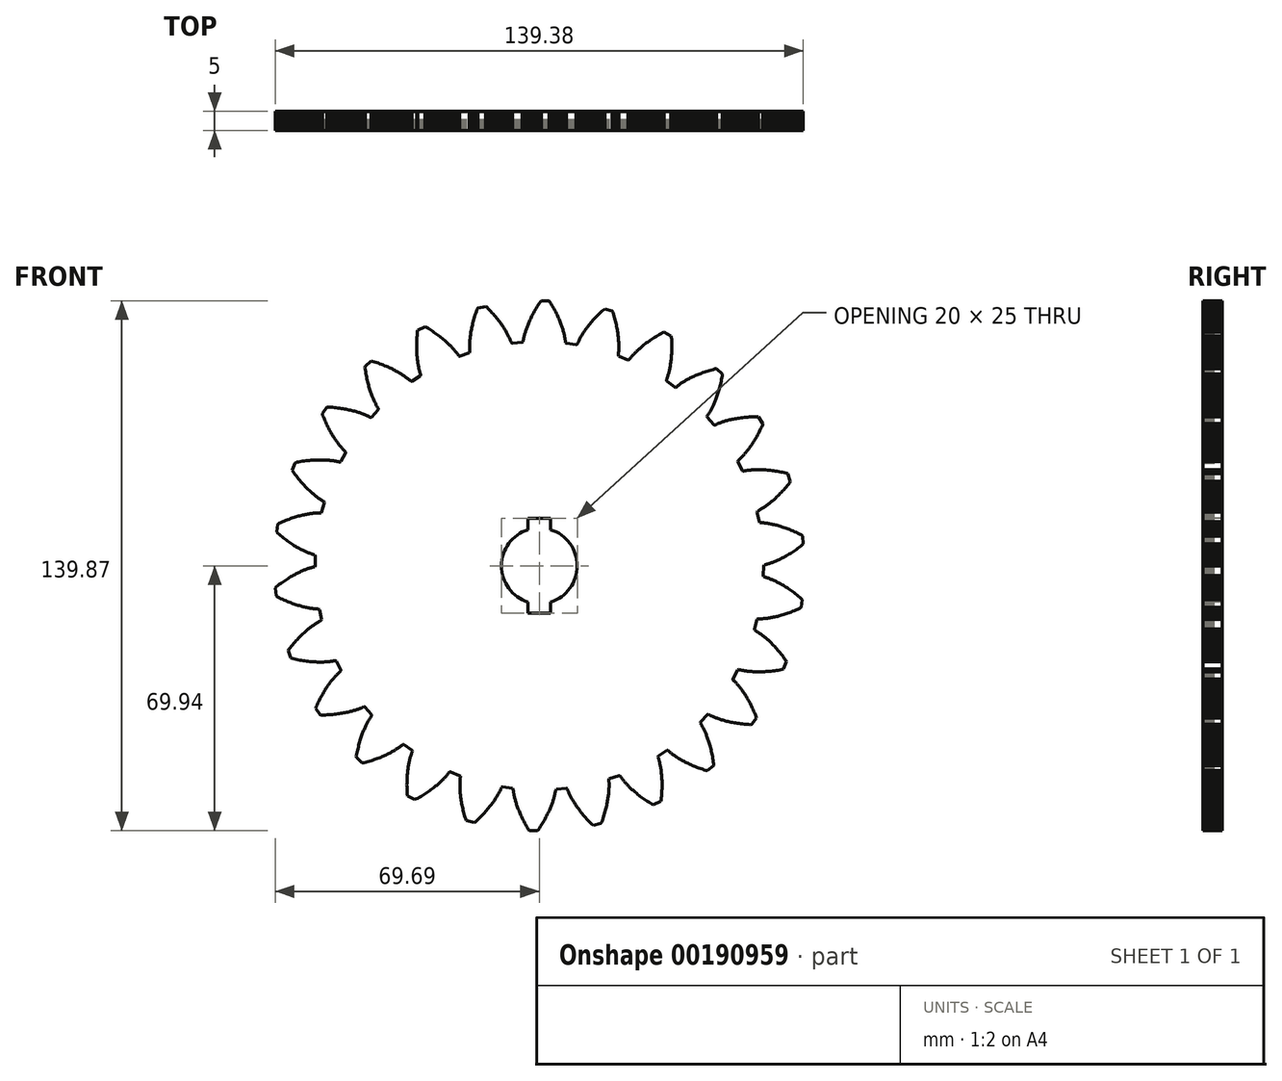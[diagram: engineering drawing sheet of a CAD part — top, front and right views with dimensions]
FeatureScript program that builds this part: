
annotation { "Feature Type Name" : "Feature", "Feature Type Description" : "" }
export const myFeature = defineFeature(function(context is Context, id is Id, definition is map)
    precondition{}
    {
        {
            var Q0;
            Q0=qCreatedBy(makeId("Front.planeOp"),FACE);
            var sketch = newSketch(context, id + "F0", { "sketchPlane" : qUnion([Q0])});
            skLineSegment(sketch, "E0", {"start": v(59.2, 0) * mm, "end": v(59.33, 0.22) * mm});
            skLineSegment(sketch, "E1", {"start": v(59.33, 0.22) * mm, "end": v(59.5, 0.27) * mm});
            skLineSegment(sketch, "E2", {"start": v(59.5, 0.27) * mm, "end": v(59.7, 0.31) * mm});
            skLineSegment(sketch, "E3", {"start": v(59.7, 0.31) * mm, "end": v(59.9, 0.37) * mm});
            skLineSegment(sketch, "E4", {"start": v(59.9, 0.37) * mm, "end": v(60.1, 0.42) * mm});
            skLineSegment(sketch, "E5", {"start": v(60.1, 0.42) * mm, "end": v(60.31, 0.49) * mm});
            skLineSegment(sketch, "E6", {"start": v(60.31, 0.49) * mm, "end": v(60.53, 0.55) * mm});
            skLineSegment(sketch, "E7", {"start": v(60.53, 0.55) * mm, "end": v(60.77, 0.63) * mm});
            skLineSegment(sketch, "E8", {"start": v(60.77, 0.63) * mm, "end": v(61, 0.71) * mm});
            skLineSegment(sketch, "E9", {"start": v(61, 0.71) * mm, "end": v(61.26, 0.8) * mm});
            skLineSegment(sketch, "E10", {"start": v(61.26, 0.8) * mm, "end": v(61.51, 0.9) * mm});
            skLineSegment(sketch, "E11", {"start": v(61.51, 0.9) * mm, "end": v(61.78, 1) * mm});
            skLineSegment(sketch, "E12", {"start": v(61.78, 1) * mm, "end": v(62.06, 1.1) * mm});
            skLineSegment(sketch, "E13", {"start": v(62.06, 1.1) * mm, "end": v(62.34, 1.23) * mm});
            skLineSegment(sketch, "E14", {"start": v(62.34, 1.23) * mm, "end": v(62.63, 1.35) * mm});
            skLineSegment(sketch, "E15", {"start": v(62.63, 1.35) * mm, "end": v(62.93, 1.49) * mm});
            skLineSegment(sketch, "E16", {"start": v(62.93, 1.49) * mm, "end": v(63.24, 1.63) * mm});
            skLineSegment(sketch, "E17", {"start": v(63.24, 1.63) * mm, "end": v(63.55, 1.78) * mm});
            skLineSegment(sketch, "E18", {"start": v(63.55, 1.78) * mm, "end": v(63.87, 1.94) * mm});
            skLineSegment(sketch, "E19", {"start": v(63.87, 1.94) * mm, "end": v(64.2, 2.1) * mm});
            skLineSegment(sketch, "E20", {"start": v(64.2, 2.1) * mm, "end": v(64.53, 2.29) * mm});
            skLineSegment(sketch, "E21", {"start": v(64.53, 2.29) * mm, "end": v(64.88, 2.48) * mm});
            skLineSegment(sketch, "E22", {"start": v(64.88, 2.48) * mm, "end": v(65.22, 2.67) * mm});
            skLineSegment(sketch, "E23", {"start": v(65.22, 2.67) * mm, "end": v(65.58, 2.88) * mm});
            skLineSegment(sketch, "E24", {"start": v(65.58, 2.88) * mm, "end": v(65.94, 3.1) * mm});
            skLineSegment(sketch, "E25", {"start": v(65.94, 3.1) * mm, "end": v(66.3, 3.33) * mm});
            skLineSegment(sketch, "E26", {"start": v(66.3, 3.33) * mm, "end": v(66.68, 3.56) * mm});
            skLineSegment(sketch, "E27", {"start": v(66.68, 3.56) * mm, "end": v(67.06, 3.81) * mm});
            skLineSegment(sketch, "E28", {"start": v(67.06, 3.81) * mm, "end": v(67.44, 4.07) * mm});
            skLineSegment(sketch, "E29", {"start": v(67.44, 4.07) * mm, "end": v(67.83, 4.34) * mm});
            skLineSegment(sketch, "E30", {"start": v(67.83, 4.34) * mm, "end": v(68.22, 4.63) * mm});
            skLineSegment(sketch, "E31", {"start": v(68.22, 4.63) * mm, "end": v(68.62, 4.92) * mm});
            skLineSegment(sketch, "E32", {"start": v(68.62, 4.92) * mm, "end": v(69.02, 5.23) * mm});
            skLineSegment(sketch, "E33", {"start": v(69.02, 5.23) * mm, "end": v(69.43, 5.54) * mm});
            skLineSegment(sketch, "E34", {"start": v(69.43, 5.54) * mm, "end": v(69.7, 5.86) * mm});
            skLineSegment(sketch, "E35", {"start": v(69.7, 5.86) * mm, "end": v(69.49, 7.9) * mm});
            skLineSegment(sketch, "E36", {"start": v(69.49, 7.9) * mm, "end": v(69.17, 8.16) * mm});
            skLineSegment(sketch, "E37", {"start": v(69.17, 8.16) * mm, "end": v(68.7, 8.4) * mm});
            skLineSegment(sketch, "E38", {"start": v(68.7, 8.4) * mm, "end": v(68.25, 8.61) * mm});
            skLineSegment(sketch, "E39", {"start": v(68.25, 8.61) * mm, "end": v(67.8, 8.82) * mm});
            skLineSegment(sketch, "E40", {"start": v(67.8, 8.82) * mm, "end": v(67.37, 9.02) * mm});
            skLineSegment(sketch, "E41", {"start": v(67.37, 9.02) * mm, "end": v(66.93, 9.21) * mm});
            skLineSegment(sketch, "E42", {"start": v(66.93, 9.21) * mm, "end": v(66.5, 9.4) * mm});
            skLineSegment(sketch, "E43", {"start": v(66.5, 9.4) * mm, "end": v(66.09, 9.56) * mm});
            skLineSegment(sketch, "E44", {"start": v(66.09, 9.56) * mm, "end": v(65.67, 9.72) * mm});
            skLineSegment(sketch, "E45", {"start": v(65.67, 9.72) * mm, "end": v(65.27, 9.88) * mm});
            skLineSegment(sketch, "E46", {"start": v(65.27, 9.88) * mm, "end": v(64.87, 10.02) * mm});
            skLineSegment(sketch, "E47", {"start": v(64.87, 10.02) * mm, "end": v(64.49, 10.15) * mm});
            skLineSegment(sketch, "E48", {"start": v(64.49, 10.15) * mm, "end": v(64.1, 10.28) * mm});
            skLineSegment(sketch, "E49", {"start": v(64.1, 10.28) * mm, "end": v(63.73, 10.4) * mm});
            skLineSegment(sketch, "E50", {"start": v(63.73, 10.4) * mm, "end": v(63.37, 10.5) * mm});
            skLineSegment(sketch, "E51", {"start": v(63.37, 10.5) * mm, "end": v(63.01, 10.6) * mm});
            skLineSegment(sketch, "E52", {"start": v(63.01, 10.6) * mm, "end": v(62.67, 10.7) * mm});
            skLineSegment(sketch, "E53", {"start": v(62.67, 10.7) * mm, "end": v(62.33, 10.79) * mm});
            skLineSegment(sketch, "E54", {"start": v(62.33, 10.79) * mm, "end": v(62, 10.87) * mm});
            skLineSegment(sketch, "E55", {"start": v(62, 10.87) * mm, "end": v(61.68, 10.94) * mm});
            skLineSegment(sketch, "E56", {"start": v(61.68, 10.94) * mm, "end": v(61.37, 11) * mm});
            skLineSegment(sketch, "E57", {"start": v(61.37, 11) * mm, "end": v(61.07, 11.06) * mm});
            skLineSegment(sketch, "E58", {"start": v(61.07, 11.06) * mm, "end": v(60.78, 11.12) * mm});
            skLineSegment(sketch, "E59", {"start": v(60.78, 11.12) * mm, "end": v(60.5, 11.17) * mm});
            skLineSegment(sketch, "E60", {"start": v(60.5, 11.17) * mm, "end": v(60.23, 11.21) * mm});
            skLineSegment(sketch, "E61", {"start": v(60.23, 11.21) * mm, "end": v(59.97, 11.25) * mm});
            skLineSegment(sketch, "E62", {"start": v(59.97, 11.25) * mm, "end": v(59.71, 11.28) * mm});
            skLineSegment(sketch, "E63", {"start": v(59.71, 11.28) * mm, "end": v(59.47, 11.31) * mm});
            skLineSegment(sketch, "E64", {"start": v(59.47, 11.31) * mm, "end": v(59.24, 11.33) * mm});
            skLineSegment(sketch, "E65", {"start": v(59.24, 11.33) * mm, "end": v(59.02, 11.35) * mm});
            skLineSegment(sketch, "E66", {"start": v(59.02, 11.35) * mm, "end": v(58.8, 11.37) * mm});
            skLineSegment(sketch, "E67", {"start": v(58.8, 11.37) * mm, "end": v(58.6, 11.38) * mm});
            skLineSegment(sketch, "E68", {"start": v(58.6, 11.38) * mm, "end": v(58.41, 11.4) * mm});
            skLineSegment(sketch, "E69", {"start": v(58.41, 11.4) * mm, "end": v(58.23, 11.4) * mm});
            skLineSegment(sketch, "E70", {"start": v(58.23, 11.4) * mm, "end": v(58.05, 11.6) * mm});
            skLineSegment(sketch, "E71", {"start": v(58.05, 11.6) * mm, "end": v(57.48, 14.17) * mm});
            skLineSegment(sketch, "E72", {"start": v(57.48, 14.17) * mm, "end": v(57.56, 14.42) * mm});
            skLineSegment(sketch, "E73", {"start": v(57.56, 14.42) * mm, "end": v(57.72, 14.5) * mm});
            skLineSegment(sketch, "E74", {"start": v(57.72, 14.5) * mm, "end": v(57.89, 14.59) * mm});
            skLineSegment(sketch, "E75", {"start": v(57.89, 14.59) * mm, "end": v(58.06, 14.69) * mm});
            skLineSegment(sketch, "E76", {"start": v(58.06, 14.69) * mm, "end": v(58.25, 14.8) * mm});
            skLineSegment(sketch, "E77", {"start": v(58.25, 14.8) * mm, "end": v(58.44, 14.9) * mm});
            skLineSegment(sketch, "E78", {"start": v(58.44, 14.9) * mm, "end": v(58.64, 15.03) * mm});
            skLineSegment(sketch, "E79", {"start": v(58.64, 15.03) * mm, "end": v(58.85, 15.15) * mm});
            skLineSegment(sketch, "E80", {"start": v(58.85, 15.15) * mm, "end": v(59.06, 15.3) * mm});
            skLineSegment(sketch, "E81", {"start": v(59.06, 15.3) * mm, "end": v(59.28, 15.44) * mm});
            skLineSegment(sketch, "E82", {"start": v(59.28, 15.44) * mm, "end": v(59.51, 15.6) * mm});
            skLineSegment(sketch, "E83", {"start": v(59.51, 15.6) * mm, "end": v(59.75, 15.75) * mm});
            skLineSegment(sketch, "E84", {"start": v(59.75, 15.75) * mm, "end": v(59.99, 15.93) * mm});
            skLineSegment(sketch, "E85", {"start": v(59.99, 15.93) * mm, "end": v(60.23, 16.11) * mm});
            skLineSegment(sketch, "E86", {"start": v(60.23, 16.11) * mm, "end": v(60.49, 16.3) * mm});
            skLineSegment(sketch, "E87", {"start": v(60.49, 16.3) * mm, "end": v(60.75, 16.5) * mm});
            skLineSegment(sketch, "E88", {"start": v(60.75, 16.5) * mm, "end": v(61, 16.72) * mm});
            skLineSegment(sketch, "E89", {"start": v(61, 16.72) * mm, "end": v(61.28, 16.94) * mm});
            skLineSegment(sketch, "E90", {"start": v(61.28, 16.94) * mm, "end": v(61.55, 17.17) * mm});
            skLineSegment(sketch, "E91", {"start": v(61.55, 17.17) * mm, "end": v(61.83, 17.41) * mm});
            skLineSegment(sketch, "E92", {"start": v(61.83, 17.41) * mm, "end": v(62.11, 17.67) * mm});
            skLineSegment(sketch, "E93", {"start": v(62.11, 17.67) * mm, "end": v(62.4, 17.93) * mm});
            skLineSegment(sketch, "E94", {"start": v(62.4, 17.93) * mm, "end": v(62.69, 18.2) * mm});
            skLineSegment(sketch, "E95", {"start": v(62.69, 18.2) * mm, "end": v(62.98, 18.5) * mm});
            skLineSegment(sketch, "E96", {"start": v(62.98, 18.5) * mm, "end": v(63.28, 18.79) * mm});
            skLineSegment(sketch, "E97", {"start": v(63.28, 18.79) * mm, "end": v(63.58, 19.1) * mm});
            skLineSegment(sketch, "E98", {"start": v(63.58, 19.1) * mm, "end": v(63.89, 19.42) * mm});
            skLineSegment(sketch, "E99", {"start": v(63.89, 19.42) * mm, "end": v(64.2, 19.75) * mm});
            skLineSegment(sketch, "E100", {"start": v(64.2, 19.75) * mm, "end": v(64.5, 20.1) * mm});
            skLineSegment(sketch, "E101", {"start": v(64.5, 20.1) * mm, "end": v(64.82, 20.45) * mm});
            skLineSegment(sketch, "E102", {"start": v(64.82, 20.45) * mm, "end": v(65.13, 20.82) * mm});
            skLineSegment(sketch, "E103", {"start": v(65.13, 20.82) * mm, "end": v(65.45, 21.2) * mm});
            skLineSegment(sketch, "E104", {"start": v(65.45, 21.2) * mm, "end": v(65.76, 21.6) * mm});
            skLineSegment(sketch, "E105", {"start": v(65.76, 21.6) * mm, "end": v(66.08, 22) * mm});
            skLineSegment(sketch, "E106", {"start": v(66.08, 22) * mm, "end": v(66.26, 22.37) * mm});
            skLineSegment(sketch, "E107", {"start": v(66.26, 22.37) * mm, "end": v(65.58, 24.3) * mm});
            skLineSegment(sketch, "E108", {"start": v(65.58, 24.3) * mm, "end": v(65.2, 24.48) * mm});
            skLineSegment(sketch, "E109", {"start": v(65.2, 24.48) * mm, "end": v(64.7, 24.6) * mm});
            skLineSegment(sketch, "E110", {"start": v(64.7, 24.6) * mm, "end": v(64.2, 24.7) * mm});
            skLineSegment(sketch, "E111", {"start": v(64.2, 24.7) * mm, "end": v(63.72, 24.8) * mm});
            skLineSegment(sketch, "E112", {"start": v(63.72, 24.8) * mm, "end": v(63.25, 24.88) * mm});
            skLineSegment(sketch, "E113", {"start": v(63.25, 24.88) * mm, "end": v(62.78, 24.96) * mm});
            skLineSegment(sketch, "E114", {"start": v(62.78, 24.96) * mm, "end": v(62.32, 25.04) * mm});
            skLineSegment(sketch, "E115", {"start": v(62.32, 25.04) * mm, "end": v(61.88, 25.1) * mm});
            skLineSegment(sketch, "E116", {"start": v(61.88, 25.1) * mm, "end": v(61.44, 25.16) * mm});
            skLineSegment(sketch, "E117", {"start": v(61.44, 25.16) * mm, "end": v(61.01, 25.2) * mm});
            skLineSegment(sketch, "E118", {"start": v(61.01, 25.2) * mm, "end": v(60.6, 25.25) * mm});
            skLineSegment(sketch, "E119", {"start": v(60.6, 25.25) * mm, "end": v(60.18, 25.29) * mm});
            skLineSegment(sketch, "E120", {"start": v(60.18, 25.29) * mm, "end": v(59.78, 25.32) * mm});
            skLineSegment(sketch, "E121", {"start": v(59.78, 25.32) * mm, "end": v(59.4, 25.34) * mm});
            skLineSegment(sketch, "E122", {"start": v(59.4, 25.34) * mm, "end": v(59.01, 25.36) * mm});
            skLineSegment(sketch, "E123", {"start": v(59.01, 25.36) * mm, "end": v(58.64, 25.38) * mm});
            skLineSegment(sketch, "E124", {"start": v(58.64, 25.38) * mm, "end": v(58.29, 25.38) * mm});
            skLineSegment(sketch, "E125", {"start": v(58.29, 25.38) * mm, "end": v(57.94, 25.39) * mm});
            skLineSegment(sketch, "E126", {"start": v(57.94, 25.39) * mm, "end": v(57.6, 25.39) * mm});
            skLineSegment(sketch, "E127", {"start": v(57.6, 25.39) * mm, "end": v(57.27, 25.38) * mm});
            skLineSegment(sketch, "E128", {"start": v(57.27, 25.38) * mm, "end": v(56.96, 25.37) * mm});
            skLineSegment(sketch, "E129", {"start": v(56.96, 25.37) * mm, "end": v(56.65, 25.36) * mm});
            skLineSegment(sketch, "E130", {"start": v(56.65, 25.36) * mm, "end": v(56.35, 25.34) * mm});
            skLineSegment(sketch, "E131", {"start": v(56.35, 25.34) * mm, "end": v(56.07, 25.32) * mm});
            skLineSegment(sketch, "E132", {"start": v(56.07, 25.32) * mm, "end": v(55.8, 25.3) * mm});
            skLineSegment(sketch, "E133", {"start": v(55.8, 25.3) * mm, "end": v(55.53, 25.27) * mm});
            skLineSegment(sketch, "E134", {"start": v(55.53, 25.27) * mm, "end": v(55.28, 25.24) * mm});
            skLineSegment(sketch, "E135", {"start": v(55.28, 25.24) * mm, "end": v(55.04, 25.21) * mm});
            skLineSegment(sketch, "E136", {"start": v(55.04, 25.21) * mm, "end": v(54.8, 25.18) * mm});
            skLineSegment(sketch, "E137", {"start": v(54.8, 25.18) * mm, "end": v(54.58, 25.15) * mm});
            skLineSegment(sketch, "E138", {"start": v(54.58, 25.15) * mm, "end": v(54.37, 25.11) * mm});
            skLineSegment(sketch, "E139", {"start": v(54.37, 25.11) * mm, "end": v(54.17, 25.08) * mm});
            skLineSegment(sketch, "E140", {"start": v(54.17, 25.08) * mm, "end": v(53.99, 25.04) * mm});
            skLineSegment(sketch, "E141", {"start": v(53.99, 25.04) * mm, "end": v(53.8, 25) * mm});
            skLineSegment(sketch, "E142", {"start": v(53.8, 25) * mm, "end": v(53.59, 25.15) * mm});
            skLineSegment(sketch, "E143", {"start": v(53.59, 25.15) * mm, "end": v(52.42, 27.5) * mm});
            skLineSegment(sketch, "E144", {"start": v(52.42, 27.5) * mm, "end": v(52.43, 27.77) * mm});
            skLineSegment(sketch, "E145", {"start": v(52.43, 27.77) * mm, "end": v(52.57, 27.9) * mm});
            skLineSegment(sketch, "E146", {"start": v(52.57, 27.9) * mm, "end": v(52.71, 28.02) * mm});
            skLineSegment(sketch, "E147", {"start": v(52.71, 28.02) * mm, "end": v(52.86, 28.16) * mm});
            skLineSegment(sketch, "E148", {"start": v(52.86, 28.16) * mm, "end": v(53.02, 28.3) * mm});
            skLineSegment(sketch, "E149", {"start": v(53.02, 28.3) * mm, "end": v(53.18, 28.46) * mm});
            skLineSegment(sketch, "E150", {"start": v(53.18, 28.46) * mm, "end": v(53.34, 28.62) * mm});
            skLineSegment(sketch, "E151", {"start": v(53.34, 28.62) * mm, "end": v(53.51, 28.8) * mm});
            skLineSegment(sketch, "E152", {"start": v(53.51, 28.8) * mm, "end": v(53.69, 28.98) * mm});
            skLineSegment(sketch, "E153", {"start": v(53.69, 28.98) * mm, "end": v(53.87, 29.18) * mm});
            skLineSegment(sketch, "E154", {"start": v(53.87, 29.18) * mm, "end": v(54.05, 29.38) * mm});
            skLineSegment(sketch, "E155", {"start": v(54.05, 29.38) * mm, "end": v(54.24, 29.6) * mm});
            skLineSegment(sketch, "E156", {"start": v(54.24, 29.6) * mm, "end": v(54.43, 29.82) * mm});
            skLineSegment(sketch, "E157", {"start": v(54.43, 29.82) * mm, "end": v(54.63, 30.06) * mm});
            skLineSegment(sketch, "E158", {"start": v(54.63, 30.06) * mm, "end": v(54.83, 30.3) * mm});
            skLineSegment(sketch, "E159", {"start": v(54.83, 30.3) * mm, "end": v(55.03, 30.56) * mm});
            skLineSegment(sketch, "E160", {"start": v(55.03, 30.56) * mm, "end": v(55.23, 30.83) * mm});
            skLineSegment(sketch, "E161", {"start": v(55.23, 30.83) * mm, "end": v(55.44, 31.1) * mm});
            skLineSegment(sketch, "E162", {"start": v(55.44, 31.1) * mm, "end": v(55.65, 31.4) * mm});
            skLineSegment(sketch, "E163", {"start": v(55.65, 31.4) * mm, "end": v(55.86, 31.7) * mm});
            skLineSegment(sketch, "E164", {"start": v(55.86, 31.7) * mm, "end": v(56.08, 32.02) * mm});
            skLineSegment(sketch, "E165", {"start": v(56.08, 32.02) * mm, "end": v(56.3, 32.34) * mm});
            skLineSegment(sketch, "E166", {"start": v(56.3, 32.34) * mm, "end": v(56.51, 32.68) * mm});
            skLineSegment(sketch, "E167", {"start": v(56.51, 32.68) * mm, "end": v(56.73, 33.03) * mm});
            skLineSegment(sketch, "E168", {"start": v(56.73, 33.03) * mm, "end": v(56.95, 33.39) * mm});
            skLineSegment(sketch, "E169", {"start": v(56.95, 33.39) * mm, "end": v(57.17, 33.76) * mm});
            skLineSegment(sketch, "E170", {"start": v(57.17, 33.76) * mm, "end": v(57.39, 34.14) * mm});
            skLineSegment(sketch, "E171", {"start": v(57.39, 34.14) * mm, "end": v(57.6, 34.54) * mm});
            skLineSegment(sketch, "E172", {"start": v(57.6, 34.54) * mm, "end": v(57.82, 34.95) * mm});
            skLineSegment(sketch, "E173", {"start": v(57.82, 34.95) * mm, "end": v(58.04, 35.37) * mm});
            skLineSegment(sketch, "E174", {"start": v(58.04, 35.37) * mm, "end": v(58.26, 35.8) * mm});
            skLineSegment(sketch, "E175", {"start": v(58.26, 35.8) * mm, "end": v(58.47, 36.25) * mm});
            skLineSegment(sketch, "E176", {"start": v(58.47, 36.25) * mm, "end": v(58.69, 36.7) * mm});
            skLineSegment(sketch, "E177", {"start": v(58.69, 36.7) * mm, "end": v(58.9, 37.17) * mm});
            skLineSegment(sketch, "E178", {"start": v(58.9, 37.17) * mm, "end": v(58.98, 37.58) * mm});
            skLineSegment(sketch, "E179", {"start": v(58.98, 37.58) * mm, "end": v(57.86, 39.29) * mm});
            skLineSegment(sketch, "E180", {"start": v(57.86, 39.29) * mm, "end": v(57.45, 39.37) * mm});
            skLineSegment(sketch, "E181", {"start": v(57.45, 39.37) * mm, "end": v(56.94, 39.36) * mm});
            skLineSegment(sketch, "E182", {"start": v(56.94, 39.36) * mm, "end": v(56.43, 39.35) * mm});
            skLineSegment(sketch, "E183", {"start": v(56.43, 39.35) * mm, "end": v(55.94, 39.32) * mm});
            skLineSegment(sketch, "E184", {"start": v(55.94, 39.32) * mm, "end": v(55.46, 39.3) * mm});
            skLineSegment(sketch, "E185", {"start": v(55.46, 39.3) * mm, "end": v(54.98, 39.26) * mm});
            skLineSegment(sketch, "E186", {"start": v(54.98, 39.26) * mm, "end": v(54.52, 39.22) * mm});
            skLineSegment(sketch, "E187", {"start": v(54.52, 39.22) * mm, "end": v(54.07, 39.18) * mm});
            skLineSegment(sketch, "E188", {"start": v(54.07, 39.18) * mm, "end": v(53.63, 39.13) * mm});
            skLineSegment(sketch, "E189", {"start": v(53.63, 39.13) * mm, "end": v(53.2, 39.08) * mm});
            skLineSegment(sketch, "E190", {"start": v(53.2, 39.08) * mm, "end": v(52.79, 39.02) * mm});
            skLineSegment(sketch, "E191", {"start": v(52.79, 39.02) * mm, "end": v(52.38, 38.96) * mm});
            skLineSegment(sketch, "E192", {"start": v(52.38, 38.96) * mm, "end": v(51.99, 38.9) * mm});
            skLineSegment(sketch, "E193", {"start": v(51.99, 38.9) * mm, "end": v(51.6, 38.82) * mm});
            skLineSegment(sketch, "E194", {"start": v(51.6, 38.82) * mm, "end": v(51.23, 38.75) * mm});
            skLineSegment(sketch, "E195", {"start": v(51.23, 38.75) * mm, "end": v(50.87, 38.67) * mm});
            skLineSegment(sketch, "E196", {"start": v(50.87, 38.67) * mm, "end": v(50.52, 38.6) * mm});
            skLineSegment(sketch, "E197", {"start": v(50.52, 38.6) * mm, "end": v(50.18, 38.52) * mm});
            skLineSegment(sketch, "E198", {"start": v(50.18, 38.52) * mm, "end": v(49.85, 38.43) * mm});
            skLineSegment(sketch, "E199", {"start": v(49.85, 38.43) * mm, "end": v(49.53, 38.35) * mm});
            skLineSegment(sketch, "E200", {"start": v(49.53, 38.35) * mm, "end": v(49.23, 38.27) * mm});
            skLineSegment(sketch, "E201", {"start": v(49.23, 38.27) * mm, "end": v(48.93, 38.18) * mm});
            skLineSegment(sketch, "E202", {"start": v(48.93, 38.18) * mm, "end": v(48.65, 38.1) * mm});
            skLineSegment(sketch, "E203", {"start": v(48.65, 38.1) * mm, "end": v(48.38, 38) * mm});
            skLineSegment(sketch, "E204", {"start": v(48.38, 38) * mm, "end": v(48.12, 37.92) * mm});
            skLineSegment(sketch, "E205", {"start": v(48.12, 37.92) * mm, "end": v(47.87, 37.83) * mm});
            skLineSegment(sketch, "E206", {"start": v(47.87, 37.83) * mm, "end": v(47.63, 37.74) * mm});
            skLineSegment(sketch, "E207", {"start": v(47.63, 37.74) * mm, "end": v(47.4, 37.65) * mm});
            skLineSegment(sketch, "E208", {"start": v(47.4, 37.65) * mm, "end": v(47.18, 37.56) * mm});
            skLineSegment(sketch, "E209", {"start": v(47.18, 37.56) * mm, "end": v(46.98, 37.48) * mm});
            skLineSegment(sketch, "E210", {"start": v(46.98, 37.48) * mm, "end": v(46.78, 37.4) * mm});
            skLineSegment(sketch, "E211", {"start": v(46.78, 37.4) * mm, "end": v(46.6, 37.31) * mm});
            skLineSegment(sketch, "E212", {"start": v(46.6, 37.31) * mm, "end": v(46.42, 37.23) * mm});
            skLineSegment(sketch, "E213", {"start": v(46.42, 37.23) * mm, "end": v(46.26, 37.15) * mm});
            skLineSegment(sketch, "E214", {"start": v(46.26, 37.15) * mm, "end": v(46.01, 37.24) * mm});
            skLineSegment(sketch, "E215", {"start": v(46.01, 37.24) * mm, "end": v(44.31, 39.25) * mm});
            skLineSegment(sketch, "E216", {"start": v(44.31, 39.25) * mm, "end": v(44.26, 39.51) * mm});
            skLineSegment(sketch, "E217", {"start": v(44.26, 39.51) * mm, "end": v(44.37, 39.66) * mm});
            skLineSegment(sketch, "E218", {"start": v(44.37, 39.66) * mm, "end": v(44.48, 39.82) * mm});
            skLineSegment(sketch, "E219", {"start": v(44.48, 39.82) * mm, "end": v(44.59, 39.99) * mm});
            skLineSegment(sketch, "E220", {"start": v(44.59, 39.99) * mm, "end": v(44.7, 40.17) * mm});
            skLineSegment(sketch, "E221", {"start": v(44.7, 40.17) * mm, "end": v(44.82, 40.36) * mm});
            skLineSegment(sketch, "E222", {"start": v(44.82, 40.36) * mm, "end": v(44.94, 40.56) * mm});
            skLineSegment(sketch, "E223", {"start": v(44.94, 40.56) * mm, "end": v(45.07, 40.77) * mm});
            skLineSegment(sketch, "E224", {"start": v(45.07, 40.77) * mm, "end": v(45.2, 40.99) * mm});
            skLineSegment(sketch, "E225", {"start": v(45.2, 40.99) * mm, "end": v(45.32, 41.22) * mm});
            skLineSegment(sketch, "E226", {"start": v(45.32, 41.22) * mm, "end": v(45.45, 41.46) * mm});
            skLineSegment(sketch, "E227", {"start": v(45.45, 41.46) * mm, "end": v(45.58, 41.72) * mm});
            skLineSegment(sketch, "E228", {"start": v(45.58, 41.72) * mm, "end": v(45.71, 41.98) * mm});
            skLineSegment(sketch, "E229", {"start": v(45.71, 41.98) * mm, "end": v(45.85, 42.26) * mm});
            skLineSegment(sketch, "E230", {"start": v(45.85, 42.26) * mm, "end": v(45.98, 42.54) * mm});
            skLineSegment(sketch, "E231", {"start": v(45.98, 42.54) * mm, "end": v(46.12, 42.84) * mm});
            skLineSegment(sketch, "E232", {"start": v(46.12, 42.84) * mm, "end": v(46.25, 43.15) * mm});
            skLineSegment(sketch, "E233", {"start": v(46.25, 43.15) * mm, "end": v(46.39, 43.47) * mm});
            skLineSegment(sketch, "E234", {"start": v(46.39, 43.47) * mm, "end": v(46.52, 43.8) * mm});
            skLineSegment(sketch, "E235", {"start": v(46.52, 43.8) * mm, "end": v(46.65, 44.15) * mm});
            skLineSegment(sketch, "E236", {"start": v(46.65, 44.15) * mm, "end": v(46.79, 44.5) * mm});
            skLineSegment(sketch, "E237", {"start": v(46.79, 44.5) * mm, "end": v(46.92, 44.87) * mm});
            skLineSegment(sketch, "E238", {"start": v(46.92, 44.87) * mm, "end": v(47.05, 45.25) * mm});
            skLineSegment(sketch, "E239", {"start": v(47.05, 45.25) * mm, "end": v(47.18, 45.64) * mm});
            skLineSegment(sketch, "E240", {"start": v(47.18, 45.64) * mm, "end": v(47.3, 46.04) * mm});
            skLineSegment(sketch, "E241", {"start": v(47.3, 46.04) * mm, "end": v(47.43, 46.46) * mm});
            skLineSegment(sketch, "E242", {"start": v(47.43, 46.46) * mm, "end": v(47.55, 46.88) * mm});
            skLineSegment(sketch, "E243", {"start": v(47.55, 46.88) * mm, "end": v(47.66, 47.32) * mm});
            skLineSegment(sketch, "E244", {"start": v(47.66, 47.32) * mm, "end": v(47.78, 47.77) * mm});
            skLineSegment(sketch, "E245", {"start": v(47.78, 47.77) * mm, "end": v(47.89, 48.23) * mm});
            skLineSegment(sketch, "E246", {"start": v(47.89, 48.23) * mm, "end": v(48, 48.7) * mm});
            skLineSegment(sketch, "E247", {"start": v(48, 48.7) * mm, "end": v(48.1, 49.19) * mm});
            skLineSegment(sketch, "E248", {"start": v(48.1, 49.19) * mm, "end": v(48.2, 49.68) * mm});
            skLineSegment(sketch, "E249", {"start": v(48.2, 49.68) * mm, "end": v(48.3, 50.19) * mm});
            skLineSegment(sketch, "E250", {"start": v(48.3, 50.19) * mm, "end": v(48.28, 50.6) * mm});
            skLineSegment(sketch, "E251", {"start": v(48.28, 50.6) * mm, "end": v(46.77, 52) * mm});
            skLineSegment(sketch, "E252", {"start": v(46.77, 52) * mm, "end": v(46.36, 51.98) * mm});
            skLineSegment(sketch, "E253", {"start": v(46.36, 51.98) * mm, "end": v(45.86, 51.84) * mm});
            skLineSegment(sketch, "E254", {"start": v(45.86, 51.84) * mm, "end": v(45.38, 51.7) * mm});
            skLineSegment(sketch, "E255", {"start": v(45.38, 51.7) * mm, "end": v(44.9, 51.57) * mm});
            skLineSegment(sketch, "E256", {"start": v(44.9, 51.57) * mm, "end": v(44.44, 51.43) * mm});
            skLineSegment(sketch, "E257", {"start": v(44.44, 51.43) * mm, "end": v(44, 51.28) * mm});
            skLineSegment(sketch, "E258", {"start": v(44, 51.28) * mm, "end": v(43.55, 51.13) * mm});
            skLineSegment(sketch, "E259", {"start": v(43.55, 51.13) * mm, "end": v(43.13, 50.98) * mm});
            skLineSegment(sketch, "E260", {"start": v(43.13, 50.98) * mm, "end": v(42.7, 50.83) * mm});
            skLineSegment(sketch, "E261", {"start": v(42.7, 50.83) * mm, "end": v(42.3, 50.67) * mm});
            skLineSegment(sketch, "E262", {"start": v(42.3, 50.67) * mm, "end": v(41.92, 50.52) * mm});
            skLineSegment(sketch, "E263", {"start": v(41.92, 50.52) * mm, "end": v(41.54, 50.36) * mm});
            skLineSegment(sketch, "E264", {"start": v(41.54, 50.36) * mm, "end": v(41.17, 50.2) * mm});
            skLineSegment(sketch, "E265", {"start": v(41.17, 50.2) * mm, "end": v(40.81, 50.04) * mm});
            skLineSegment(sketch, "E266", {"start": v(40.81, 50.04) * mm, "end": v(40.47, 49.88) * mm});
            skLineSegment(sketch, "E267", {"start": v(40.47, 49.88) * mm, "end": v(40.13, 49.72) * mm});
            skLineSegment(sketch, "E268", {"start": v(40.13, 49.72) * mm, "end": v(39.81, 49.56) * mm});
            skLineSegment(sketch, "E269", {"start": v(39.81, 49.56) * mm, "end": v(39.5, 49.4) * mm});
            skLineSegment(sketch, "E270", {"start": v(39.5, 49.4) * mm, "end": v(39.2, 49.25) * mm});
            skLineSegment(sketch, "E271", {"start": v(39.2, 49.25) * mm, "end": v(38.92, 49.1) * mm});
            skLineSegment(sketch, "E272", {"start": v(38.92, 49.1) * mm, "end": v(38.64, 48.93) * mm});
            skLineSegment(sketch, "E273", {"start": v(38.64, 48.93) * mm, "end": v(38.38, 48.78) * mm});
            skLineSegment(sketch, "E274", {"start": v(38.38, 48.78) * mm, "end": v(38.12, 48.63) * mm});
            skLineSegment(sketch, "E275", {"start": v(38.12, 48.63) * mm, "end": v(37.88, 48.48) * mm});
            skLineSegment(sketch, "E276", {"start": v(37.88, 48.48) * mm, "end": v(37.65, 48.33) * mm});
            skLineSegment(sketch, "E277", {"start": v(37.65, 48.33) * mm, "end": v(37.42, 48.18) * mm});
            skLineSegment(sketch, "E278", {"start": v(37.42, 48.18) * mm, "end": v(37.21, 48.04) * mm});
            skLineSegment(sketch, "E279", {"start": v(37.21, 48.04) * mm, "end": v(37.01, 47.9) * mm});
            skLineSegment(sketch, "E280", {"start": v(37.01, 47.9) * mm, "end": v(36.82, 47.77) * mm});
            skLineSegment(sketch, "E281", {"start": v(36.82, 47.77) * mm, "end": v(36.65, 47.63) * mm});
            skLineSegment(sketch, "E282", {"start": v(36.65, 47.63) * mm, "end": v(36.47, 47.5) * mm});
            skLineSegment(sketch, "E283", {"start": v(36.47, 47.5) * mm, "end": v(36.31, 47.38) * mm});
            skLineSegment(sketch, "E284", {"start": v(36.31, 47.38) * mm, "end": v(36.17, 47.26) * mm});
            skLineSegment(sketch, "E285", {"start": v(36.17, 47.26) * mm, "end": v(36.03, 47.15) * mm});
            skLineSegment(sketch, "E286", {"start": v(36.03, 47.15) * mm, "end": v(35.76, 47.17) * mm});
            skLineSegment(sketch, "E287", {"start": v(35.76, 47.17) * mm, "end": v(33.63, 48.72) * mm});
            skLineSegment(sketch, "E288", {"start": v(33.63, 48.72) * mm, "end": v(33.52, 48.96) * mm});
            skLineSegment(sketch, "E289", {"start": v(33.52, 48.96) * mm, "end": v(33.59, 49.13) * mm});
            skLineSegment(sketch, "E290", {"start": v(33.59, 49.13) * mm, "end": v(33.65, 49.3) * mm});
            skLineSegment(sketch, "E291", {"start": v(33.65, 49.3) * mm, "end": v(33.72, 49.5) * mm});
            skLineSegment(sketch, "E292", {"start": v(33.72, 49.5) * mm, "end": v(33.8, 49.7) * mm});
            skLineSegment(sketch, "E293", {"start": v(33.8, 49.7) * mm, "end": v(33.86, 49.91) * mm});
            skLineSegment(sketch, "E294", {"start": v(33.86, 49.91) * mm, "end": v(33.93, 50.13) * mm});
            skLineSegment(sketch, "E295", {"start": v(33.93, 50.13) * mm, "end": v(34, 50.37) * mm});
            skLineSegment(sketch, "E296", {"start": v(34, 50.37) * mm, "end": v(34.07, 50.61) * mm});
            skLineSegment(sketch, "E297", {"start": v(34.07, 50.61) * mm, "end": v(34.14, 50.87) * mm});
            skLineSegment(sketch, "E298", {"start": v(34.14, 50.87) * mm, "end": v(34.2, 51.13) * mm});
            skLineSegment(sketch, "E299", {"start": v(34.2, 51.13) * mm, "end": v(34.27, 51.41) * mm});
            skLineSegment(sketch, "E300", {"start": v(34.27, 51.41) * mm, "end": v(34.34, 51.7) * mm});
            skLineSegment(sketch, "E301", {"start": v(34.34, 51.7) * mm, "end": v(34.4, 52) * mm});
            skLineSegment(sketch, "E302", {"start": v(34.4, 52) * mm, "end": v(34.46, 52.31) * mm});
            skLineSegment(sketch, "E303", {"start": v(34.46, 52.31) * mm, "end": v(34.52, 52.63) * mm});
            skLineSegment(sketch, "E304", {"start": v(34.52, 52.63) * mm, "end": v(34.58, 52.97) * mm});
            skLineSegment(sketch, "E305", {"start": v(34.58, 52.97) * mm, "end": v(34.63, 53.31) * mm});
            skLineSegment(sketch, "E306", {"start": v(34.63, 53.31) * mm, "end": v(34.69, 53.67) * mm});
            skLineSegment(sketch, "E307", {"start": v(34.69, 53.67) * mm, "end": v(34.73, 54.03) * mm});
            skLineSegment(sketch, "E308", {"start": v(34.73, 54.03) * mm, "end": v(34.78, 54.4) * mm});
            skLineSegment(sketch, "E309", {"start": v(34.78, 54.4) * mm, "end": v(34.82, 54.8) * mm});
            skLineSegment(sketch, "E310", {"start": v(34.82, 54.8) * mm, "end": v(34.85, 55.2) * mm});
            skLineSegment(sketch, "E311", {"start": v(34.85, 55.2) * mm, "end": v(34.88, 55.6) * mm});
            skLineSegment(sketch, "E312", {"start": v(34.88, 55.6) * mm, "end": v(34.9, 56.03) * mm});
            skLineSegment(sketch, "E313", {"start": v(34.9, 56.03) * mm, "end": v(34.93, 56.46) * mm});
            skLineSegment(sketch, "E314", {"start": v(34.93, 56.46) * mm, "end": v(34.95, 56.9) * mm});
            skLineSegment(sketch, "E315", {"start": v(34.95, 56.9) * mm, "end": v(34.95, 57.35) * mm});
            skLineSegment(sketch, "E316", {"start": v(34.95, 57.35) * mm, "end": v(34.96, 57.82) * mm});
            skLineSegment(sketch, "E317", {"start": v(34.96, 57.82) * mm, "end": v(34.96, 58.29) * mm});
            skLineSegment(sketch, "E318", {"start": v(34.96, 58.29) * mm, "end": v(34.95, 58.77) * mm});
            skLineSegment(sketch, "E319", {"start": v(34.95, 58.77) * mm, "end": v(34.93, 59.27) * mm});
            skLineSegment(sketch, "E320", {"start": v(34.93, 59.27) * mm, "end": v(34.9, 59.77) * mm});
            skLineSegment(sketch, "E321", {"start": v(34.9, 59.77) * mm, "end": v(34.88, 60.29) * mm});
            skLineSegment(sketch, "E322", {"start": v(34.88, 60.29) * mm, "end": v(34.77, 60.68) * mm});
            skLineSegment(sketch, "E323", {"start": v(34.77, 60.68) * mm, "end": v(32.97, 61.68) * mm});
            skLineSegment(sketch, "E324", {"start": v(32.97, 61.68) * mm, "end": v(32.58, 61.56) * mm});
            skLineSegment(sketch, "E325", {"start": v(32.58, 61.56) * mm, "end": v(32.12, 61.31) * mm});
            skLineSegment(sketch, "E326", {"start": v(32.12, 61.31) * mm, "end": v(31.68, 61.06) * mm});
            skLineSegment(sketch, "E327", {"start": v(31.68, 61.06) * mm, "end": v(31.26, 60.82) * mm});
            skLineSegment(sketch, "E328", {"start": v(31.26, 60.82) * mm, "end": v(30.84, 60.57) * mm});
            skLineSegment(sketch, "E329", {"start": v(30.84, 60.57) * mm, "end": v(30.44, 60.32) * mm});
            skLineSegment(sketch, "E330", {"start": v(30.44, 60.32) * mm, "end": v(30.05, 60.07) * mm});
            skLineSegment(sketch, "E331", {"start": v(30.05, 60.07) * mm, "end": v(29.67, 59.82) * mm});
            skLineSegment(sketch, "E332", {"start": v(29.67, 59.82) * mm, "end": v(29.3, 59.57) * mm});
            skLineSegment(sketch, "E333", {"start": v(29.3, 59.57) * mm, "end": v(28.95, 59.33) * mm});
            skLineSegment(sketch, "E334", {"start": v(28.95, 59.33) * mm, "end": v(28.6, 59.08) * mm});
            skLineSegment(sketch, "E335", {"start": v(28.6, 59.08) * mm, "end": v(28.28, 58.84) * mm});
            skLineSegment(sketch, "E336", {"start": v(28.28, 58.84) * mm, "end": v(27.96, 58.6) * mm});
            skLineSegment(sketch, "E337", {"start": v(27.96, 58.6) * mm, "end": v(27.65, 58.36) * mm});
            skLineSegment(sketch, "E338", {"start": v(27.65, 58.36) * mm, "end": v(27.35, 58.12) * mm});
            skLineSegment(sketch, "E339", {"start": v(27.35, 58.12) * mm, "end": v(27.07, 57.88) * mm});
            skLineSegment(sketch, "E340", {"start": v(27.07, 57.88) * mm, "end": v(26.8, 57.65) * mm});
            skLineSegment(sketch, "E341", {"start": v(26.8, 57.65) * mm, "end": v(26.53, 57.42) * mm});
            skLineSegment(sketch, "E342", {"start": v(26.53, 57.42) * mm, "end": v(26.28, 57.2) * mm});
            skLineSegment(sketch, "E343", {"start": v(26.28, 57.2) * mm, "end": v(26.04, 56.98) * mm});
            skLineSegment(sketch, "E344", {"start": v(26.04, 56.98) * mm, "end": v(25.8, 56.76) * mm});
            skLineSegment(sketch, "E345", {"start": v(25.8, 56.76) * mm, "end": v(25.59, 56.55) * mm});
            skLineSegment(sketch, "E346", {"start": v(25.59, 56.55) * mm, "end": v(25.38, 56.34) * mm});
            skLineSegment(sketch, "E347", {"start": v(25.38, 56.34) * mm, "end": v(25.18, 56.13) * mm});
            skLineSegment(sketch, "E348", {"start": v(25.18, 56.13) * mm, "end": v(24.99, 55.93) * mm});
            skLineSegment(sketch, "E349", {"start": v(24.99, 55.93) * mm, "end": v(24.8, 55.74) * mm});
            skLineSegment(sketch, "E350", {"start": v(24.8, 55.74) * mm, "end": v(24.64, 55.55) * mm});
            skLineSegment(sketch, "E351", {"start": v(24.64, 55.55) * mm, "end": v(24.47, 55.37) * mm});
            skLineSegment(sketch, "E352", {"start": v(24.47, 55.37) * mm, "end": v(24.32, 55.2) * mm});
            skLineSegment(sketch, "E353", {"start": v(24.32, 55.2) * mm, "end": v(24.18, 55.02) * mm});
            skLineSegment(sketch, "E354", {"start": v(24.18, 55.02) * mm, "end": v(24.05, 54.85) * mm});
            skLineSegment(sketch, "E355", {"start": v(24.05, 54.85) * mm, "end": v(23.92, 54.7) * mm});
            skLineSegment(sketch, "E356", {"start": v(23.92, 54.7) * mm, "end": v(23.8, 54.54) * mm});
            skLineSegment(sketch, "E357", {"start": v(23.8, 54.54) * mm, "end": v(23.7, 54.4) * mm});
            skLineSegment(sketch, "E358", {"start": v(23.7, 54.4) * mm, "end": v(23.44, 54.36) * mm});
            skLineSegment(sketch, "E359", {"start": v(23.44, 54.36) * mm, "end": v(21, 55.35) * mm});
            skLineSegment(sketch, "E360", {"start": v(21, 55.35) * mm, "end": v(20.83, 55.56) * mm});
            skLineSegment(sketch, "E361", {"start": v(20.83, 55.56) * mm, "end": v(20.85, 55.74) * mm});
            skLineSegment(sketch, "E362", {"start": v(20.85, 55.74) * mm, "end": v(20.88, 55.93) * mm});
            skLineSegment(sketch, "E363", {"start": v(20.88, 55.93) * mm, "end": v(20.9, 56.13) * mm});
            skLineSegment(sketch, "E364", {"start": v(20.9, 56.13) * mm, "end": v(20.92, 56.34) * mm});
            skLineSegment(sketch, "E365", {"start": v(20.92, 56.34) * mm, "end": v(20.93, 56.56) * mm});
            skLineSegment(sketch, "E366", {"start": v(20.93, 56.56) * mm, "end": v(20.95, 56.8) * mm});
            skLineSegment(sketch, "E367", {"start": v(20.95, 56.8) * mm, "end": v(20.96, 57.04) * mm});
            skLineSegment(sketch, "E368", {"start": v(20.96, 57.04) * mm, "end": v(20.97, 57.3) * mm});
            skLineSegment(sketch, "E369", {"start": v(20.97, 57.3) * mm, "end": v(20.97, 57.56) * mm});
            skLineSegment(sketch, "E370", {"start": v(20.97, 57.56) * mm, "end": v(20.98, 57.84) * mm});
            skLineSegment(sketch, "E371", {"start": v(20.98, 57.84) * mm, "end": v(20.97, 58.12) * mm});
            skLineSegment(sketch, "E372", {"start": v(20.97, 58.12) * mm, "end": v(20.97, 58.42) * mm});
            skLineSegment(sketch, "E373", {"start": v(20.97, 58.42) * mm, "end": v(20.96, 58.72) * mm});
            skLineSegment(sketch, "E374", {"start": v(20.96, 58.72) * mm, "end": v(20.94, 59.04) * mm});
            skLineSegment(sketch, "E375", {"start": v(20.94, 59.04) * mm, "end": v(20.92, 59.37) * mm});
            skLineSegment(sketch, "E376", {"start": v(20.92, 59.37) * mm, "end": v(20.9, 59.7) * mm});
            skLineSegment(sketch, "E377", {"start": v(20.9, 59.7) * mm, "end": v(20.87, 60.05) * mm});
            skLineSegment(sketch, "E378", {"start": v(20.87, 60.05) * mm, "end": v(20.83, 60.4) * mm});
            skLineSegment(sketch, "E379", {"start": v(20.83, 60.4) * mm, "end": v(20.8, 60.77) * mm});
            skLineSegment(sketch, "E380", {"start": v(20.8, 60.77) * mm, "end": v(20.75, 61.15) * mm});
            skLineSegment(sketch, "E381", {"start": v(20.75, 61.15) * mm, "end": v(20.7, 61.54) * mm});
            skLineSegment(sketch, "E382", {"start": v(20.7, 61.54) * mm, "end": v(20.63, 61.93) * mm});
            skLineSegment(sketch, "E383", {"start": v(20.63, 61.93) * mm, "end": v(20.56, 62.34) * mm});
            skLineSegment(sketch, "E384", {"start": v(20.56, 62.34) * mm, "end": v(20.49, 62.75) * mm});
            skLineSegment(sketch, "E385", {"start": v(20.49, 62.75) * mm, "end": v(20.4, 63.18) * mm});
            skLineSegment(sketch, "E386", {"start": v(20.4, 63.18) * mm, "end": v(20.31, 63.6) * mm});
            skLineSegment(sketch, "E387", {"start": v(20.31, 63.6) * mm, "end": v(20.21, 64.05) * mm});
            skLineSegment(sketch, "E388", {"start": v(20.21, 64.05) * mm, "end": v(20.1, 64.5) * mm});
            skLineSegment(sketch, "E389", {"start": v(20.1, 64.5) * mm, "end": v(20, 64.96) * mm});
            skLineSegment(sketch, "E390", {"start": v(20, 64.96) * mm, "end": v(19.87, 65.43) * mm});
            skLineSegment(sketch, "E391", {"start": v(19.87, 65.43) * mm, "end": v(19.73, 65.9) * mm});
            skLineSegment(sketch, "E392", {"start": v(19.73, 65.9) * mm, "end": v(19.59, 66.39) * mm});
            skLineSegment(sketch, "E393", {"start": v(19.59, 66.39) * mm, "end": v(19.44, 66.88) * mm});
            skLineSegment(sketch, "E394", {"start": v(19.44, 66.88) * mm, "end": v(19.23, 67.24) * mm});
            skLineSegment(sketch, "E395", {"start": v(19.23, 67.24) * mm, "end": v(17.25, 67.78) * mm});
            skLineSegment(sketch, "E396", {"start": v(17.25, 67.78) * mm, "end": v(16.9, 67.57) * mm});
            skLineSegment(sketch, "E397", {"start": v(16.9, 67.57) * mm, "end": v(16.52, 67.22) * mm});
            skLineSegment(sketch, "E398", {"start": v(16.52, 67.22) * mm, "end": v(16.15, 66.87) * mm});
            skLineSegment(sketch, "E399", {"start": v(16.15, 66.87) * mm, "end": v(15.8, 66.53) * mm});
            skLineSegment(sketch, "E400", {"start": v(15.8, 66.53) * mm, "end": v(15.45, 66.19) * mm});
            skLineSegment(sketch, "E401", {"start": v(15.45, 66.19) * mm, "end": v(15.12, 65.85) * mm});
            skLineSegment(sketch, "E402", {"start": v(15.12, 65.85) * mm, "end": v(14.8, 65.52) * mm});
            skLineSegment(sketch, "E403", {"start": v(14.8, 65.52) * mm, "end": v(14.5, 65.18) * mm});
            skLineSegment(sketch, "E404", {"start": v(14.5, 65.18) * mm, "end": v(14.2, 64.85) * mm});
            skLineSegment(sketch, "E405", {"start": v(14.2, 64.85) * mm, "end": v(13.91, 64.53) * mm});
            skLineSegment(sketch, "E406", {"start": v(13.91, 64.53) * mm, "end": v(13.64, 64.2) * mm});
            skLineSegment(sketch, "E407", {"start": v(13.64, 64.2) * mm, "end": v(13.38, 63.9) * mm});
            skLineSegment(sketch, "E408", {"start": v(13.38, 63.9) * mm, "end": v(13.12, 63.58) * mm});
            skLineSegment(sketch, "E409", {"start": v(13.12, 63.58) * mm, "end": v(12.88, 63.28) * mm});
            skLineSegment(sketch, "E410", {"start": v(12.88, 63.28) * mm, "end": v(12.65, 62.98) * mm});
            skLineSegment(sketch, "E411", {"start": v(12.65, 62.98) * mm, "end": v(12.43, 62.68) * mm});
            skLineSegment(sketch, "E412", {"start": v(12.43, 62.68) * mm, "end": v(12.22, 62.39) * mm});
            skLineSegment(sketch, "E413", {"start": v(12.22, 62.39) * mm, "end": v(12.02, 62.1) * mm});
            skLineSegment(sketch, "E414", {"start": v(12.02, 62.1) * mm, "end": v(11.83, 61.83) * mm});
            skLineSegment(sketch, "E415", {"start": v(11.83, 61.83) * mm, "end": v(11.65, 61.55) * mm});
            skLineSegment(sketch, "E416", {"start": v(11.65, 61.55) * mm, "end": v(11.47, 61.29) * mm});
            skLineSegment(sketch, "E417", {"start": v(11.47, 61.29) * mm, "end": v(11.31, 61.03) * mm});
            skLineSegment(sketch, "E418", {"start": v(11.31, 61.03) * mm, "end": v(11.16, 60.77) * mm});
            skLineSegment(sketch, "E419", {"start": v(11.16, 60.77) * mm, "end": v(11.01, 60.53) * mm});
            skLineSegment(sketch, "E420", {"start": v(11.01, 60.53) * mm, "end": v(10.87, 60.29) * mm});
            skLineSegment(sketch, "E421", {"start": v(10.87, 60.29) * mm, "end": v(10.75, 60.06) * mm});
            skLineSegment(sketch, "E422", {"start": v(10.75, 60.06) * mm, "end": v(10.63, 59.83) * mm});
            skLineSegment(sketch, "E423", {"start": v(10.63, 59.83) * mm, "end": v(10.51, 59.62) * mm});
            skLineSegment(sketch, "E424", {"start": v(10.51, 59.62) * mm, "end": v(10.4, 59.4) * mm});
            skLineSegment(sketch, "E425", {"start": v(10.4, 59.4) * mm, "end": v(10.31, 59.2) * mm});
            skLineSegment(sketch, "E426", {"start": v(10.31, 59.2) * mm, "end": v(10.22, 59.01) * mm});
            skLineSegment(sketch, "E427", {"start": v(10.22, 59.01) * mm, "end": v(10.14, 58.83) * mm});
            skLineSegment(sketch, "E428", {"start": v(10.14, 58.83) * mm, "end": v(10.06, 58.65) * mm});
            skLineSegment(sketch, "E429", {"start": v(10.06, 58.65) * mm, "end": v(9.99, 58.49) * mm});
            skLineSegment(sketch, "E430", {"start": v(9.99, 58.49) * mm, "end": v(9.75, 58.39) * mm});
            skLineSegment(sketch, "E431", {"start": v(9.75, 58.39) * mm, "end": v(7.14, 58.77) * mm});
            skLineSegment(sketch, "E432", {"start": v(7.14, 58.77) * mm, "end": v(6.93, 58.93) * mm});
            skLineSegment(sketch, "E433", {"start": v(6.93, 58.93) * mm, "end": v(6.9, 59.1) * mm});
            skLineSegment(sketch, "E434", {"start": v(6.9, 59.1) * mm, "end": v(6.89, 59.3) * mm});
            skLineSegment(sketch, "E435", {"start": v(6.89, 59.3) * mm, "end": v(6.86, 59.5) * mm});
            skLineSegment(sketch, "E436", {"start": v(6.86, 59.5) * mm, "end": v(6.82, 59.7) * mm});
            skLineSegment(sketch, "E437", {"start": v(6.82, 59.7) * mm, "end": v(6.79, 59.93) * mm});
            skLineSegment(sketch, "E438", {"start": v(6.79, 59.93) * mm, "end": v(6.75, 60.16) * mm});
            skLineSegment(sketch, "E439", {"start": v(6.75, 60.16) * mm, "end": v(6.7, 60.4) * mm});
            skLineSegment(sketch, "E440", {"start": v(6.7, 60.4) * mm, "end": v(6.65, 60.65) * mm});
            skLineSegment(sketch, "E441", {"start": v(6.65, 60.65) * mm, "end": v(6.59, 60.9) * mm});
            skLineSegment(sketch, "E442", {"start": v(6.59, 60.9) * mm, "end": v(6.53, 61.17) * mm});
            skLineSegment(sketch, "E443", {"start": v(6.53, 61.17) * mm, "end": v(6.46, 61.45) * mm});
            skLineSegment(sketch, "E444", {"start": v(6.46, 61.45) * mm, "end": v(6.38, 61.74) * mm});
            skLineSegment(sketch, "E445", {"start": v(6.38, 61.74) * mm, "end": v(6.3, 62.03) * mm});
            skLineSegment(sketch, "E446", {"start": v(6.3, 62.03) * mm, "end": v(6.2, 62.34) * mm});
            skLineSegment(sketch, "E447", {"start": v(6.2, 62.34) * mm, "end": v(6.1, 62.65) * mm});
            skLineSegment(sketch, "E448", {"start": v(6.1, 62.65) * mm, "end": v(6, 62.97) * mm});
            skLineSegment(sketch, "E449", {"start": v(6, 62.97) * mm, "end": v(5.9, 63.3) * mm});
            skLineSegment(sketch, "E450", {"start": v(5.9, 63.3) * mm, "end": v(5.77, 63.64) * mm});
            skLineSegment(sketch, "E451", {"start": v(5.77, 63.64) * mm, "end": v(5.64, 63.98) * mm});
            skLineSegment(sketch, "E452", {"start": v(5.64, 63.98) * mm, "end": v(5.5, 64.34) * mm});
            skLineSegment(sketch, "E453", {"start": v(5.5, 64.34) * mm, "end": v(5.36, 64.7) * mm});
            skLineSegment(sketch, "E454", {"start": v(5.36, 64.7) * mm, "end": v(5.2, 65.07) * mm});
            skLineSegment(sketch, "E455", {"start": v(5.2, 65.07) * mm, "end": v(5.05, 65.45) * mm});
            skLineSegment(sketch, "E456", {"start": v(5.05, 65.45) * mm, "end": v(4.87, 65.83) * mm});
            skLineSegment(sketch, "E457", {"start": v(4.87, 65.83) * mm, "end": v(4.7, 66.22) * mm});
            skLineSegment(sketch, "E458", {"start": v(4.7, 66.22) * mm, "end": v(4.5, 66.62) * mm});
            skLineSegment(sketch, "E459", {"start": v(4.5, 66.62) * mm, "end": v(4.3, 67.03) * mm});
            skLineSegment(sketch, "E460", {"start": v(4.3, 67.03) * mm, "end": v(4.09, 67.44) * mm});
            skLineSegment(sketch, "E461", {"start": v(4.09, 67.44) * mm, "end": v(3.86, 67.86) * mm});
            skLineSegment(sketch, "E462", {"start": v(3.86, 67.86) * mm, "end": v(3.63, 68.28) * mm});
            skLineSegment(sketch, "E463", {"start": v(3.63, 68.28) * mm, "end": v(3.39, 68.71) * mm});
            skLineSegment(sketch, "E464", {"start": v(3.39, 68.71) * mm, "end": v(3.13, 69.15) * mm});
            skLineSegment(sketch, "E465", {"start": v(3.13, 69.15) * mm, "end": v(2.87, 69.59) * mm});
            skLineSegment(sketch, "E466", {"start": v(2.87, 69.59) * mm, "end": v(2.58, 69.89) * mm});
            skLineSegment(sketch, "E467", {"start": v(2.58, 69.89) * mm, "end": v(0.53, 69.93) * mm});
            skLineSegment(sketch, "E468", {"start": v(0.53, 69.93) * mm, "end": v(0.24, 69.65) * mm});
            skLineSegment(sketch, "E469", {"start": v(0.24, 69.65) * mm, "end": v(-0.05, 69.22) * mm});
            skLineSegment(sketch, "E470", {"start": v(-0.05, 69.22) * mm, "end": v(-0.32, 68.8) * mm});
            skLineSegment(sketch, "E471", {"start": v(-0.32, 68.8) * mm, "end": v(-0.59, 68.38) * mm});
            skLineSegment(sketch, "E472", {"start": v(-0.59, 68.38) * mm, "end": v(-0.84, 67.96) * mm});
            skLineSegment(sketch, "E473", {"start": v(-0.84, 67.96) * mm, "end": v(-1.08, 67.55) * mm});
            skLineSegment(sketch, "E474", {"start": v(-1.08, 67.55) * mm, "end": v(-1.3, 67.15) * mm});
            skLineSegment(sketch, "E475", {"start": v(-1.3, 67.15) * mm, "end": v(-1.53, 66.76) * mm});
            skLineSegment(sketch, "E476", {"start": v(-1.53, 66.76) * mm, "end": v(-1.74, 66.37) * mm});
            skLineSegment(sketch, "E477", {"start": v(-1.74, 66.37) * mm, "end": v(-1.94, 65.98) * mm});
            skLineSegment(sketch, "E478", {"start": v(-1.94, 65.98) * mm, "end": v(-2.13, 65.6) * mm});
            skLineSegment(sketch, "E479", {"start": v(-2.13, 65.6) * mm, "end": v(-2.3, 65.24) * mm});
            skLineSegment(sketch, "E480", {"start": v(-2.3, 65.24) * mm, "end": v(-2.48, 64.88) * mm});
            skLineSegment(sketch, "E481", {"start": v(-2.48, 64.88) * mm, "end": v(-2.64, 64.52) * mm});
            skLineSegment(sketch, "E482", {"start": v(-2.64, 64.52) * mm, "end": v(-2.79, 64.17) * mm});
            skLineSegment(sketch, "E483", {"start": v(-2.79, 64.17) * mm, "end": v(-2.93, 63.83) * mm});
            skLineSegment(sketch, "E484", {"start": v(-2.93, 63.83) * mm, "end": v(-3.07, 63.5) * mm});
            skLineSegment(sketch, "E485", {"start": v(-3.07, 63.5) * mm, "end": v(-3.2, 63.18) * mm});
            skLineSegment(sketch, "E486", {"start": v(-3.2, 63.18) * mm, "end": v(-3.31, 62.86) * mm});
            skLineSegment(sketch, "E487", {"start": v(-3.31, 62.86) * mm, "end": v(-3.42, 62.55) * mm});
            skLineSegment(sketch, "E488", {"start": v(-3.42, 62.55) * mm, "end": v(-3.53, 62.25) * mm});
            skLineSegment(sketch, "E489", {"start": v(-3.53, 62.25) * mm, "end": v(-3.62, 61.96) * mm});
            skLineSegment(sketch, "E490", {"start": v(-3.62, 61.96) * mm, "end": v(-3.71, 61.68) * mm});
            skLineSegment(sketch, "E491", {"start": v(-3.71, 61.68) * mm, "end": v(-3.8, 61.4) * mm});
            skLineSegment(sketch, "E492", {"start": v(-3.8, 61.4) * mm, "end": v(-3.87, 61.14) * mm});
            skLineSegment(sketch, "E493", {"start": v(-3.87, 61.14) * mm, "end": v(-3.94, 60.88) * mm});
            skLineSegment(sketch, "E494", {"start": v(-3.94, 60.88) * mm, "end": v(-4, 60.64) * mm});
            skLineSegment(sketch, "E495", {"start": v(-4, 60.64) * mm, "end": v(-4.06, 60.4) * mm});
            skLineSegment(sketch, "E496", {"start": v(-4.06, 60.4) * mm, "end": v(-4.11, 60.17) * mm});
            skLineSegment(sketch, "E497", {"start": v(-4.11, 60.17) * mm, "end": v(-4.16, 59.95) * mm});
            skLineSegment(sketch, "E498", {"start": v(-4.16, 59.95) * mm, "end": v(-4.2, 59.75) * mm});
            skLineSegment(sketch, "E499", {"start": v(-4.2, 59.75) * mm, "end": v(-4.24, 59.55) * mm});
            skLineSegment(sketch, "E500", {"start": v(-4.24, 59.55) * mm, "end": v(-4.27, 59.36) * mm});
            skLineSegment(sketch, "E501", {"start": v(-4.27, 59.36) * mm, "end": v(-4.3, 59.18) * mm});
            skLineSegment(sketch, "E502", {"start": v(-4.3, 59.18) * mm, "end": v(-4.51, 59.02) * mm});
            skLineSegment(sketch, "E503", {"start": v(-4.51, 59.02) * mm, "end": v(-7.14, 58.77) * mm});
            skLineSegment(sketch, "E504", {"start": v(-7.14, 58.77) * mm, "end": v(-7.37, 58.87) * mm});
            skLineSegment(sketch, "E505", {"start": v(-7.37, 58.87) * mm, "end": v(-7.44, 59.04) * mm});
            skLineSegment(sketch, "E506", {"start": v(-7.44, 59.04) * mm, "end": v(-7.5, 59.22) * mm});
            skLineSegment(sketch, "E507", {"start": v(-7.5, 59.22) * mm, "end": v(-7.58, 59.41) * mm});
            skLineSegment(sketch, "E508", {"start": v(-7.58, 59.41) * mm, "end": v(-7.66, 59.6) * mm});
            skLineSegment(sketch, "E509", {"start": v(-7.66, 59.6) * mm, "end": v(-7.75, 59.81) * mm});
            skLineSegment(sketch, "E510", {"start": v(-7.75, 59.81) * mm, "end": v(-7.85, 60.02) * mm});
            skLineSegment(sketch, "E511", {"start": v(-7.85, 60.02) * mm, "end": v(-7.95, 60.25) * mm});
            skLineSegment(sketch, "E512", {"start": v(-7.95, 60.25) * mm, "end": v(-8.06, 60.48) * mm});
            skLineSegment(sketch, "E513", {"start": v(-8.06, 60.48) * mm, "end": v(-8.18, 60.71) * mm});
            skLineSegment(sketch, "E514", {"start": v(-8.18, 60.71) * mm, "end": v(-8.3, 60.96) * mm});
            skLineSegment(sketch, "E515", {"start": v(-8.3, 60.96) * mm, "end": v(-8.44, 61.2) * mm});
            skLineSegment(sketch, "E516", {"start": v(-8.44, 61.2) * mm, "end": v(-8.58, 61.47) * mm});
            skLineSegment(sketch, "E517", {"start": v(-8.58, 61.47) * mm, "end": v(-8.73, 61.74) * mm});
            skLineSegment(sketch, "E518", {"start": v(-8.73, 61.74) * mm, "end": v(-8.9, 62.01) * mm});
            skLineSegment(sketch, "E519", {"start": v(-8.9, 62.01) * mm, "end": v(-9.06, 62.3) * mm});
            skLineSegment(sketch, "E520", {"start": v(-9.06, 62.3) * mm, "end": v(-9.24, 62.58) * mm});
            skLineSegment(sketch, "E521", {"start": v(-9.24, 62.58) * mm, "end": v(-9.43, 62.87) * mm});
            skLineSegment(sketch, "E522", {"start": v(-9.43, 62.87) * mm, "end": v(-9.63, 63.17) * mm});
            skLineSegment(sketch, "E523", {"start": v(-9.63, 63.17) * mm, "end": v(-9.83, 63.48) * mm});
            skLineSegment(sketch, "E524", {"start": v(-9.83, 63.48) * mm, "end": v(-10.05, 63.79) * mm});
            skLineSegment(sketch, "E525", {"start": v(-10.05, 63.79) * mm, "end": v(-10.28, 64.1) * mm});
            skLineSegment(sketch, "E526", {"start": v(-10.28, 64.1) * mm, "end": v(-10.52, 64.43) * mm});
            skLineSegment(sketch, "E527", {"start": v(-10.52, 64.43) * mm, "end": v(-10.76, 64.75) * mm});
            skLineSegment(sketch, "E528", {"start": v(-10.76, 64.75) * mm, "end": v(-11.02, 65.08) * mm});
            skLineSegment(sketch, "E529", {"start": v(-11.02, 65.08) * mm, "end": v(-11.3, 65.42) * mm});
            skLineSegment(sketch, "E530", {"start": v(-11.3, 65.42) * mm, "end": v(-11.58, 65.76) * mm});
            skLineSegment(sketch, "E531", {"start": v(-11.58, 65.76) * mm, "end": v(-11.87, 66.1) * mm});
            skLineSegment(sketch, "E532", {"start": v(-11.87, 66.1) * mm, "end": v(-12.17, 66.46) * mm});
            skLineSegment(sketch, "E533", {"start": v(-12.17, 66.46) * mm, "end": v(-12.49, 66.81) * mm});
            skLineSegment(sketch, "E534", {"start": v(-12.49, 66.81) * mm, "end": v(-12.82, 67.17) * mm});
            skLineSegment(sketch, "E535", {"start": v(-12.82, 67.17) * mm, "end": v(-13.16, 67.52) * mm});
            skLineSegment(sketch, "E536", {"start": v(-13.16, 67.52) * mm, "end": v(-13.5, 67.89) * mm});
            skLineSegment(sketch, "E537", {"start": v(-13.5, 67.89) * mm, "end": v(-13.87, 68.25) * mm});
            skLineSegment(sketch, "E538", {"start": v(-13.87, 68.25) * mm, "end": v(-14.22, 68.48) * mm});
            skLineSegment(sketch, "E539", {"start": v(-14.22, 68.48) * mm, "end": v(-16.22, 68.03) * mm});
            skLineSegment(sketch, "E540", {"start": v(-16.22, 68.03) * mm, "end": v(-16.44, 67.68) * mm});
            skLineSegment(sketch, "E541", {"start": v(-16.44, 67.68) * mm, "end": v(-16.61, 67.2) * mm});
            skLineSegment(sketch, "E542", {"start": v(-16.61, 67.2) * mm, "end": v(-16.78, 66.72) * mm});
            skLineSegment(sketch, "E543", {"start": v(-16.78, 66.72) * mm, "end": v(-16.93, 66.25) * mm});
            skLineSegment(sketch, "E544", {"start": v(-16.93, 66.25) * mm, "end": v(-17.08, 65.79) * mm});
            skLineSegment(sketch, "E545", {"start": v(-17.08, 65.79) * mm, "end": v(-17.21, 65.33) * mm});
            skLineSegment(sketch, "E546", {"start": v(-17.21, 65.33) * mm, "end": v(-17.34, 64.89) * mm});
            skLineSegment(sketch, "E547", {"start": v(-17.34, 64.89) * mm, "end": v(-17.46, 64.45) * mm});
            skLineSegment(sketch, "E548", {"start": v(-17.46, 64.45) * mm, "end": v(-17.57, 64.02) * mm});
            skLineSegment(sketch, "E549", {"start": v(-17.57, 64.02) * mm, "end": v(-17.67, 63.6) * mm});
            skLineSegment(sketch, "E550", {"start": v(-17.67, 63.6) * mm, "end": v(-17.76, 63.2) * mm});
            skLineSegment(sketch, "E551", {"start": v(-17.76, 63.2) * mm, "end": v(-17.85, 62.8) * mm});
            skLineSegment(sketch, "E552", {"start": v(-17.85, 62.8) * mm, "end": v(-17.93, 62.4) * mm});
            skLineSegment(sketch, "E553", {"start": v(-17.93, 62.4) * mm, "end": v(-18, 62.01) * mm});
            skLineSegment(sketch, "E554", {"start": v(-18, 62.01) * mm, "end": v(-18.07, 61.64) * mm});
            skLineSegment(sketch, "E555", {"start": v(-18.07, 61.64) * mm, "end": v(-18.12, 61.28) * mm});
            skLineSegment(sketch, "E556", {"start": v(-18.12, 61.28) * mm, "end": v(-18.17, 60.92) * mm});
            skLineSegment(sketch, "E557", {"start": v(-18.17, 60.92) * mm, "end": v(-18.22, 60.58) * mm});
            skLineSegment(sketch, "E558", {"start": v(-18.22, 60.58) * mm, "end": v(-18.26, 60.24) * mm});
            skLineSegment(sketch, "E559", {"start": v(-18.26, 60.24) * mm, "end": v(-18.3, 59.91) * mm});
            skLineSegment(sketch, "E560", {"start": v(-18.3, 59.91) * mm, "end": v(-18.32, 59.6) * mm});
            skLineSegment(sketch, "E561", {"start": v(-18.32, 59.6) * mm, "end": v(-18.35, 59.3) * mm});
            skLineSegment(sketch, "E562", {"start": v(-18.35, 59.3) * mm, "end": v(-18.36, 59) * mm});
            skLineSegment(sketch, "E563", {"start": v(-18.36, 59) * mm, "end": v(-18.38, 58.71) * mm});
            skLineSegment(sketch, "E564", {"start": v(-18.38, 58.71) * mm, "end": v(-18.39, 58.44) * mm});
            skLineSegment(sketch, "E565", {"start": v(-18.39, 58.44) * mm, "end": v(-18.4, 58.17) * mm});
            skLineSegment(sketch, "E566", {"start": v(-18.4, 58.17) * mm, "end": v(-18.4, 57.92) * mm});
            skLineSegment(sketch, "E567", {"start": v(-18.4, 57.92) * mm, "end": v(-18.4, 57.67) * mm});
            skLineSegment(sketch, "E568", {"start": v(-18.4, 57.67) * mm, "end": v(-18.4, 57.44) * mm});
            skLineSegment(sketch, "E569", {"start": v(-18.4, 57.44) * mm, "end": v(-18.39, 57.22) * mm});
            skLineSegment(sketch, "E570", {"start": v(-18.39, 57.22) * mm, "end": v(-18.38, 57) * mm});
            skLineSegment(sketch, "E571", {"start": v(-18.38, 57) * mm, "end": v(-18.36, 56.8) * mm});
            skLineSegment(sketch, "E572", {"start": v(-18.36, 56.8) * mm, "end": v(-18.35, 56.6) * mm});
            skLineSegment(sketch, "E573", {"start": v(-18.35, 56.6) * mm, "end": v(-18.34, 56.43) * mm});
            skLineSegment(sketch, "E574", {"start": v(-18.34, 56.43) * mm, "end": v(-18.5, 56.23) * mm});
            skLineSegment(sketch, "E575", {"start": v(-18.5, 56.23) * mm, "end": v(-21, 55.35) * mm});
            skLineSegment(sketch, "E576", {"start": v(-21, 55.35) * mm, "end": v(-21.25, 55.4) * mm});
            skLineSegment(sketch, "E577", {"start": v(-21.25, 55.4) * mm, "end": v(-21.35, 55.55) * mm});
            skLineSegment(sketch, "E578", {"start": v(-21.35, 55.55) * mm, "end": v(-21.46, 55.7) * mm});
            skLineSegment(sketch, "E579", {"start": v(-21.46, 55.7) * mm, "end": v(-21.58, 55.87) * mm});
            skLineSegment(sketch, "E580", {"start": v(-21.58, 55.87) * mm, "end": v(-21.7, 56.04) * mm});
            skLineSegment(sketch, "E581", {"start": v(-21.7, 56.04) * mm, "end": v(-21.84, 56.22) * mm});
            skLineSegment(sketch, "E582", {"start": v(-21.84, 56.22) * mm, "end": v(-21.98, 56.4) * mm});
            skLineSegment(sketch, "E583", {"start": v(-21.98, 56.4) * mm, "end": v(-22.14, 56.6) * mm});
            skLineSegment(sketch, "E584", {"start": v(-22.14, 56.6) * mm, "end": v(-22.3, 56.79) * mm});
            skLineSegment(sketch, "E585", {"start": v(-22.3, 56.79) * mm, "end": v(-22.47, 57) * mm});
            skLineSegment(sketch, "E586", {"start": v(-22.47, 57) * mm, "end": v(-22.65, 57.2) * mm});
            skLineSegment(sketch, "E587", {"start": v(-22.65, 57.2) * mm, "end": v(-22.84, 57.41) * mm});
            skLineSegment(sketch, "E588", {"start": v(-22.84, 57.41) * mm, "end": v(-23.04, 57.63) * mm});
            skLineSegment(sketch, "E589", {"start": v(-23.04, 57.63) * mm, "end": v(-23.25, 57.85) * mm});
            skLineSegment(sketch, "E590", {"start": v(-23.25, 57.85) * mm, "end": v(-23.47, 58.08) * mm});
            skLineSegment(sketch, "E591", {"start": v(-23.47, 58.08) * mm, "end": v(-23.7, 58.31) * mm});
            skLineSegment(sketch, "E592", {"start": v(-23.7, 58.31) * mm, "end": v(-23.95, 58.55) * mm});
            skLineSegment(sketch, "E593", {"start": v(-23.95, 58.55) * mm, "end": v(-24.2, 58.79) * mm});
            skLineSegment(sketch, "E594", {"start": v(-24.2, 58.79) * mm, "end": v(-24.46, 59.03) * mm});
            skLineSegment(sketch, "E595", {"start": v(-24.46, 59.03) * mm, "end": v(-24.74, 59.28) * mm});
            skLineSegment(sketch, "E596", {"start": v(-24.74, 59.28) * mm, "end": v(-25.02, 59.53) * mm});
            skLineSegment(sketch, "E597", {"start": v(-25.02, 59.53) * mm, "end": v(-25.32, 59.78) * mm});
            skLineSegment(sketch, "E598", {"start": v(-25.32, 59.78) * mm, "end": v(-25.63, 60.04) * mm});
            skLineSegment(sketch, "E599", {"start": v(-25.63, 60.04) * mm, "end": v(-25.95, 60.3) * mm});
            skLineSegment(sketch, "E600", {"start": v(-25.95, 60.3) * mm, "end": v(-26.28, 60.56) * mm});
            skLineSegment(sketch, "E601", {"start": v(-26.28, 60.56) * mm, "end": v(-26.62, 60.82) * mm});
            skLineSegment(sketch, "E602", {"start": v(-26.62, 60.82) * mm, "end": v(-26.98, 61.08) * mm});
            skLineSegment(sketch, "E603", {"start": v(-26.98, 61.08) * mm, "end": v(-27.34, 61.35) * mm});
            skLineSegment(sketch, "E604", {"start": v(-27.34, 61.35) * mm, "end": v(-27.72, 61.61) * mm});
            skLineSegment(sketch, "E605", {"start": v(-27.72, 61.61) * mm, "end": v(-28.11, 61.88) * mm});
            skLineSegment(sketch, "E606", {"start": v(-28.11, 61.88) * mm, "end": v(-28.52, 62.15) * mm});
            skLineSegment(sketch, "E607", {"start": v(-28.52, 62.15) * mm, "end": v(-28.93, 62.41) * mm});
            skLineSegment(sketch, "E608", {"start": v(-28.93, 62.41) * mm, "end": v(-29.36, 62.68) * mm});
            skLineSegment(sketch, "E609", {"start": v(-29.36, 62.68) * mm, "end": v(-29.8, 62.95) * mm});
            skLineSegment(sketch, "E610", {"start": v(-29.8, 62.95) * mm, "end": v(-30.2, 63.08) * mm});
            skLineSegment(sketch, "E611", {"start": v(-30.2, 63.08) * mm, "end": v(-32.03, 62.17) * mm});
            skLineSegment(sketch, "E612", {"start": v(-32.03, 62.17) * mm, "end": v(-32.16, 61.78) * mm});
            skLineSegment(sketch, "E613", {"start": v(-32.16, 61.78) * mm, "end": v(-32.2, 61.27) * mm});
            skLineSegment(sketch, "E614", {"start": v(-32.2, 61.27) * mm, "end": v(-32.26, 60.76) * mm});
            skLineSegment(sketch, "E615", {"start": v(-32.26, 60.76) * mm, "end": v(-32.3, 60.27) * mm});
            skLineSegment(sketch, "E616", {"start": v(-32.3, 60.27) * mm, "end": v(-32.33, 59.79) * mm});
            skLineSegment(sketch, "E617", {"start": v(-32.33, 59.79) * mm, "end": v(-32.35, 59.32) * mm});
            skLineSegment(sketch, "E618", {"start": v(-32.35, 59.32) * mm, "end": v(-32.37, 58.85) * mm});
            skLineSegment(sketch, "E619", {"start": v(-32.37, 58.85) * mm, "end": v(-32.38, 58.4) * mm});
            skLineSegment(sketch, "E620", {"start": v(-32.38, 58.4) * mm, "end": v(-32.38, 57.96) * mm});
            skLineSegment(sketch, "E621", {"start": v(-32.38, 57.96) * mm, "end": v(-32.38, 57.53) * mm});
            skLineSegment(sketch, "E622", {"start": v(-32.38, 57.53) * mm, "end": v(-32.37, 57.1) * mm});
            skLineSegment(sketch, "E623", {"start": v(-32.37, 57.1) * mm, "end": v(-32.36, 56.7) * mm});
            skLineSegment(sketch, "E624", {"start": v(-32.36, 56.7) * mm, "end": v(-32.34, 56.3) * mm});
            skLineSegment(sketch, "E625", {"start": v(-32.34, 56.3) * mm, "end": v(-32.32, 55.9) * mm});
            skLineSegment(sketch, "E626", {"start": v(-32.32, 55.9) * mm, "end": v(-32.3, 55.53) * mm});
            skLineSegment(sketch, "E627", {"start": v(-32.3, 55.53) * mm, "end": v(-32.26, 55.16) * mm});
            skLineSegment(sketch, "E628", {"start": v(-32.26, 55.16) * mm, "end": v(-32.23, 54.8) * mm});
            skLineSegment(sketch, "E629", {"start": v(-32.23, 54.8) * mm, "end": v(-32.19, 54.46) * mm});
            skLineSegment(sketch, "E630", {"start": v(-32.19, 54.46) * mm, "end": v(-32.15, 54.12) * mm});
            skLineSegment(sketch, "E631", {"start": v(-32.15, 54.12) * mm, "end": v(-32.1, 53.8) * mm});
            skLineSegment(sketch, "E632", {"start": v(-32.1, 53.8) * mm, "end": v(-32.05, 53.48) * mm});
            skLineSegment(sketch, "E633", {"start": v(-32.05, 53.48) * mm, "end": v(-32, 53.18) * mm});
            skLineSegment(sketch, "E634", {"start": v(-32, 53.18) * mm, "end": v(-31.95, 52.89) * mm});
            skLineSegment(sketch, "E635", {"start": v(-31.95, 52.89) * mm, "end": v(-31.9, 52.6) * mm});
            skLineSegment(sketch, "E636", {"start": v(-31.9, 52.6) * mm, "end": v(-31.84, 52.34) * mm});
            skLineSegment(sketch, "E637", {"start": v(-31.84, 52.34) * mm, "end": v(-31.78, 52.08) * mm});
            skLineSegment(sketch, "E638", {"start": v(-31.78, 52.08) * mm, "end": v(-31.72, 51.83) * mm});
            skLineSegment(sketch, "E639", {"start": v(-31.72, 51.83) * mm, "end": v(-31.66, 51.6) * mm});
            skLineSegment(sketch, "E640", {"start": v(-31.66, 51.6) * mm, "end": v(-31.6, 51.37) * mm});
            skLineSegment(sketch, "E641", {"start": v(-31.6, 51.37) * mm, "end": v(-31.54, 51.15) * mm});
            skLineSegment(sketch, "E642", {"start": v(-31.54, 51.15) * mm, "end": v(-31.48, 50.95) * mm});
            skLineSegment(sketch, "E643", {"start": v(-31.48, 50.95) * mm, "end": v(-31.42, 50.76) * mm});
            skLineSegment(sketch, "E644", {"start": v(-31.42, 50.76) * mm, "end": v(-31.37, 50.57) * mm});
            skLineSegment(sketch, "E645", {"start": v(-31.37, 50.57) * mm, "end": v(-31.3, 50.4) * mm});
            skLineSegment(sketch, "E646", {"start": v(-31.3, 50.4) * mm, "end": v(-31.43, 50.17) * mm});
            skLineSegment(sketch, "E647", {"start": v(-31.43, 50.17) * mm, "end": v(-33.63, 48.72) * mm});
            skLineSegment(sketch, "E648", {"start": v(-33.63, 48.72) * mm, "end": v(-33.89, 48.7) * mm});
            skLineSegment(sketch, "E649", {"start": v(-33.89, 48.7) * mm, "end": v(-34.02, 48.82) * mm});
            skLineSegment(sketch, "E650", {"start": v(-34.02, 48.82) * mm, "end": v(-34.17, 48.95) * mm});
            skLineSegment(sketch, "E651", {"start": v(-34.17, 48.95) * mm, "end": v(-34.32, 49.08) * mm});
            skLineSegment(sketch, "E652", {"start": v(-34.32, 49.08) * mm, "end": v(-34.49, 49.22) * mm});
            skLineSegment(sketch, "E653", {"start": v(-34.49, 49.22) * mm, "end": v(-34.66, 49.36) * mm});
            skLineSegment(sketch, "E654", {"start": v(-34.66, 49.36) * mm, "end": v(-34.84, 49.5) * mm});
            skLineSegment(sketch, "E655", {"start": v(-34.84, 49.5) * mm, "end": v(-35.04, 49.65) * mm});
            skLineSegment(sketch, "E656", {"start": v(-35.04, 49.65) * mm, "end": v(-35.24, 49.8) * mm});
            skLineSegment(sketch, "E657", {"start": v(-35.24, 49.8) * mm, "end": v(-35.46, 49.96) * mm});
            skLineSegment(sketch, "E658", {"start": v(-35.46, 49.96) * mm, "end": v(-35.68, 50.12) * mm});
            skLineSegment(sketch, "E659", {"start": v(-35.68, 50.12) * mm, "end": v(-35.92, 50.28) * mm});
            skLineSegment(sketch, "E660", {"start": v(-35.92, 50.28) * mm, "end": v(-36.17, 50.44) * mm});
            skLineSegment(sketch, "E661", {"start": v(-36.17, 50.44) * mm, "end": v(-36.42, 50.6) * mm});
            skLineSegment(sketch, "E662", {"start": v(-36.42, 50.6) * mm, "end": v(-36.7, 50.77) * mm});
            skLineSegment(sketch, "E663", {"start": v(-36.7, 50.77) * mm, "end": v(-36.97, 50.94) * mm});
            skLineSegment(sketch, "E664", {"start": v(-36.97, 50.94) * mm, "end": v(-37.26, 51.12) * mm});
            skLineSegment(sketch, "E665", {"start": v(-37.26, 51.12) * mm, "end": v(-37.57, 51.29) * mm});
            skLineSegment(sketch, "E666", {"start": v(-37.57, 51.29) * mm, "end": v(-37.88, 51.46) * mm});
            skLineSegment(sketch, "E667", {"start": v(-37.88, 51.46) * mm, "end": v(-38.2, 51.64) * mm});
            skLineSegment(sketch, "E668", {"start": v(-38.2, 51.64) * mm, "end": v(-38.54, 51.81) * mm});
            skLineSegment(sketch, "E669", {"start": v(-38.54, 51.81) * mm, "end": v(-38.9, 51.99) * mm});
            skLineSegment(sketch, "E670", {"start": v(-38.9, 51.99) * mm, "end": v(-39.25, 52.16) * mm});
            skLineSegment(sketch, "E671", {"start": v(-39.25, 52.16) * mm, "end": v(-39.62, 52.33) * mm});
            skLineSegment(sketch, "E672", {"start": v(-39.62, 52.33) * mm, "end": v(-40, 52.5) * mm});
            skLineSegment(sketch, "E673", {"start": v(-40, 52.5) * mm, "end": v(-40.4, 52.68) * mm});
            skLineSegment(sketch, "E674", {"start": v(-40.4, 52.68) * mm, "end": v(-40.81, 52.85) * mm});
            skLineSegment(sketch, "E675", {"start": v(-40.81, 52.85) * mm, "end": v(-41.23, 53.02) * mm});
            skLineSegment(sketch, "E676", {"start": v(-41.23, 53.02) * mm, "end": v(-41.66, 53.19) * mm});
            skLineSegment(sketch, "E677", {"start": v(-41.66, 53.19) * mm, "end": v(-42.1, 53.35) * mm});
            skLineSegment(sketch, "E678", {"start": v(-42.1, 53.35) * mm, "end": v(-42.56, 53.52) * mm});
            skLineSegment(sketch, "E679", {"start": v(-42.56, 53.52) * mm, "end": v(-43.03, 53.68) * mm});
            skLineSegment(sketch, "E680", {"start": v(-43.03, 53.68) * mm, "end": v(-43.5, 53.83) * mm});
            skLineSegment(sketch, "E681", {"start": v(-43.5, 53.83) * mm, "end": v(-44, 53.99) * mm});
            skLineSegment(sketch, "E682", {"start": v(-44, 53.99) * mm, "end": v(-44.41, 54.03) * mm});
            skLineSegment(sketch, "E683", {"start": v(-44.41, 54.03) * mm, "end": v(-45.98, 52.7) * mm});
            skLineSegment(sketch, "E684", {"start": v(-45.98, 52.7) * mm, "end": v(-46, 52.29) * mm});
            skLineSegment(sketch, "E685", {"start": v(-46, 52.29) * mm, "end": v(-45.94, 51.78) * mm});
            skLineSegment(sketch, "E686", {"start": v(-45.94, 51.78) * mm, "end": v(-45.86, 51.28) * mm});
            skLineSegment(sketch, "E687", {"start": v(-45.86, 51.28) * mm, "end": v(-45.78, 50.8) * mm});
            skLineSegment(sketch, "E688", {"start": v(-45.78, 50.8) * mm, "end": v(-45.7, 50.31) * mm});
            skLineSegment(sketch, "E689", {"start": v(-45.7, 50.31) * mm, "end": v(-45.6, 49.85) * mm});
            skLineSegment(sketch, "E690", {"start": v(-45.6, 49.85) * mm, "end": v(-45.5, 49.4) * mm});
            skLineSegment(sketch, "E691", {"start": v(-45.5, 49.4) * mm, "end": v(-45.41, 48.95) * mm});
            skLineSegment(sketch, "E692", {"start": v(-45.41, 48.95) * mm, "end": v(-45.31, 48.52) * mm});
            skLineSegment(sketch, "E693", {"start": v(-45.31, 48.52) * mm, "end": v(-45.2, 48.1) * mm});
            skLineSegment(sketch, "E694", {"start": v(-45.2, 48.1) * mm, "end": v(-45.1, 47.7) * mm});
            skLineSegment(sketch, "E695", {"start": v(-45.1, 47.7) * mm, "end": v(-44.99, 47.3) * mm});
            skLineSegment(sketch, "E696", {"start": v(-44.99, 47.3) * mm, "end": v(-44.87, 46.92) * mm});
            skLineSegment(sketch, "E697", {"start": v(-44.87, 46.92) * mm, "end": v(-44.76, 46.54) * mm});
            skLineSegment(sketch, "E698", {"start": v(-44.76, 46.54) * mm, "end": v(-44.64, 46.18) * mm});
            skLineSegment(sketch, "E699", {"start": v(-44.64, 46.18) * mm, "end": v(-44.52, 45.83) * mm});
            skLineSegment(sketch, "E700", {"start": v(-44.52, 45.83) * mm, "end": v(-44.4, 45.5) * mm});
            skLineSegment(sketch, "E701", {"start": v(-44.4, 45.5) * mm, "end": v(-44.28, 45.17) * mm});
            skLineSegment(sketch, "E702", {"start": v(-44.28, 45.17) * mm, "end": v(-44.16, 44.85) * mm});
            skLineSegment(sketch, "E703", {"start": v(-44.16, 44.85) * mm, "end": v(-44.04, 44.55) * mm});
            skLineSegment(sketch, "E704", {"start": v(-44.04, 44.55) * mm, "end": v(-43.92, 44.26) * mm});
            skLineSegment(sketch, "E705", {"start": v(-43.92, 44.26) * mm, "end": v(-43.8, 43.97) * mm});
            skLineSegment(sketch, "E706", {"start": v(-43.8, 43.97) * mm, "end": v(-43.68, 43.7) * mm});
            skLineSegment(sketch, "E707", {"start": v(-43.68, 43.7) * mm, "end": v(-43.56, 43.45) * mm});
            skLineSegment(sketch, "E708", {"start": v(-43.56, 43.45) * mm, "end": v(-43.44, 43.2) * mm});
            skLineSegment(sketch, "E709", {"start": v(-43.44, 43.2) * mm, "end": v(-43.32, 42.96) * mm});
            skLineSegment(sketch, "E710", {"start": v(-43.32, 42.96) * mm, "end": v(-43.2, 42.73) * mm});
            skLineSegment(sketch, "E711", {"start": v(-43.2, 42.73) * mm, "end": v(-43.1, 42.52) * mm});
            skLineSegment(sketch, "E712", {"start": v(-43.1, 42.52) * mm, "end": v(-42.98, 42.31) * mm});
            skLineSegment(sketch, "E713", {"start": v(-42.98, 42.31) * mm, "end": v(-42.87, 42.12) * mm});
            skLineSegment(sketch, "E714", {"start": v(-42.87, 42.12) * mm, "end": v(-42.76, 41.93) * mm});
            skLineSegment(sketch, "E715", {"start": v(-42.76, 41.93) * mm, "end": v(-42.66, 41.76) * mm});
            skLineSegment(sketch, "E716", {"start": v(-42.66, 41.76) * mm, "end": v(-42.56, 41.6) * mm});
            skLineSegment(sketch, "E717", {"start": v(-42.56, 41.6) * mm, "end": v(-42.46, 41.44) * mm});
            skLineSegment(sketch, "E718", {"start": v(-42.46, 41.44) * mm, "end": v(-42.52, 41.19) * mm});
            skLineSegment(sketch, "E719", {"start": v(-42.52, 41.19) * mm, "end": v(-44.3, 39.25) * mm});
            skLineSegment(sketch, "E720", {"start": v(-44.3, 39.25) * mm, "end": v(-44.56, 39.18) * mm});
            skLineSegment(sketch, "E721", {"start": v(-44.56, 39.18) * mm, "end": v(-44.72, 39.26) * mm});
            skLineSegment(sketch, "E722", {"start": v(-44.72, 39.26) * mm, "end": v(-44.9, 39.35) * mm});
            skLineSegment(sketch, "E723", {"start": v(-44.9, 39.35) * mm, "end": v(-45.07, 39.44) * mm});
            skLineSegment(sketch, "E724", {"start": v(-45.07, 39.44) * mm, "end": v(-45.26, 39.53) * mm});
            skLineSegment(sketch, "E725", {"start": v(-45.26, 39.53) * mm, "end": v(-45.46, 39.63) * mm});
            skLineSegment(sketch, "E726", {"start": v(-45.46, 39.63) * mm, "end": v(-45.68, 39.73) * mm});
            skLineSegment(sketch, "E727", {"start": v(-45.68, 39.73) * mm, "end": v(-45.9, 39.82) * mm});
            skLineSegment(sketch, "E728", {"start": v(-45.9, 39.82) * mm, "end": v(-46.14, 39.92) * mm});
            skLineSegment(sketch, "E729", {"start": v(-46.14, 39.92) * mm, "end": v(-46.38, 40.02) * mm});
            skLineSegment(sketch, "E730", {"start": v(-46.38, 40.02) * mm, "end": v(-46.64, 40.12) * mm});
            skLineSegment(sketch, "E731", {"start": v(-46.64, 40.12) * mm, "end": v(-46.9, 40.22) * mm});
            skLineSegment(sketch, "E732", {"start": v(-46.9, 40.22) * mm, "end": v(-47.19, 40.32) * mm});
            skLineSegment(sketch, "E733", {"start": v(-47.19, 40.32) * mm, "end": v(-47.48, 40.42) * mm});
            skLineSegment(sketch, "E734", {"start": v(-47.48, 40.42) * mm, "end": v(-47.78, 40.52) * mm});
            skLineSegment(sketch, "E735", {"start": v(-47.78, 40.52) * mm, "end": v(-48.09, 40.62) * mm});
            skLineSegment(sketch, "E736", {"start": v(-48.09, 40.62) * mm, "end": v(-48.41, 40.71) * mm});
            skLineSegment(sketch, "E737", {"start": v(-48.41, 40.71) * mm, "end": v(-48.75, 40.8) * mm});
            skLineSegment(sketch, "E738", {"start": v(-48.75, 40.8) * mm, "end": v(-49.1, 40.9) * mm});
            skLineSegment(sketch, "E739", {"start": v(-49.1, 40.9) * mm, "end": v(-49.45, 41) * mm});
            skLineSegment(sketch, "E740", {"start": v(-49.45, 41) * mm, "end": v(-49.82, 41.08) * mm});
            skLineSegment(sketch, "E741", {"start": v(-49.82, 41.08) * mm, "end": v(-50.2, 41.17) * mm});
            skLineSegment(sketch, "E742", {"start": v(-50.2, 41.17) * mm, "end": v(-50.6, 41.25) * mm});
            skLineSegment(sketch, "E743", {"start": v(-50.6, 41.25) * mm, "end": v(-51, 41.33) * mm});
            skLineSegment(sketch, "E744", {"start": v(-51, 41.33) * mm, "end": v(-51.41, 41.4) * mm});
            skLineSegment(sketch, "E745", {"start": v(-51.41, 41.4) * mm, "end": v(-51.84, 41.48) * mm});
            skLineSegment(sketch, "E746", {"start": v(-51.84, 41.48) * mm, "end": v(-52.27, 41.55) * mm});
            skLineSegment(sketch, "E747", {"start": v(-52.27, 41.55) * mm, "end": v(-52.72, 41.61) * mm});
            skLineSegment(sketch, "E748", {"start": v(-52.72, 41.61) * mm, "end": v(-53.18, 41.67) * mm});
            skLineSegment(sketch, "E749", {"start": v(-53.18, 41.67) * mm, "end": v(-53.65, 41.73) * mm});
            skLineSegment(sketch, "E750", {"start": v(-53.65, 41.73) * mm, "end": v(-54.13, 41.78) * mm});
            skLineSegment(sketch, "E751", {"start": v(-54.13, 41.78) * mm, "end": v(-54.62, 41.82) * mm});
            skLineSegment(sketch, "E752", {"start": v(-54.62, 41.82) * mm, "end": v(-55.13, 41.86) * mm});
            skLineSegment(sketch, "E753", {"start": v(-55.13, 41.86) * mm, "end": v(-55.64, 41.89) * mm});
            skLineSegment(sketch, "E754", {"start": v(-55.64, 41.89) * mm, "end": v(-56.05, 41.83) * mm});
            skLineSegment(sketch, "E755", {"start": v(-56.05, 41.83) * mm, "end": v(-57.25, 40.17) * mm});
            skLineSegment(sketch, "E756", {"start": v(-57.25, 40.17) * mm, "end": v(-57.19, 39.76) * mm});
            skLineSegment(sketch, "E757", {"start": v(-57.19, 39.76) * mm, "end": v(-57, 39.28) * mm});
            skLineSegment(sketch, "E758", {"start": v(-57, 39.28) * mm, "end": v(-56.8, 38.81) * mm});
            skLineSegment(sketch, "E759", {"start": v(-56.8, 38.81) * mm, "end": v(-56.6, 38.36) * mm});
            skLineSegment(sketch, "E760", {"start": v(-56.6, 38.36) * mm, "end": v(-56.4, 37.92) * mm});
            skLineSegment(sketch, "E761", {"start": v(-56.4, 37.92) * mm, "end": v(-56.2, 37.49) * mm});
            skLineSegment(sketch, "E762", {"start": v(-56.2, 37.49) * mm, "end": v(-56, 37.07) * mm});
            skLineSegment(sketch, "E763", {"start": v(-56, 37.07) * mm, "end": v(-55.8, 36.66) * mm});
            skLineSegment(sketch, "E764", {"start": v(-55.8, 36.66) * mm, "end": v(-55.6, 36.27) * mm});
            skLineSegment(sketch, "E765", {"start": v(-55.6, 36.27) * mm, "end": v(-55.4, 35.89) * mm});
            skLineSegment(sketch, "E766", {"start": v(-55.4, 35.89) * mm, "end": v(-55.2, 35.52) * mm});
            skLineSegment(sketch, "E767", {"start": v(-55.2, 35.52) * mm, "end": v(-55, 35.16) * mm});
            skLineSegment(sketch, "E768", {"start": v(-55, 35.16) * mm, "end": v(-54.8, 34.82) * mm});
            skLineSegment(sketch, "E769", {"start": v(-54.8, 34.82) * mm, "end": v(-54.6, 34.48) * mm});
            skLineSegment(sketch, "E770", {"start": v(-54.6, 34.48) * mm, "end": v(-54.4, 34.16) * mm});
            skLineSegment(sketch, "E771", {"start": v(-54.4, 34.16) * mm, "end": v(-54.2, 33.85) * mm});
            skLineSegment(sketch, "E772", {"start": v(-54.2, 33.85) * mm, "end": v(-54, 33.55) * mm});
            skLineSegment(sketch, "E773", {"start": v(-54, 33.55) * mm, "end": v(-53.8, 33.26) * mm});
            skLineSegment(sketch, "E774", {"start": v(-53.8, 33.26) * mm, "end": v(-53.61, 32.98) * mm});
            skLineSegment(sketch, "E775", {"start": v(-53.61, 32.98) * mm, "end": v(-53.42, 32.71) * mm});
            skLineSegment(sketch, "E776", {"start": v(-53.42, 32.71) * mm, "end": v(-53.24, 32.46) * mm});
            skLineSegment(sketch, "E777", {"start": v(-53.24, 32.46) * mm, "end": v(-53.05, 32.22) * mm});
            skLineSegment(sketch, "E778", {"start": v(-53.05, 32.22) * mm, "end": v(-52.87, 31.98) * mm});
            skLineSegment(sketch, "E779", {"start": v(-52.87, 31.98) * mm, "end": v(-52.69, 31.76) * mm});
            skLineSegment(sketch, "E780", {"start": v(-52.69, 31.76) * mm, "end": v(-52.51, 31.55) * mm});
            skLineSegment(sketch, "E781", {"start": v(-52.51, 31.55) * mm, "end": v(-52.34, 31.34) * mm});
            skLineSegment(sketch, "E782", {"start": v(-52.34, 31.34) * mm, "end": v(-52.18, 31.15) * mm});
            skLineSegment(sketch, "E783", {"start": v(-52.18, 31.15) * mm, "end": v(-52.01, 30.97) * mm});
            skLineSegment(sketch, "E784", {"start": v(-52.01, 30.97) * mm, "end": v(-51.86, 30.8) * mm});
            skLineSegment(sketch, "E785", {"start": v(-51.86, 30.8) * mm, "end": v(-51.7, 30.64) * mm});
            skLineSegment(sketch, "E786", {"start": v(-51.7, 30.64) * mm, "end": v(-51.55, 30.48) * mm});
            skLineSegment(sketch, "E787", {"start": v(-51.55, 30.48) * mm, "end": v(-51.41, 30.34) * mm});
            skLineSegment(sketch, "E788", {"start": v(-51.41, 30.34) * mm, "end": v(-51.28, 30.2) * mm});
            skLineSegment(sketch, "E789", {"start": v(-51.28, 30.2) * mm, "end": v(-51.14, 30.08) * mm});
            skLineSegment(sketch, "E790", {"start": v(-51.14, 30.08) * mm, "end": v(-51.14, 29.82) * mm});
            skLineSegment(sketch, "E791", {"start": v(-51.14, 29.82) * mm, "end": v(-52.42, 27.5) * mm});
            skLineSegment(sketch, "E792", {"start": v(-52.42, 27.5) * mm, "end": v(-52.64, 27.38) * mm});
            skLineSegment(sketch, "E793", {"start": v(-52.64, 27.38) * mm, "end": v(-52.82, 27.42) * mm});
            skLineSegment(sketch, "E794", {"start": v(-52.82, 27.42) * mm, "end": v(-53, 27.46) * mm});
            skLineSegment(sketch, "E795", {"start": v(-53, 27.46) * mm, "end": v(-53.2, 27.5) * mm});
            skLineSegment(sketch, "E796", {"start": v(-53.2, 27.5) * mm, "end": v(-53.4, 27.55) * mm});
            skLineSegment(sketch, "E797", {"start": v(-53.4, 27.55) * mm, "end": v(-53.63, 27.6) * mm});
            skLineSegment(sketch, "E798", {"start": v(-53.63, 27.6) * mm, "end": v(-53.86, 27.64) * mm});
            skLineSegment(sketch, "E799", {"start": v(-53.86, 27.64) * mm, "end": v(-54.1, 27.68) * mm});
            skLineSegment(sketch, "E800", {"start": v(-54.1, 27.68) * mm, "end": v(-54.35, 27.72) * mm});
            skLineSegment(sketch, "E801", {"start": v(-54.35, 27.72) * mm, "end": v(-54.61, 27.76) * mm});
            skLineSegment(sketch, "E802", {"start": v(-54.61, 27.76) * mm, "end": v(-54.88, 27.8) * mm});
            skLineSegment(sketch, "E803", {"start": v(-54.88, 27.8) * mm, "end": v(-55.17, 27.83) * mm});
            skLineSegment(sketch, "E804", {"start": v(-55.17, 27.83) * mm, "end": v(-55.46, 27.86) * mm});
            skLineSegment(sketch, "E805", {"start": v(-55.46, 27.86) * mm, "end": v(-55.77, 27.88) * mm});
            skLineSegment(sketch, "E806", {"start": v(-55.77, 27.88) * mm, "end": v(-56.08, 27.9) * mm});
            skLineSegment(sketch, "E807", {"start": v(-56.08, 27.9) * mm, "end": v(-56.41, 27.93) * mm});
            skLineSegment(sketch, "E808", {"start": v(-56.41, 27.93) * mm, "end": v(-56.75, 27.94) * mm});
            skLineSegment(sketch, "E809", {"start": v(-56.75, 27.94) * mm, "end": v(-57.1, 27.96) * mm});
            skLineSegment(sketch, "E810", {"start": v(-57.1, 27.96) * mm, "end": v(-57.46, 27.96) * mm});
            skLineSegment(sketch, "E811", {"start": v(-57.46, 27.96) * mm, "end": v(-57.83, 27.97) * mm});
            skLineSegment(sketch, "E812", {"start": v(-57.83, 27.97) * mm, "end": v(-58.2, 27.96) * mm});
            skLineSegment(sketch, "E813", {"start": v(-58.2, 27.96) * mm, "end": v(-58.6, 27.96) * mm});
            skLineSegment(sketch, "E814", {"start": v(-58.6, 27.96) * mm, "end": v(-59, 27.94) * mm});
            skLineSegment(sketch, "E815", {"start": v(-59, 27.94) * mm, "end": v(-59.4, 27.92) * mm});
            skLineSegment(sketch, "E816", {"start": v(-59.4, 27.92) * mm, "end": v(-59.83, 27.9) * mm});
            skLineSegment(sketch, "E817", {"start": v(-59.83, 27.9) * mm, "end": v(-60.26, 27.87) * mm});
            skLineSegment(sketch, "E818", {"start": v(-60.26, 27.87) * mm, "end": v(-60.7, 27.83) * mm});
            skLineSegment(sketch, "E819", {"start": v(-60.7, 27.83) * mm, "end": v(-61.15, 27.79) * mm});
            skLineSegment(sketch, "E820", {"start": v(-61.15, 27.79) * mm, "end": v(-61.6, 27.73) * mm});
            skLineSegment(sketch, "E821", {"start": v(-61.6, 27.73) * mm, "end": v(-62.08, 27.67) * mm});
            skLineSegment(sketch, "E822", {"start": v(-62.08, 27.67) * mm, "end": v(-62.56, 27.6) * mm});
            skLineSegment(sketch, "E823", {"start": v(-62.56, 27.6) * mm, "end": v(-63.05, 27.53) * mm});
            skLineSegment(sketch, "E824", {"start": v(-63.05, 27.53) * mm, "end": v(-63.54, 27.45) * mm});
            skLineSegment(sketch, "E825", {"start": v(-63.54, 27.45) * mm, "end": v(-64.05, 27.36) * mm});
            skLineSegment(sketch, "E826", {"start": v(-64.05, 27.36) * mm, "end": v(-64.43, 27.2) * mm});
            skLineSegment(sketch, "E827", {"start": v(-64.43, 27.2) * mm, "end": v(-65.2, 25.3) * mm});
            skLineSegment(sketch, "E828", {"start": v(-65.2, 25.3) * mm, "end": v(-65.04, 24.92) * mm});
            skLineSegment(sketch, "E829", {"start": v(-65.04, 24.92) * mm, "end": v(-64.74, 24.5) * mm});
            skLineSegment(sketch, "E830", {"start": v(-64.74, 24.5) * mm, "end": v(-64.44, 24.1) * mm});
            skLineSegment(sketch, "E831", {"start": v(-64.44, 24.1) * mm, "end": v(-64.14, 23.7) * mm});
            skLineSegment(sketch, "E832", {"start": v(-64.14, 23.7) * mm, "end": v(-63.84, 23.32) * mm});
            skLineSegment(sketch, "E833", {"start": v(-63.84, 23.32) * mm, "end": v(-63.55, 22.95) * mm});
            skLineSegment(sketch, "E834", {"start": v(-63.55, 22.95) * mm, "end": v(-63.25, 22.59) * mm});
            skLineSegment(sketch, "E835", {"start": v(-63.25, 22.59) * mm, "end": v(-62.96, 22.24) * mm});
            skLineSegment(sketch, "E836", {"start": v(-62.96, 22.24) * mm, "end": v(-62.67, 21.9) * mm});
            skLineSegment(sketch, "E837", {"start": v(-62.67, 21.9) * mm, "end": v(-62.38, 21.59) * mm});
            skLineSegment(sketch, "E838", {"start": v(-62.38, 21.59) * mm, "end": v(-62.1, 21.28) * mm});
            skLineSegment(sketch, "E839", {"start": v(-62.1, 21.28) * mm, "end": v(-61.82, 20.98) * mm});
            skLineSegment(sketch, "E840", {"start": v(-61.82, 20.98) * mm, "end": v(-61.54, 20.69) * mm});
            skLineSegment(sketch, "E841", {"start": v(-61.54, 20.69) * mm, "end": v(-61.26, 20.41) * mm});
            skLineSegment(sketch, "E842", {"start": v(-61.26, 20.41) * mm, "end": v(-61, 20.15) * mm});
            skLineSegment(sketch, "E843", {"start": v(-61, 20.15) * mm, "end": v(-60.72, 19.9) * mm});
            skLineSegment(sketch, "E844", {"start": v(-60.72, 19.9) * mm, "end": v(-60.46, 19.65) * mm});
            skLineSegment(sketch, "E845", {"start": v(-60.46, 19.65) * mm, "end": v(-60.2, 19.42) * mm});
            skLineSegment(sketch, "E846", {"start": v(-60.2, 19.42) * mm, "end": v(-59.95, 19.2) * mm});
            skLineSegment(sketch, "E847", {"start": v(-59.95, 19.2) * mm, "end": v(-59.7, 18.98) * mm});
            skLineSegment(sketch, "E848", {"start": v(-59.7, 18.98) * mm, "end": v(-59.46, 18.78) * mm});
            skLineSegment(sketch, "E849", {"start": v(-59.46, 18.78) * mm, "end": v(-59.22, 18.58) * mm});
            skLineSegment(sketch, "E850", {"start": v(-59.22, 18.58) * mm, "end": v(-58.98, 18.4) * mm});
            skLineSegment(sketch, "E851", {"start": v(-58.98, 18.4) * mm, "end": v(-58.76, 18.23) * mm});
            skLineSegment(sketch, "E852", {"start": v(-58.76, 18.23) * mm, "end": v(-58.54, 18.06) * mm});
            skLineSegment(sketch, "E853", {"start": v(-58.54, 18.06) * mm, "end": v(-58.32, 17.9) * mm});
            skLineSegment(sketch, "E854", {"start": v(-58.32, 17.9) * mm, "end": v(-58.11, 17.76) * mm});
            skLineSegment(sketch, "E855", {"start": v(-58.11, 17.76) * mm, "end": v(-57.91, 17.62) * mm});
            skLineSegment(sketch, "E856", {"start": v(-57.91, 17.62) * mm, "end": v(-57.72, 17.5) * mm});
            skLineSegment(sketch, "E857", {"start": v(-57.72, 17.5) * mm, "end": v(-57.53, 17.37) * mm});
            skLineSegment(sketch, "E858", {"start": v(-57.53, 17.37) * mm, "end": v(-57.35, 17.26) * mm});
            skLineSegment(sketch, "E859", {"start": v(-57.35, 17.26) * mm, "end": v(-57.18, 17.15) * mm});
            skLineSegment(sketch, "E860", {"start": v(-57.18, 17.15) * mm, "end": v(-57.01, 17.06) * mm});
            skLineSegment(sketch, "E861", {"start": v(-57.01, 17.06) * mm, "end": v(-56.86, 16.97) * mm});
            skLineSegment(sketch, "E862", {"start": v(-56.86, 16.97) * mm, "end": v(-56.79, 16.71) * mm});
            skLineSegment(sketch, "E863", {"start": v(-56.79, 16.71) * mm, "end": v(-57.48, 14.17) * mm});
            skLineSegment(sketch, "E864", {"start": v(-57.48, 14.17) * mm, "end": v(-57.66, 13.98) * mm});
            skLineSegment(sketch, "E865", {"start": v(-57.66, 13.98) * mm, "end": v(-57.84, 13.98) * mm});
            skLineSegment(sketch, "E866", {"start": v(-57.84, 13.98) * mm, "end": v(-58.04, 13.98) * mm});
            skLineSegment(sketch, "E867", {"start": v(-58.04, 13.98) * mm, "end": v(-58.24, 13.98) * mm});
            skLineSegment(sketch, "E868", {"start": v(-58.24, 13.98) * mm, "end": v(-58.45, 13.97) * mm});
            skLineSegment(sketch, "E869", {"start": v(-58.45, 13.97) * mm, "end": v(-58.67, 13.96) * mm});
            skLineSegment(sketch, "E870", {"start": v(-58.67, 13.96) * mm, "end": v(-58.9, 13.95) * mm});
            skLineSegment(sketch, "E871", {"start": v(-58.9, 13.95) * mm, "end": v(-59.15, 13.93) * mm});
            skLineSegment(sketch, "E872", {"start": v(-59.15, 13.93) * mm, "end": v(-59.4, 13.9) * mm});
            skLineSegment(sketch, "E873", {"start": v(-59.4, 13.9) * mm, "end": v(-59.67, 13.88) * mm});
            skLineSegment(sketch, "E874", {"start": v(-59.67, 13.88) * mm, "end": v(-59.94, 13.85) * mm});
            skLineSegment(sketch, "E875", {"start": v(-59.94, 13.85) * mm, "end": v(-60.22, 13.81) * mm});
            skLineSegment(sketch, "E876", {"start": v(-60.22, 13.81) * mm, "end": v(-60.52, 13.77) * mm});
            skLineSegment(sketch, "E877", {"start": v(-60.52, 13.77) * mm, "end": v(-60.82, 13.73) * mm});
            skLineSegment(sketch, "E878", {"start": v(-60.82, 13.73) * mm, "end": v(-61.13, 13.67) * mm});
            skLineSegment(sketch, "E879", {"start": v(-61.13, 13.67) * mm, "end": v(-61.46, 13.62) * mm});
            skLineSegment(sketch, "E880", {"start": v(-61.46, 13.62) * mm, "end": v(-61.79, 13.55) * mm});
            skLineSegment(sketch, "E881", {"start": v(-61.79, 13.55) * mm, "end": v(-62.13, 13.48) * mm});
            skLineSegment(sketch, "E882", {"start": v(-62.13, 13.48) * mm, "end": v(-62.48, 13.4) * mm});
            skLineSegment(sketch, "E883", {"start": v(-62.48, 13.4) * mm, "end": v(-62.84, 13.31) * mm});
            skLineSegment(sketch, "E884", {"start": v(-62.84, 13.31) * mm, "end": v(-63.2, 13.22) * mm});
            skLineSegment(sketch, "E885", {"start": v(-63.2, 13.22) * mm, "end": v(-63.58, 13.12) * mm});
            skLineSegment(sketch, "E886", {"start": v(-63.58, 13.12) * mm, "end": v(-63.97, 13.01) * mm});
            skLineSegment(sketch, "E887", {"start": v(-63.97, 13.01) * mm, "end": v(-64.36, 12.9) * mm});
            skLineSegment(sketch, "E888", {"start": v(-64.36, 12.9) * mm, "end": v(-64.77, 12.77) * mm});
            skLineSegment(sketch, "E889", {"start": v(-64.77, 12.77) * mm, "end": v(-65.18, 12.64) * mm});
            skLineSegment(sketch, "E890", {"start": v(-65.18, 12.64) * mm, "end": v(-65.6, 12.5) * mm});
            skLineSegment(sketch, "E891", {"start": v(-65.6, 12.5) * mm, "end": v(-66.02, 12.35) * mm});
            skLineSegment(sketch, "E892", {"start": v(-66.02, 12.35) * mm, "end": v(-66.46, 12.18) * mm});
            skLineSegment(sketch, "E893", {"start": v(-66.46, 12.18) * mm, "end": v(-66.9, 12.01) * mm});
            skLineSegment(sketch, "E894", {"start": v(-66.9, 12.01) * mm, "end": v(-67.35, 11.83) * mm});
            skLineSegment(sketch, "E895", {"start": v(-67.35, 11.83) * mm, "end": v(-67.8, 11.64) * mm});
            skLineSegment(sketch, "E896", {"start": v(-67.8, 11.64) * mm, "end": v(-68.27, 11.44) * mm});
            skLineSegment(sketch, "E897", {"start": v(-68.27, 11.44) * mm, "end": v(-68.74, 11.23) * mm});
            skLineSegment(sketch, "E898", {"start": v(-68.74, 11.23) * mm, "end": v(-69.07, 10.99) * mm});
            skLineSegment(sketch, "E899", {"start": v(-69.07, 10.99) * mm, "end": v(-69.36, 8.96) * mm});
            skLineSegment(sketch, "E900", {"start": v(-69.36, 8.96) * mm, "end": v(-69.11, 8.63) * mm});
            skLineSegment(sketch, "E901", {"start": v(-69.11, 8.63) * mm, "end": v(-68.72, 8.3) * mm});
            skLineSegment(sketch, "E902", {"start": v(-68.72, 8.3) * mm, "end": v(-68.33, 7.97) * mm});
            skLineSegment(sketch, "E903", {"start": v(-68.33, 7.97) * mm, "end": v(-67.95, 7.66) * mm});
            skLineSegment(sketch, "E904", {"start": v(-67.95, 7.66) * mm, "end": v(-67.57, 7.36) * mm});
            skLineSegment(sketch, "E905", {"start": v(-67.57, 7.36) * mm, "end": v(-67.2, 7.07) * mm});
            skLineSegment(sketch, "E906", {"start": v(-67.2, 7.07) * mm, "end": v(-66.82, 6.8) * mm});
            skLineSegment(sketch, "E907", {"start": v(-66.82, 6.8) * mm, "end": v(-66.45, 6.53) * mm});
            skLineSegment(sketch, "E908", {"start": v(-66.45, 6.53) * mm, "end": v(-66.1, 6.27) * mm});
            skLineSegment(sketch, "E909", {"start": v(-66.1, 6.27) * mm, "end": v(-65.74, 6.03) * mm});
            skLineSegment(sketch, "E910", {"start": v(-65.74, 6.03) * mm, "end": v(-65.39, 5.8) * mm});
            skLineSegment(sketch, "E911", {"start": v(-65.39, 5.8) * mm, "end": v(-65.04, 5.57) * mm});
            skLineSegment(sketch, "E912", {"start": v(-65.04, 5.57) * mm, "end": v(-64.7, 5.36) * mm});
            skLineSegment(sketch, "E913", {"start": v(-64.7, 5.36) * mm, "end": v(-64.37, 5.16) * mm});
            skLineSegment(sketch, "E914", {"start": v(-64.37, 5.16) * mm, "end": v(-64.04, 4.97) * mm});
            skLineSegment(sketch, "E915", {"start": v(-64.04, 4.97) * mm, "end": v(-63.72, 4.78) * mm});
            skLineSegment(sketch, "E916", {"start": v(-63.72, 4.78) * mm, "end": v(-63.4, 4.6) * mm});
            skLineSegment(sketch, "E917", {"start": v(-63.4, 4.6) * mm, "end": v(-63.1, 4.44) * mm});
            skLineSegment(sketch, "E918", {"start": v(-63.1, 4.44) * mm, "end": v(-62.8, 4.29) * mm});
            skLineSegment(sketch, "E919", {"start": v(-62.8, 4.29) * mm, "end": v(-62.5, 4.14) * mm});
            skLineSegment(sketch, "E920", {"start": v(-62.5, 4.14) * mm, "end": v(-62.22, 4) * mm});
            skLineSegment(sketch, "E921", {"start": v(-62.22, 4) * mm, "end": v(-61.94, 3.87) * mm});
            skLineSegment(sketch, "E922", {"start": v(-61.94, 3.87) * mm, "end": v(-61.68, 3.75) * mm});
            skLineSegment(sketch, "E923", {"start": v(-61.68, 3.75) * mm, "end": v(-61.41, 3.63) * mm});
            skLineSegment(sketch, "E924", {"start": v(-61.41, 3.63) * mm, "end": v(-61.16, 3.53) * mm});
            skLineSegment(sketch, "E925", {"start": v(-61.16, 3.53) * mm, "end": v(-60.91, 3.43) * mm});
            skLineSegment(sketch, "E926", {"start": v(-60.91, 3.43) * mm, "end": v(-60.68, 3.34) * mm});
            skLineSegment(sketch, "E927", {"start": v(-60.68, 3.34) * mm, "end": v(-60.45, 3.25) * mm});
            skLineSegment(sketch, "E928", {"start": v(-60.45, 3.25) * mm, "end": v(-60.23, 3.17) * mm});
            skLineSegment(sketch, "E929", {"start": v(-60.23, 3.17) * mm, "end": v(-60.02, 3.1) * mm});
            skLineSegment(sketch, "E930", {"start": v(-60.02, 3.1) * mm, "end": v(-59.81, 3.03) * mm});
            skLineSegment(sketch, "E931", {"start": v(-59.81, 3.03) * mm, "end": v(-59.62, 2.97) * mm});
            skLineSegment(sketch, "E932", {"start": v(-59.62, 2.97) * mm, "end": v(-59.44, 2.92) * mm});
            skLineSegment(sketch, "E933", {"start": v(-59.44, 2.92) * mm, "end": v(-59.26, 2.87) * mm});
            skLineSegment(sketch, "E934", {"start": v(-59.26, 2.87) * mm, "end": v(-59.14, 2.64) * mm});
            skLineSegment(sketch, "E935", {"start": v(-59.14, 2.64) * mm, "end": v(-59.2, 0) * mm});
            skLineSegment(sketch, "E936", {"start": v(-59.2, 0) * mm, "end": v(-59.33, -0.22) * mm});
            skLineSegment(sketch, "E937", {"start": v(-59.33, -0.22) * mm, "end": v(-59.5, -0.27) * mm});
            skLineSegment(sketch, "E938", {"start": v(-59.5, -0.27) * mm, "end": v(-59.7, -0.31) * mm});
            skLineSegment(sketch, "E939", {"start": v(-59.7, -0.31) * mm, "end": v(-59.9, -0.37) * mm});
            skLineSegment(sketch, "E940", {"start": v(-59.9, -0.37) * mm, "end": v(-60.1, -0.42) * mm});
            skLineSegment(sketch, "E941", {"start": v(-60.1, -0.42) * mm, "end": v(-60.31, -0.49) * mm});
            skLineSegment(sketch, "E942", {"start": v(-60.31, -0.49) * mm, "end": v(-60.53, -0.56) * mm});
            skLineSegment(sketch, "E943", {"start": v(-60.53, -0.56) * mm, "end": v(-60.76, -0.63) * mm});
            skLineSegment(sketch, "E944", {"start": v(-60.76, -0.63) * mm, "end": v(-61, -0.71) * mm});
            skLineSegment(sketch, "E945", {"start": v(-61, -0.71) * mm, "end": v(-61.26, -0.8) * mm});
            skLineSegment(sketch, "E946", {"start": v(-61.26, -0.8) * mm, "end": v(-61.51, -0.9) * mm});
            skLineSegment(sketch, "E947", {"start": v(-61.51, -0.9) * mm, "end": v(-61.78, -1) * mm});
            skLineSegment(sketch, "E948", {"start": v(-61.78, -1) * mm, "end": v(-62.06, -1.1) * mm});
            skLineSegment(sketch, "E949", {"start": v(-62.06, -1.1) * mm, "end": v(-62.34, -1.23) * mm});
            skLineSegment(sketch, "E950", {"start": v(-62.34, -1.23) * mm, "end": v(-62.63, -1.35) * mm});
            skLineSegment(sketch, "E951", {"start": v(-62.63, -1.35) * mm, "end": v(-62.93, -1.49) * mm});
            skLineSegment(sketch, "E952", {"start": v(-62.93, -1.49) * mm, "end": v(-63.23, -1.63) * mm});
            skLineSegment(sketch, "E953", {"start": v(-63.23, -1.63) * mm, "end": v(-63.55, -1.78) * mm});
            skLineSegment(sketch, "E954", {"start": v(-63.55, -1.78) * mm, "end": v(-63.87, -1.94) * mm});
            skLineSegment(sketch, "E955", {"start": v(-63.87, -1.94) * mm, "end": v(-64.2, -2.11) * mm});
            skLineSegment(sketch, "E956", {"start": v(-64.2, -2.11) * mm, "end": v(-64.53, -2.29) * mm});
            skLineSegment(sketch, "E957", {"start": v(-64.53, -2.29) * mm, "end": v(-64.88, -2.48) * mm});
            skLineSegment(sketch, "E958", {"start": v(-64.88, -2.48) * mm, "end": v(-65.22, -2.67) * mm});
            skLineSegment(sketch, "E959", {"start": v(-65.22, -2.67) * mm, "end": v(-65.58, -2.88) * mm});
            skLineSegment(sketch, "E960", {"start": v(-65.58, -2.88) * mm, "end": v(-65.94, -3.1) * mm});
            skLineSegment(sketch, "E961", {"start": v(-65.94, -3.1) * mm, "end": v(-66.3, -3.33) * mm});
            skLineSegment(sketch, "E962", {"start": v(-66.3, -3.33) * mm, "end": v(-66.68, -3.56) * mm});
            skLineSegment(sketch, "E963", {"start": v(-66.68, -3.56) * mm, "end": v(-67.06, -3.81) * mm});
            skLineSegment(sketch, "E964", {"start": v(-67.06, -3.81) * mm, "end": v(-67.44, -4.07) * mm});
            skLineSegment(sketch, "E965", {"start": v(-67.44, -4.07) * mm, "end": v(-67.83, -4.34) * mm});
            skLineSegment(sketch, "E966", {"start": v(-67.83, -4.34) * mm, "end": v(-68.22, -4.63) * mm});
            skLineSegment(sketch, "E967", {"start": v(-68.22, -4.63) * mm, "end": v(-68.62, -4.92) * mm});
            skLineSegment(sketch, "E968", {"start": v(-68.62, -4.92) * mm, "end": v(-69.02, -5.23) * mm});
            skLineSegment(sketch, "E969", {"start": v(-69.02, -5.23) * mm, "end": v(-69.43, -5.54) * mm});
            skLineSegment(sketch, "E970", {"start": v(-69.43, -5.54) * mm, "end": v(-69.7, -5.86) * mm});
            skLineSegment(sketch, "E971", {"start": v(-69.7, -5.86) * mm, "end": v(-69.49, -7.9) * mm});
            skLineSegment(sketch, "E972", {"start": v(-69.49, -7.9) * mm, "end": v(-69.17, -8.16) * mm});
            skLineSegment(sketch, "E973", {"start": v(-69.17, -8.16) * mm, "end": v(-68.7, -8.4) * mm});
            skLineSegment(sketch, "E974", {"start": v(-68.7, -8.4) * mm, "end": v(-68.25, -8.61) * mm});
            skLineSegment(sketch, "E975", {"start": v(-68.25, -8.61) * mm, "end": v(-67.8, -8.82) * mm});
            skLineSegment(sketch, "E976", {"start": v(-67.8, -8.82) * mm, "end": v(-67.37, -9.02) * mm});
            skLineSegment(sketch, "E977", {"start": v(-67.37, -9.02) * mm, "end": v(-66.93, -9.21) * mm});
            skLineSegment(sketch, "E978", {"start": v(-66.93, -9.21) * mm, "end": v(-66.5, -9.4) * mm});
            skLineSegment(sketch, "E979", {"start": v(-66.5, -9.4) * mm, "end": v(-66.09, -9.56) * mm});
            skLineSegment(sketch, "E980", {"start": v(-66.09, -9.56) * mm, "end": v(-65.67, -9.72) * mm});
            skLineSegment(sketch, "E981", {"start": v(-65.67, -9.72) * mm, "end": v(-65.27, -9.88) * mm});
            skLineSegment(sketch, "E982", {"start": v(-65.27, -9.88) * mm, "end": v(-64.87, -10.02) * mm});
            skLineSegment(sketch, "E983", {"start": v(-64.87, -10.02) * mm, "end": v(-64.48, -10.15) * mm});
            skLineSegment(sketch, "E984", {"start": v(-64.48, -10.15) * mm, "end": v(-64.1, -10.28) * mm});
            skLineSegment(sketch, "E985", {"start": v(-64.1, -10.28) * mm, "end": v(-63.73, -10.4) * mm});
            skLineSegment(sketch, "E986", {"start": v(-63.73, -10.4) * mm, "end": v(-63.37, -10.5) * mm});
            skLineSegment(sketch, "E987", {"start": v(-63.37, -10.5) * mm, "end": v(-63.01, -10.6) * mm});
            skLineSegment(sketch, "E988", {"start": v(-63.01, -10.6) * mm, "end": v(-62.67, -10.7) * mm});
            skLineSegment(sketch, "E989", {"start": v(-62.67, -10.7) * mm, "end": v(-62.33, -10.79) * mm});
            skLineSegment(sketch, "E990", {"start": v(-62.33, -10.79) * mm, "end": v(-62, -10.87) * mm});
            skLineSegment(sketch, "E991", {"start": v(-62, -10.87) * mm, "end": v(-61.68, -10.94) * mm});
            skLineSegment(sketch, "E992", {"start": v(-61.68, -10.94) * mm, "end": v(-61.37, -11) * mm});
            skLineSegment(sketch, "E993", {"start": v(-61.37, -11) * mm, "end": v(-61.07, -11.07) * mm});
            skLineSegment(sketch, "E994", {"start": v(-61.07, -11.07) * mm, "end": v(-60.78, -11.12) * mm});
            skLineSegment(sketch, "E995", {"start": v(-60.78, -11.12) * mm, "end": v(-60.5, -11.17) * mm});
            skLineSegment(sketch, "E996", {"start": v(-60.5, -11.17) * mm, "end": v(-60.23, -11.21) * mm});
            skLineSegment(sketch, "E997", {"start": v(-60.23, -11.21) * mm, "end": v(-59.96, -11.25) * mm});
            skLineSegment(sketch, "E998", {"start": v(-59.96, -11.25) * mm, "end": v(-59.71, -11.28) * mm});
            skLineSegment(sketch, "E999", {"start": v(-59.71, -11.28) * mm, "end": v(-59.47, -11.31) * mm});
            skLineSegment(sketch, "E1000", {"start": v(-59.47, -11.31) * mm, "end": v(-59.24, -11.33) * mm});
            skLineSegment(sketch, "E1001", {"start": v(-59.24, -11.33) * mm, "end": v(-59.02, -11.36) * mm});
            skLineSegment(sketch, "E1002", {"start": v(-59.02, -11.36) * mm, "end": v(-58.8, -11.37) * mm});
            skLineSegment(sketch, "E1003", {"start": v(-58.8, -11.37) * mm, "end": v(-58.6, -11.38) * mm});
            skLineSegment(sketch, "E1004", {"start": v(-58.6, -11.38) * mm, "end": v(-58.4, -11.4) * mm});
            skLineSegment(sketch, "E1005", {"start": v(-58.4, -11.4) * mm, "end": v(-58.23, -11.4) * mm});
            skLineSegment(sketch, "E1006", {"start": v(-58.23, -11.4) * mm, "end": v(-58.05, -11.6) * mm});
            skLineSegment(sketch, "E1007", {"start": v(-58.05, -11.6) * mm, "end": v(-57.48, -14.17) * mm});
            skLineSegment(sketch, "E1008", {"start": v(-57.48, -14.17) * mm, "end": v(-57.56, -14.42) * mm});
            skLineSegment(sketch, "E1009", {"start": v(-57.56, -14.42) * mm, "end": v(-57.72, -14.5) * mm});
            skLineSegment(sketch, "E1010", {"start": v(-57.72, -14.5) * mm, "end": v(-57.89, -14.59) * mm});
            skLineSegment(sketch, "E1011", {"start": v(-57.89, -14.59) * mm, "end": v(-58.06, -14.69) * mm});
            skLineSegment(sketch, "E1012", {"start": v(-58.06, -14.69) * mm, "end": v(-58.25, -14.8) * mm});
            skLineSegment(sketch, "E1013", {"start": v(-58.25, -14.8) * mm, "end": v(-58.44, -14.9) * mm});
            skLineSegment(sketch, "E1014", {"start": v(-58.44, -14.9) * mm, "end": v(-58.64, -15.03) * mm});
            skLineSegment(sketch, "E1015", {"start": v(-58.64, -15.03) * mm, "end": v(-58.85, -15.15) * mm});
            skLineSegment(sketch, "E1016", {"start": v(-58.85, -15.15) * mm, "end": v(-59.06, -15.3) * mm});
            skLineSegment(sketch, "E1017", {"start": v(-59.06, -15.3) * mm, "end": v(-59.28, -15.44) * mm});
            skLineSegment(sketch, "E1018", {"start": v(-59.28, -15.44) * mm, "end": v(-59.51, -15.6) * mm});
            skLineSegment(sketch, "E1019", {"start": v(-59.51, -15.6) * mm, "end": v(-59.75, -15.75) * mm});
            skLineSegment(sketch, "E1020", {"start": v(-59.75, -15.75) * mm, "end": v(-59.99, -15.93) * mm});
            skLineSegment(sketch, "E1021", {"start": v(-59.99, -15.93) * mm, "end": v(-60.23, -16.11) * mm});
            skLineSegment(sketch, "E1022", {"start": v(-60.23, -16.11) * mm, "end": v(-60.49, -16.3) * mm});
            skLineSegment(sketch, "E1023", {"start": v(-60.49, -16.3) * mm, "end": v(-60.75, -16.5) * mm});
            skLineSegment(sketch, "E1024", {"start": v(-60.75, -16.5) * mm, "end": v(-61, -16.72) * mm});
            skLineSegment(sketch, "E1025", {"start": v(-61, -16.72) * mm, "end": v(-61.28, -16.94) * mm});
            skLineSegment(sketch, "E1026", {"start": v(-61.28, -16.94) * mm, "end": v(-61.55, -17.17) * mm});
            skLineSegment(sketch, "E1027", {"start": v(-61.55, -17.17) * mm, "end": v(-61.83, -17.41) * mm});
            skLineSegment(sketch, "E1028", {"start": v(-61.83, -17.41) * mm, "end": v(-62.11, -17.67) * mm});
            skLineSegment(sketch, "E1029", {"start": v(-62.11, -17.67) * mm, "end": v(-62.4, -17.93) * mm});
            skLineSegment(sketch, "E1030", {"start": v(-62.4, -17.93) * mm, "end": v(-62.69, -18.2) * mm});
            skLineSegment(sketch, "E1031", {"start": v(-62.69, -18.2) * mm, "end": v(-62.98, -18.5) * mm});
            skLineSegment(sketch, "E1032", {"start": v(-62.98, -18.5) * mm, "end": v(-63.28, -18.79) * mm});
            skLineSegment(sketch, "E1033", {"start": v(-63.28, -18.79) * mm, "end": v(-63.58, -19.1) * mm});
            skLineSegment(sketch, "E1034", {"start": v(-63.58, -19.1) * mm, "end": v(-63.89, -19.42) * mm});
            skLineSegment(sketch, "E1035", {"start": v(-63.89, -19.42) * mm, "end": v(-64.2, -19.75) * mm});
            skLineSegment(sketch, "E1036", {"start": v(-64.2, -19.75) * mm, "end": v(-64.5, -20.1) * mm});
            skLineSegment(sketch, "E1037", {"start": v(-64.5, -20.1) * mm, "end": v(-64.82, -20.45) * mm});
            skLineSegment(sketch, "E1038", {"start": v(-64.82, -20.45) * mm, "end": v(-65.13, -20.82) * mm});
            skLineSegment(sketch, "E1039", {"start": v(-65.13, -20.82) * mm, "end": v(-65.45, -21.2) * mm});
            skLineSegment(sketch, "E1040", {"start": v(-65.45, -21.2) * mm, "end": v(-65.76, -21.6) * mm});
            skLineSegment(sketch, "E1041", {"start": v(-65.76, -21.6) * mm, "end": v(-66.08, -22) * mm});
            skLineSegment(sketch, "E1042", {"start": v(-66.08, -22) * mm, "end": v(-66.26, -22.37) * mm});
            skLineSegment(sketch, "E1043", {"start": v(-66.26, -22.37) * mm, "end": v(-65.58, -24.3) * mm});
            skLineSegment(sketch, "E1044", {"start": v(-65.58, -24.3) * mm, "end": v(-65.2, -24.48) * mm});
            skLineSegment(sketch, "E1045", {"start": v(-65.2, -24.48) * mm, "end": v(-64.7, -24.6) * mm});
            skLineSegment(sketch, "E1046", {"start": v(-64.7, -24.6) * mm, "end": v(-64.2, -24.7) * mm});
            skLineSegment(sketch, "E1047", {"start": v(-64.2, -24.7) * mm, "end": v(-63.72, -24.8) * mm});
            skLineSegment(sketch, "E1048", {"start": v(-63.72, -24.8) * mm, "end": v(-63.25, -24.88) * mm});
            skLineSegment(sketch, "E1049", {"start": v(-63.25, -24.88) * mm, "end": v(-62.78, -24.96) * mm});
            skLineSegment(sketch, "E1050", {"start": v(-62.78, -24.96) * mm, "end": v(-62.32, -25.04) * mm});
            skLineSegment(sketch, "E1051", {"start": v(-62.32, -25.04) * mm, "end": v(-61.88, -25.1) * mm});
            skLineSegment(sketch, "E1052", {"start": v(-61.88, -25.1) * mm, "end": v(-61.44, -25.16) * mm});
            skLineSegment(sketch, "E1053", {"start": v(-61.44, -25.16) * mm, "end": v(-61, -25.2) * mm});
            skLineSegment(sketch, "E1054", {"start": v(-61, -25.2) * mm, "end": v(-60.6, -25.25) * mm});
            skLineSegment(sketch, "E1055", {"start": v(-60.6, -25.25) * mm, "end": v(-60.18, -25.29) * mm});
            skLineSegment(sketch, "E1056", {"start": v(-60.18, -25.29) * mm, "end": v(-59.78, -25.32) * mm});
            skLineSegment(sketch, "E1057", {"start": v(-59.78, -25.32) * mm, "end": v(-59.4, -25.35) * mm});
            skLineSegment(sketch, "E1058", {"start": v(-59.4, -25.35) * mm, "end": v(-59.01, -25.36) * mm});
            skLineSegment(sketch, "E1059", {"start": v(-59.01, -25.36) * mm, "end": v(-58.64, -25.38) * mm});
            skLineSegment(sketch, "E1060", {"start": v(-58.64, -25.38) * mm, "end": v(-58.29, -25.39) * mm});
            skLineSegment(sketch, "E1061", {"start": v(-58.29, -25.39) * mm, "end": v(-57.94, -25.39) * mm});
            skLineSegment(sketch, "E1062", {"start": v(-57.94, -25.39) * mm, "end": v(-57.6, -25.39) * mm});
            skLineSegment(sketch, "E1063", {"start": v(-57.6, -25.39) * mm, "end": v(-57.27, -25.38) * mm});
            skLineSegment(sketch, "E1064", {"start": v(-57.27, -25.38) * mm, "end": v(-56.96, -25.37) * mm});
            skLineSegment(sketch, "E1065", {"start": v(-56.96, -25.37) * mm, "end": v(-56.65, -25.36) * mm});
            skLineSegment(sketch, "E1066", {"start": v(-56.65, -25.36) * mm, "end": v(-56.35, -25.34) * mm});
            skLineSegment(sketch, "E1067", {"start": v(-56.35, -25.34) * mm, "end": v(-56.07, -25.32) * mm});
            skLineSegment(sketch, "E1068", {"start": v(-56.07, -25.32) * mm, "end": v(-55.8, -25.3) * mm});
            skLineSegment(sketch, "E1069", {"start": v(-55.8, -25.3) * mm, "end": v(-55.53, -25.27) * mm});
            skLineSegment(sketch, "E1070", {"start": v(-55.53, -25.27) * mm, "end": v(-55.28, -25.24) * mm});
            skLineSegment(sketch, "E1071", {"start": v(-55.28, -25.24) * mm, "end": v(-55.04, -25.21) * mm});
            skLineSegment(sketch, "E1072", {"start": v(-55.04, -25.21) * mm, "end": v(-54.8, -25.18) * mm});
            skLineSegment(sketch, "E1073", {"start": v(-54.8, -25.18) * mm, "end": v(-54.58, -25.15) * mm});
            skLineSegment(sketch, "E1074", {"start": v(-54.58, -25.15) * mm, "end": v(-54.37, -25.11) * mm});
            skLineSegment(sketch, "E1075", {"start": v(-54.37, -25.11) * mm, "end": v(-54.17, -25.08) * mm});
            skLineSegment(sketch, "E1076", {"start": v(-54.17, -25.08) * mm, "end": v(-53.99, -25.04) * mm});
            skLineSegment(sketch, "E1077", {"start": v(-53.99, -25.04) * mm, "end": v(-53.8, -25) * mm});
            skLineSegment(sketch, "E1078", {"start": v(-53.8, -25) * mm, "end": v(-53.59, -25.15) * mm});
            skLineSegment(sketch, "E1079", {"start": v(-53.59, -25.15) * mm, "end": v(-52.42, -27.51) * mm});
            skLineSegment(sketch, "E1080", {"start": v(-52.42, -27.51) * mm, "end": v(-52.43, -27.77) * mm});
            skLineSegment(sketch, "E1081", {"start": v(-52.43, -27.77) * mm, "end": v(-52.57, -27.9) * mm});
            skLineSegment(sketch, "E1082", {"start": v(-52.57, -27.9) * mm, "end": v(-52.71, -28.02) * mm});
            skLineSegment(sketch, "E1083", {"start": v(-52.71, -28.02) * mm, "end": v(-52.86, -28.16) * mm});
            skLineSegment(sketch, "E1084", {"start": v(-52.86, -28.16) * mm, "end": v(-53.02, -28.3) * mm});
            skLineSegment(sketch, "E1085", {"start": v(-53.02, -28.3) * mm, "end": v(-53.18, -28.46) * mm});
            skLineSegment(sketch, "E1086", {"start": v(-53.18, -28.46) * mm, "end": v(-53.34, -28.62) * mm});
            skLineSegment(sketch, "E1087", {"start": v(-53.34, -28.62) * mm, "end": v(-53.51, -28.8) * mm});
            skLineSegment(sketch, "E1088", {"start": v(-53.51, -28.8) * mm, "end": v(-53.69, -28.98) * mm});
            skLineSegment(sketch, "E1089", {"start": v(-53.69, -28.98) * mm, "end": v(-53.87, -29.18) * mm});
            skLineSegment(sketch, "E1090", {"start": v(-53.87, -29.18) * mm, "end": v(-54.05, -29.38) * mm});
            skLineSegment(sketch, "E1091", {"start": v(-54.05, -29.38) * mm, "end": v(-54.24, -29.6) * mm});
            skLineSegment(sketch, "E1092", {"start": v(-54.24, -29.6) * mm, "end": v(-54.43, -29.82) * mm});
            skLineSegment(sketch, "E1093", {"start": v(-54.43, -29.82) * mm, "end": v(-54.63, -30.06) * mm});
            skLineSegment(sketch, "E1094", {"start": v(-54.63, -30.06) * mm, "end": v(-54.83, -30.3) * mm});
            skLineSegment(sketch, "E1095", {"start": v(-54.83, -30.3) * mm, "end": v(-55.03, -30.56) * mm});
            skLineSegment(sketch, "E1096", {"start": v(-55.03, -30.56) * mm, "end": v(-55.23, -30.83) * mm});
            skLineSegment(sketch, "E1097", {"start": v(-55.23, -30.83) * mm, "end": v(-55.44, -31.11) * mm});
            skLineSegment(sketch, "E1098", {"start": v(-55.44, -31.11) * mm, "end": v(-55.65, -31.4) * mm});
            skLineSegment(sketch, "E1099", {"start": v(-55.65, -31.4) * mm, "end": v(-55.86, -31.7) * mm});
            skLineSegment(sketch, "E1100", {"start": v(-55.86, -31.7) * mm, "end": v(-56.08, -32.02) * mm});
            skLineSegment(sketch, "E1101", {"start": v(-56.08, -32.02) * mm, "end": v(-56.3, -32.34) * mm});
            skLineSegment(sketch, "E1102", {"start": v(-56.3, -32.34) * mm, "end": v(-56.51, -32.68) * mm});
            skLineSegment(sketch, "E1103", {"start": v(-56.51, -32.68) * mm, "end": v(-56.73, -33.03) * mm});
            skLineSegment(sketch, "E1104", {"start": v(-56.73, -33.03) * mm, "end": v(-56.95, -33.39) * mm});
            skLineSegment(sketch, "E1105", {"start": v(-56.95, -33.39) * mm, "end": v(-57.17, -33.76) * mm});
            skLineSegment(sketch, "E1106", {"start": v(-57.17, -33.76) * mm, "end": v(-57.38, -34.14) * mm});
            skLineSegment(sketch, "E1107", {"start": v(-57.38, -34.14) * mm, "end": v(-57.6, -34.54) * mm});
            skLineSegment(sketch, "E1108", {"start": v(-57.6, -34.54) * mm, "end": v(-57.82, -34.95) * mm});
            skLineSegment(sketch, "E1109", {"start": v(-57.82, -34.95) * mm, "end": v(-58.04, -35.37) * mm});
            skLineSegment(sketch, "E1110", {"start": v(-58.04, -35.37) * mm, "end": v(-58.26, -35.8) * mm});
            skLineSegment(sketch, "E1111", {"start": v(-58.26, -35.8) * mm, "end": v(-58.47, -36.25) * mm});
            skLineSegment(sketch, "E1112", {"start": v(-58.47, -36.25) * mm, "end": v(-58.69, -36.7) * mm});
            skLineSegment(sketch, "E1113", {"start": v(-58.69, -36.7) * mm, "end": v(-58.9, -37.17) * mm});
            skLineSegment(sketch, "E1114", {"start": v(-58.9, -37.17) * mm, "end": v(-58.98, -37.58) * mm});
            skLineSegment(sketch, "E1115", {"start": v(-58.98, -37.58) * mm, "end": v(-57.86, -39.3) * mm});
            skLineSegment(sketch, "E1116", {"start": v(-57.86, -39.3) * mm, "end": v(-57.45, -39.37) * mm});
            skLineSegment(sketch, "E1117", {"start": v(-57.45, -39.37) * mm, "end": v(-56.94, -39.36) * mm});
            skLineSegment(sketch, "E1118", {"start": v(-56.94, -39.36) * mm, "end": v(-56.43, -39.35) * mm});
            skLineSegment(sketch, "E1119", {"start": v(-56.43, -39.35) * mm, "end": v(-55.94, -39.32) * mm});
            skLineSegment(sketch, "E1120", {"start": v(-55.94, -39.32) * mm, "end": v(-55.46, -39.3) * mm});
            skLineSegment(sketch, "E1121", {"start": v(-55.46, -39.3) * mm, "end": v(-54.98, -39.26) * mm});
            skLineSegment(sketch, "E1122", {"start": v(-54.98, -39.26) * mm, "end": v(-54.52, -39.22) * mm});
            skLineSegment(sketch, "E1123", {"start": v(-54.52, -39.22) * mm, "end": v(-54.07, -39.18) * mm});
            skLineSegment(sketch, "E1124", {"start": v(-54.07, -39.18) * mm, "end": v(-53.63, -39.13) * mm});
            skLineSegment(sketch, "E1125", {"start": v(-53.63, -39.13) * mm, "end": v(-53.2, -39.08) * mm});
            skLineSegment(sketch, "E1126", {"start": v(-53.2, -39.08) * mm, "end": v(-52.79, -39.02) * mm});
            skLineSegment(sketch, "E1127", {"start": v(-52.79, -39.02) * mm, "end": v(-52.38, -38.96) * mm});
            skLineSegment(sketch, "E1128", {"start": v(-52.38, -38.96) * mm, "end": v(-51.98, -38.9) * mm});
            skLineSegment(sketch, "E1129", {"start": v(-51.98, -38.9) * mm, "end": v(-51.6, -38.82) * mm});
            skLineSegment(sketch, "E1130", {"start": v(-51.6, -38.82) * mm, "end": v(-51.23, -38.75) * mm});
            skLineSegment(sketch, "E1131", {"start": v(-51.23, -38.75) * mm, "end": v(-50.87, -38.67) * mm});
            skLineSegment(sketch, "E1132", {"start": v(-50.87, -38.67) * mm, "end": v(-50.52, -38.6) * mm});
            skLineSegment(sketch, "E1133", {"start": v(-50.52, -38.6) * mm, "end": v(-50.18, -38.52) * mm});
            skLineSegment(sketch, "E1134", {"start": v(-50.18, -38.52) * mm, "end": v(-49.85, -38.43) * mm});
            skLineSegment(sketch, "E1135", {"start": v(-49.85, -38.43) * mm, "end": v(-49.53, -38.35) * mm});
            skLineSegment(sketch, "E1136", {"start": v(-49.53, -38.35) * mm, "end": v(-49.23, -38.27) * mm});
            skLineSegment(sketch, "E1137", {"start": v(-49.23, -38.27) * mm, "end": v(-48.93, -38.18) * mm});
            skLineSegment(sketch, "E1138", {"start": v(-48.93, -38.18) * mm, "end": v(-48.65, -38.1) * mm});
            skLineSegment(sketch, "E1139", {"start": v(-48.65, -38.1) * mm, "end": v(-48.38, -38) * mm});
            skLineSegment(sketch, "E1140", {"start": v(-48.38, -38) * mm, "end": v(-48.12, -37.92) * mm});
            skLineSegment(sketch, "E1141", {"start": v(-48.12, -37.92) * mm, "end": v(-47.87, -37.83) * mm});
            skLineSegment(sketch, "E1142", {"start": v(-47.87, -37.83) * mm, "end": v(-47.63, -37.74) * mm});
            skLineSegment(sketch, "E1143", {"start": v(-47.63, -37.74) * mm, "end": v(-47.4, -37.65) * mm});
            skLineSegment(sketch, "E1144", {"start": v(-47.4, -37.65) * mm, "end": v(-47.18, -37.57) * mm});
            skLineSegment(sketch, "E1145", {"start": v(-47.18, -37.57) * mm, "end": v(-46.98, -37.48) * mm});
            skLineSegment(sketch, "E1146", {"start": v(-46.98, -37.48) * mm, "end": v(-46.78, -37.4) * mm});
            skLineSegment(sketch, "E1147", {"start": v(-46.78, -37.4) * mm, "end": v(-46.6, -37.31) * mm});
            skLineSegment(sketch, "E1148", {"start": v(-46.6, -37.31) * mm, "end": v(-46.42, -37.23) * mm});
            skLineSegment(sketch, "E1149", {"start": v(-46.42, -37.23) * mm, "end": v(-46.26, -37.15) * mm});
            skLineSegment(sketch, "E1150", {"start": v(-46.26, -37.15) * mm, "end": v(-46.01, -37.24) * mm});
            skLineSegment(sketch, "E1151", {"start": v(-46.01, -37.24) * mm, "end": v(-44.3, -39.25) * mm});
            skLineSegment(sketch, "E1152", {"start": v(-44.3, -39.25) * mm, "end": v(-44.26, -39.51) * mm});
            skLineSegment(sketch, "E1153", {"start": v(-44.26, -39.51) * mm, "end": v(-44.37, -39.66) * mm});
            skLineSegment(sketch, "E1154", {"start": v(-44.37, -39.66) * mm, "end": v(-44.48, -39.82) * mm});
            skLineSegment(sketch, "E1155", {"start": v(-44.48, -39.82) * mm, "end": v(-44.59, -39.99) * mm});
            skLineSegment(sketch, "E1156", {"start": v(-44.59, -39.99) * mm, "end": v(-44.7, -40.17) * mm});
            skLineSegment(sketch, "E1157", {"start": v(-44.7, -40.17) * mm, "end": v(-44.82, -40.36) * mm});
            skLineSegment(sketch, "E1158", {"start": v(-44.82, -40.36) * mm, "end": v(-44.94, -40.56) * mm});
            skLineSegment(sketch, "E1159", {"start": v(-44.94, -40.56) * mm, "end": v(-45.06, -40.77) * mm});
            skLineSegment(sketch, "E1160", {"start": v(-45.06, -40.77) * mm, "end": v(-45.2, -40.99) * mm});
            skLineSegment(sketch, "E1161", {"start": v(-45.2, -40.99) * mm, "end": v(-45.32, -41.22) * mm});
            skLineSegment(sketch, "E1162", {"start": v(-45.32, -41.22) * mm, "end": v(-45.45, -41.46) * mm});
            skLineSegment(sketch, "E1163", {"start": v(-45.45, -41.46) * mm, "end": v(-45.58, -41.72) * mm});
            skLineSegment(sketch, "E1164", {"start": v(-45.58, -41.72) * mm, "end": v(-45.71, -41.98) * mm});
            skLineSegment(sketch, "E1165", {"start": v(-45.71, -41.98) * mm, "end": v(-45.85, -42.26) * mm});
            skLineSegment(sketch, "E1166", {"start": v(-45.85, -42.26) * mm, "end": v(-45.98, -42.54) * mm});
            skLineSegment(sketch, "E1167", {"start": v(-45.98, -42.54) * mm, "end": v(-46.12, -42.84) * mm});
            skLineSegment(sketch, "E1168", {"start": v(-46.12, -42.84) * mm, "end": v(-46.25, -43.15) * mm});
            skLineSegment(sketch, "E1169", {"start": v(-46.25, -43.15) * mm, "end": v(-46.39, -43.47) * mm});
            skLineSegment(sketch, "E1170", {"start": v(-46.39, -43.47) * mm, "end": v(-46.52, -43.8) * mm});
            skLineSegment(sketch, "E1171", {"start": v(-46.52, -43.8) * mm, "end": v(-46.65, -44.15) * mm});
            skLineSegment(sketch, "E1172", {"start": v(-46.65, -44.15) * mm, "end": v(-46.79, -44.5) * mm});
            skLineSegment(sketch, "E1173", {"start": v(-46.79, -44.5) * mm, "end": v(-46.92, -44.87) * mm});
            skLineSegment(sketch, "E1174", {"start": v(-46.92, -44.87) * mm, "end": v(-47.05, -45.25) * mm});
            skLineSegment(sketch, "E1175", {"start": v(-47.05, -45.25) * mm, "end": v(-47.18, -45.64) * mm});
            skLineSegment(sketch, "E1176", {"start": v(-47.18, -45.64) * mm, "end": v(-47.3, -46.05) * mm});
            skLineSegment(sketch, "E1177", {"start": v(-47.3, -46.05) * mm, "end": v(-47.43, -46.46) * mm});
            skLineSegment(sketch, "E1178", {"start": v(-47.43, -46.46) * mm, "end": v(-47.55, -46.89) * mm});
            skLineSegment(sketch, "E1179", {"start": v(-47.55, -46.89) * mm, "end": v(-47.66, -47.32) * mm});
            skLineSegment(sketch, "E1180", {"start": v(-47.66, -47.32) * mm, "end": v(-47.78, -47.77) * mm});
            skLineSegment(sketch, "E1181", {"start": v(-47.78, -47.77) * mm, "end": v(-47.89, -48.23) * mm});
            skLineSegment(sketch, "E1182", {"start": v(-47.89, -48.23) * mm, "end": v(-48, -48.7) * mm});
            skLineSegment(sketch, "E1183", {"start": v(-48, -48.7) * mm, "end": v(-48.1, -49.19) * mm});
            skLineSegment(sketch, "E1184", {"start": v(-48.1, -49.19) * mm, "end": v(-48.2, -49.68) * mm});
            skLineSegment(sketch, "E1185", {"start": v(-48.2, -49.68) * mm, "end": v(-48.3, -50.19) * mm});
            skLineSegment(sketch, "E1186", {"start": v(-48.3, -50.19) * mm, "end": v(-48.28, -50.6) * mm});
            skLineSegment(sketch, "E1187", {"start": v(-48.28, -50.6) * mm, "end": v(-46.77, -52) * mm});
            skLineSegment(sketch, "E1188", {"start": v(-46.77, -52) * mm, "end": v(-46.36, -51.98) * mm});
            skLineSegment(sketch, "E1189", {"start": v(-46.36, -51.98) * mm, "end": v(-45.86, -51.84) * mm});
            skLineSegment(sketch, "E1190", {"start": v(-45.86, -51.84) * mm, "end": v(-45.38, -51.7) * mm});
            skLineSegment(sketch, "E1191", {"start": v(-45.38, -51.7) * mm, "end": v(-44.9, -51.57) * mm});
            skLineSegment(sketch, "E1192", {"start": v(-44.9, -51.57) * mm, "end": v(-44.44, -51.43) * mm});
            skLineSegment(sketch, "E1193", {"start": v(-44.44, -51.43) * mm, "end": v(-43.99, -51.28) * mm});
            skLineSegment(sketch, "E1194", {"start": v(-43.99, -51.28) * mm, "end": v(-43.55, -51.13) * mm});
            skLineSegment(sketch, "E1195", {"start": v(-43.55, -51.13) * mm, "end": v(-43.12, -50.98) * mm});
            skLineSegment(sketch, "E1196", {"start": v(-43.12, -50.98) * mm, "end": v(-42.7, -50.83) * mm});
            skLineSegment(sketch, "E1197", {"start": v(-42.7, -50.83) * mm, "end": v(-42.3, -50.67) * mm});
            skLineSegment(sketch, "E1198", {"start": v(-42.3, -50.67) * mm, "end": v(-41.91, -50.52) * mm});
            skLineSegment(sketch, "E1199", {"start": v(-41.91, -50.52) * mm, "end": v(-41.54, -50.36) * mm});
            skLineSegment(sketch, "E1200", {"start": v(-41.54, -50.36) * mm, "end": v(-41.17, -50.2) * mm});
            skLineSegment(sketch, "E1201", {"start": v(-41.17, -50.2) * mm, "end": v(-40.81, -50.04) * mm});
            skLineSegment(sketch, "E1202", {"start": v(-40.81, -50.04) * mm, "end": v(-40.47, -49.88) * mm});
            skLineSegment(sketch, "E1203", {"start": v(-40.47, -49.88) * mm, "end": v(-40.13, -49.72) * mm});
            skLineSegment(sketch, "E1204", {"start": v(-40.13, -49.72) * mm, "end": v(-39.81, -49.56) * mm});
            skLineSegment(sketch, "E1205", {"start": v(-39.81, -49.56) * mm, "end": v(-39.5, -49.4) * mm});
            skLineSegment(sketch, "E1206", {"start": v(-39.5, -49.4) * mm, "end": v(-39.2, -49.25) * mm});
            skLineSegment(sketch, "E1207", {"start": v(-39.2, -49.25) * mm, "end": v(-38.92, -49.1) * mm});
            skLineSegment(sketch, "E1208", {"start": v(-38.92, -49.1) * mm, "end": v(-38.64, -48.94) * mm});
            skLineSegment(sketch, "E1209", {"start": v(-38.64, -48.94) * mm, "end": v(-38.38, -48.78) * mm});
            skLineSegment(sketch, "E1210", {"start": v(-38.38, -48.78) * mm, "end": v(-38.12, -48.63) * mm});
            skLineSegment(sketch, "E1211", {"start": v(-38.12, -48.63) * mm, "end": v(-37.88, -48.48) * mm});
            skLineSegment(sketch, "E1212", {"start": v(-37.88, -48.48) * mm, "end": v(-37.65, -48.33) * mm});
            skLineSegment(sketch, "E1213", {"start": v(-37.65, -48.33) * mm, "end": v(-37.42, -48.18) * mm});
            skLineSegment(sketch, "E1214", {"start": v(-37.42, -48.18) * mm, "end": v(-37.21, -48.04) * mm});
            skLineSegment(sketch, "E1215", {"start": v(-37.21, -48.04) * mm, "end": v(-37.01, -47.9) * mm});
            skLineSegment(sketch, "E1216", {"start": v(-37.01, -47.9) * mm, "end": v(-36.82, -47.77) * mm});
            skLineSegment(sketch, "E1217", {"start": v(-36.82, -47.77) * mm, "end": v(-36.64, -47.63) * mm});
            skLineSegment(sketch, "E1218", {"start": v(-36.64, -47.63) * mm, "end": v(-36.47, -47.5) * mm});
            skLineSegment(sketch, "E1219", {"start": v(-36.47, -47.5) * mm, "end": v(-36.31, -47.38) * mm});
            skLineSegment(sketch, "E1220", {"start": v(-36.31, -47.38) * mm, "end": v(-36.16, -47.26) * mm});
            skLineSegment(sketch, "E1221", {"start": v(-36.16, -47.26) * mm, "end": v(-36.02, -47.15) * mm});
            skLineSegment(sketch, "E1222", {"start": v(-36.02, -47.15) * mm, "end": v(-35.76, -47.17) * mm});
            skLineSegment(sketch, "E1223", {"start": v(-35.76, -47.17) * mm, "end": v(-33.63, -48.72) * mm});
            skLineSegment(sketch, "E1224", {"start": v(-33.63, -48.72) * mm, "end": v(-33.52, -48.96) * mm});
            skLineSegment(sketch, "E1225", {"start": v(-33.52, -48.96) * mm, "end": v(-33.59, -49.13) * mm});
            skLineSegment(sketch, "E1226", {"start": v(-33.59, -49.13) * mm, "end": v(-33.65, -49.3) * mm});
            skLineSegment(sketch, "E1227", {"start": v(-33.65, -49.3) * mm, "end": v(-33.72, -49.5) * mm});
            skLineSegment(sketch, "E1228", {"start": v(-33.72, -49.5) * mm, "end": v(-33.8, -49.7) * mm});
            skLineSegment(sketch, "E1229", {"start": v(-33.8, -49.7) * mm, "end": v(-33.86, -49.91) * mm});
            skLineSegment(sketch, "E1230", {"start": v(-33.86, -49.91) * mm, "end": v(-33.93, -50.13) * mm});
            skLineSegment(sketch, "E1231", {"start": v(-33.93, -50.13) * mm, "end": v(-34, -50.37) * mm});
            skLineSegment(sketch, "E1232", {"start": v(-34, -50.37) * mm, "end": v(-34.07, -50.61) * mm});
            skLineSegment(sketch, "E1233", {"start": v(-34.07, -50.61) * mm, "end": v(-34.14, -50.87) * mm});
            skLineSegment(sketch, "E1234", {"start": v(-34.14, -50.87) * mm, "end": v(-34.2, -51.13) * mm});
            skLineSegment(sketch, "E1235", {"start": v(-34.2, -51.13) * mm, "end": v(-34.27, -51.41) * mm});
            skLineSegment(sketch, "E1236", {"start": v(-34.27, -51.41) * mm, "end": v(-34.34, -51.7) * mm});
            skLineSegment(sketch, "E1237", {"start": v(-34.34, -51.7) * mm, "end": v(-34.4, -52) * mm});
            skLineSegment(sketch, "E1238", {"start": v(-34.4, -52) * mm, "end": v(-34.46, -52.31) * mm});
            skLineSegment(sketch, "E1239", {"start": v(-34.46, -52.31) * mm, "end": v(-34.52, -52.63) * mm});
            skLineSegment(sketch, "E1240", {"start": v(-34.52, -52.63) * mm, "end": v(-34.58, -52.97) * mm});
            skLineSegment(sketch, "E1241", {"start": v(-34.58, -52.97) * mm, "end": v(-34.63, -53.31) * mm});
            skLineSegment(sketch, "E1242", {"start": v(-34.63, -53.31) * mm, "end": v(-34.69, -53.67) * mm});
            skLineSegment(sketch, "E1243", {"start": v(-34.69, -53.67) * mm, "end": v(-34.73, -54.03) * mm});
            skLineSegment(sketch, "E1244", {"start": v(-34.73, -54.03) * mm, "end": v(-34.78, -54.41) * mm});
            skLineSegment(sketch, "E1245", {"start": v(-34.78, -54.41) * mm, "end": v(-34.82, -54.8) * mm});
            skLineSegment(sketch, "E1246", {"start": v(-34.82, -54.8) * mm, "end": v(-34.85, -55.2) * mm});
            skLineSegment(sketch, "E1247", {"start": v(-34.85, -55.2) * mm, "end": v(-34.88, -55.6) * mm});
            skLineSegment(sketch, "E1248", {"start": v(-34.88, -55.6) * mm, "end": v(-34.9, -56.03) * mm});
            skLineSegment(sketch, "E1249", {"start": v(-34.9, -56.03) * mm, "end": v(-34.93, -56.46) * mm});
            skLineSegment(sketch, "E1250", {"start": v(-34.93, -56.46) * mm, "end": v(-34.94, -56.9) * mm});
            skLineSegment(sketch, "E1251", {"start": v(-34.94, -56.9) * mm, "end": v(-34.95, -57.35) * mm});
            skLineSegment(sketch, "E1252", {"start": v(-34.95, -57.35) * mm, "end": v(-34.96, -57.82) * mm});
            skLineSegment(sketch, "E1253", {"start": v(-34.96, -57.82) * mm, "end": v(-34.96, -58.3) * mm});
            skLineSegment(sketch, "E1254", {"start": v(-34.96, -58.3) * mm, "end": v(-34.95, -58.77) * mm});
            skLineSegment(sketch, "E1255", {"start": v(-34.95, -58.77) * mm, "end": v(-34.93, -59.27) * mm});
            skLineSegment(sketch, "E1256", {"start": v(-34.93, -59.27) * mm, "end": v(-34.9, -59.77) * mm});
            skLineSegment(sketch, "E1257", {"start": v(-34.9, -59.77) * mm, "end": v(-34.88, -60.29) * mm});
            skLineSegment(sketch, "E1258", {"start": v(-34.88, -60.29) * mm, "end": v(-34.77, -60.68) * mm});
            skLineSegment(sketch, "E1259", {"start": v(-34.77, -60.68) * mm, "end": v(-32.97, -61.68) * mm});
            skLineSegment(sketch, "E1260", {"start": v(-32.97, -61.68) * mm, "end": v(-32.58, -61.56) * mm});
            skLineSegment(sketch, "E1261", {"start": v(-32.58, -61.56) * mm, "end": v(-32.12, -61.31) * mm});
            skLineSegment(sketch, "E1262", {"start": v(-32.12, -61.31) * mm, "end": v(-31.68, -61.06) * mm});
            skLineSegment(sketch, "E1263", {"start": v(-31.68, -61.06) * mm, "end": v(-31.26, -60.82) * mm});
            skLineSegment(sketch, "E1264", {"start": v(-31.26, -60.82) * mm, "end": v(-30.84, -60.57) * mm});
            skLineSegment(sketch, "E1265", {"start": v(-30.84, -60.57) * mm, "end": v(-30.44, -60.32) * mm});
            skLineSegment(sketch, "E1266", {"start": v(-30.44, -60.32) * mm, "end": v(-30.05, -60.07) * mm});
            skLineSegment(sketch, "E1267", {"start": v(-30.05, -60.07) * mm, "end": v(-29.67, -59.82) * mm});
            skLineSegment(sketch, "E1268", {"start": v(-29.67, -59.82) * mm, "end": v(-29.3, -59.57) * mm});
            skLineSegment(sketch, "E1269", {"start": v(-29.3, -59.57) * mm, "end": v(-28.95, -59.33) * mm});
            skLineSegment(sketch, "E1270", {"start": v(-28.95, -59.33) * mm, "end": v(-28.6, -59.08) * mm});
            skLineSegment(sketch, "E1271", {"start": v(-28.6, -59.08) * mm, "end": v(-28.28, -58.84) * mm});
            skLineSegment(sketch, "E1272", {"start": v(-28.28, -58.84) * mm, "end": v(-27.96, -58.6) * mm});
            skLineSegment(sketch, "E1273", {"start": v(-27.96, -58.6) * mm, "end": v(-27.65, -58.36) * mm});
            skLineSegment(sketch, "E1274", {"start": v(-27.65, -58.36) * mm, "end": v(-27.35, -58.12) * mm});
            skLineSegment(sketch, "E1275", {"start": v(-27.35, -58.12) * mm, "end": v(-27.07, -57.88) * mm});
            skLineSegment(sketch, "E1276", {"start": v(-27.07, -57.88) * mm, "end": v(-26.8, -57.65) * mm});
            skLineSegment(sketch, "E1277", {"start": v(-26.8, -57.65) * mm, "end": v(-26.53, -57.42) * mm});
            skLineSegment(sketch, "E1278", {"start": v(-26.53, -57.42) * mm, "end": v(-26.28, -57.2) * mm});
            skLineSegment(sketch, "E1279", {"start": v(-26.28, -57.2) * mm, "end": v(-26.04, -56.98) * mm});
            skLineSegment(sketch, "E1280", {"start": v(-26.04, -56.98) * mm, "end": v(-25.8, -56.76) * mm});
            skLineSegment(sketch, "E1281", {"start": v(-25.8, -56.76) * mm, "end": v(-25.59, -56.55) * mm});
            skLineSegment(sketch, "E1282", {"start": v(-25.59, -56.55) * mm, "end": v(-25.38, -56.34) * mm});
            skLineSegment(sketch, "E1283", {"start": v(-25.38, -56.34) * mm, "end": v(-25.18, -56.13) * mm});
            skLineSegment(sketch, "E1284", {"start": v(-25.18, -56.13) * mm, "end": v(-24.99, -55.94) * mm});
            skLineSegment(sketch, "E1285", {"start": v(-24.99, -55.94) * mm, "end": v(-24.8, -55.74) * mm});
            skLineSegment(sketch, "E1286", {"start": v(-24.8, -55.74) * mm, "end": v(-24.64, -55.55) * mm});
            skLineSegment(sketch, "E1287", {"start": v(-24.64, -55.55) * mm, "end": v(-24.47, -55.37) * mm});
            skLineSegment(sketch, "E1288", {"start": v(-24.47, -55.37) * mm, "end": v(-24.32, -55.2) * mm});
            skLineSegment(sketch, "E1289", {"start": v(-24.32, -55.2) * mm, "end": v(-24.18, -55.02) * mm});
            skLineSegment(sketch, "E1290", {"start": v(-24.18, -55.02) * mm, "end": v(-24.05, -54.85) * mm});
            skLineSegment(sketch, "E1291", {"start": v(-24.05, -54.85) * mm, "end": v(-23.92, -54.7) * mm});
            skLineSegment(sketch, "E1292", {"start": v(-23.92, -54.7) * mm, "end": v(-23.8, -54.54) * mm});
            skLineSegment(sketch, "E1293", {"start": v(-23.8, -54.54) * mm, "end": v(-23.7, -54.4) * mm});
            skLineSegment(sketch, "E1294", {"start": v(-23.7, -54.4) * mm, "end": v(-23.44, -54.36) * mm});
            skLineSegment(sketch, "E1295", {"start": v(-23.44, -54.36) * mm, "end": v(-21, -55.35) * mm});
            skLineSegment(sketch, "E1296", {"start": v(-21, -55.35) * mm, "end": v(-20.83, -55.56) * mm});
            skLineSegment(sketch, "E1297", {"start": v(-20.83, -55.56) * mm, "end": v(-20.85, -55.74) * mm});
            skLineSegment(sketch, "E1298", {"start": v(-20.85, -55.74) * mm, "end": v(-20.88, -55.93) * mm});
            skLineSegment(sketch, "E1299", {"start": v(-20.88, -55.93) * mm, "end": v(-20.9, -56.13) * mm});
            skLineSegment(sketch, "E1300", {"start": v(-20.9, -56.13) * mm, "end": v(-20.92, -56.34) * mm});
            skLineSegment(sketch, "E1301", {"start": v(-20.92, -56.34) * mm, "end": v(-20.93, -56.56) * mm});
            skLineSegment(sketch, "E1302", {"start": v(-20.93, -56.56) * mm, "end": v(-20.95, -56.8) * mm});
            skLineSegment(sketch, "E1303", {"start": v(-20.95, -56.8) * mm, "end": v(-20.96, -57.04) * mm});
            skLineSegment(sketch, "E1304", {"start": v(-20.96, -57.04) * mm, "end": v(-20.97, -57.3) * mm});
            skLineSegment(sketch, "E1305", {"start": v(-20.97, -57.3) * mm, "end": v(-20.97, -57.56) * mm});
            skLineSegment(sketch, "E1306", {"start": v(-20.97, -57.56) * mm, "end": v(-20.98, -57.84) * mm});
            skLineSegment(sketch, "E1307", {"start": v(-20.98, -57.84) * mm, "end": v(-20.97, -58.12) * mm});
            skLineSegment(sketch, "E1308", {"start": v(-20.97, -58.12) * mm, "end": v(-20.97, -58.42) * mm});
            skLineSegment(sketch, "E1309", {"start": v(-20.97, -58.42) * mm, "end": v(-20.96, -58.72) * mm});
            skLineSegment(sketch, "E1310", {"start": v(-20.96, -58.72) * mm, "end": v(-20.94, -59.04) * mm});
            skLineSegment(sketch, "E1311", {"start": v(-20.94, -59.04) * mm, "end": v(-20.92, -59.37) * mm});
            skLineSegment(sketch, "E1312", {"start": v(-20.92, -59.37) * mm, "end": v(-20.9, -59.7) * mm});
            skLineSegment(sketch, "E1313", {"start": v(-20.9, -59.7) * mm, "end": v(-20.87, -60.05) * mm});
            skLineSegment(sketch, "E1314", {"start": v(-20.87, -60.05) * mm, "end": v(-20.83, -60.4) * mm});
            skLineSegment(sketch, "E1315", {"start": v(-20.83, -60.4) * mm, "end": v(-20.8, -60.78) * mm});
            skLineSegment(sketch, "E1316", {"start": v(-20.8, -60.78) * mm, "end": v(-20.75, -61.15) * mm});
            skLineSegment(sketch, "E1317", {"start": v(-20.75, -61.15) * mm, "end": v(-20.69, -61.54) * mm});
            skLineSegment(sketch, "E1318", {"start": v(-20.69, -61.54) * mm, "end": v(-20.63, -61.93) * mm});
            skLineSegment(sketch, "E1319", {"start": v(-20.63, -61.93) * mm, "end": v(-20.56, -62.34) * mm});
            skLineSegment(sketch, "E1320", {"start": v(-20.56, -62.34) * mm, "end": v(-20.49, -62.75) * mm});
            skLineSegment(sketch, "E1321", {"start": v(-20.49, -62.75) * mm, "end": v(-20.4, -63.18) * mm});
            skLineSegment(sketch, "E1322", {"start": v(-20.4, -63.18) * mm, "end": v(-20.31, -63.6) * mm});
            skLineSegment(sketch, "E1323", {"start": v(-20.31, -63.6) * mm, "end": v(-20.21, -64.05) * mm});
            skLineSegment(sketch, "E1324", {"start": v(-20.21, -64.05) * mm, "end": v(-20.1, -64.5) * mm});
            skLineSegment(sketch, "E1325", {"start": v(-20.1, -64.5) * mm, "end": v(-19.99, -64.96) * mm});
            skLineSegment(sketch, "E1326", {"start": v(-19.99, -64.96) * mm, "end": v(-19.86, -65.43) * mm});
            skLineSegment(sketch, "E1327", {"start": v(-19.86, -65.43) * mm, "end": v(-19.73, -65.9) * mm});
            skLineSegment(sketch, "E1328", {"start": v(-19.73, -65.9) * mm, "end": v(-19.59, -66.39) * mm});
            skLineSegment(sketch, "E1329", {"start": v(-19.59, -66.39) * mm, "end": v(-19.44, -66.88) * mm});
            skLineSegment(sketch, "E1330", {"start": v(-19.44, -66.88) * mm, "end": v(-19.23, -67.24) * mm});
            skLineSegment(sketch, "E1331", {"start": v(-19.23, -67.24) * mm, "end": v(-17.25, -67.78) * mm});
            skLineSegment(sketch, "E1332", {"start": v(-17.25, -67.78) * mm, "end": v(-16.9, -67.57) * mm});
            skLineSegment(sketch, "E1333", {"start": v(-16.9, -67.57) * mm, "end": v(-16.52, -67.22) * mm});
            skLineSegment(sketch, "E1334", {"start": v(-16.52, -67.22) * mm, "end": v(-16.15, -66.87) * mm});
            skLineSegment(sketch, "E1335", {"start": v(-16.15, -66.87) * mm, "end": v(-15.8, -66.53) * mm});
            skLineSegment(sketch, "E1336", {"start": v(-15.8, -66.53) * mm, "end": v(-15.45, -66.19) * mm});
            skLineSegment(sketch, "E1337", {"start": v(-15.45, -66.19) * mm, "end": v(-15.12, -65.85) * mm});
            skLineSegment(sketch, "E1338", {"start": v(-15.12, -65.85) * mm, "end": v(-14.8, -65.51) * mm});
            skLineSegment(sketch, "E1339", {"start": v(-14.8, -65.51) * mm, "end": v(-14.5, -65.18) * mm});
            skLineSegment(sketch, "E1340", {"start": v(-14.5, -65.18) * mm, "end": v(-14.2, -64.85) * mm});
            skLineSegment(sketch, "E1341", {"start": v(-14.2, -64.85) * mm, "end": v(-13.91, -64.53) * mm});
            skLineSegment(sketch, "E1342", {"start": v(-13.91, -64.53) * mm, "end": v(-13.64, -64.21) * mm});
            skLineSegment(sketch, "E1343", {"start": v(-13.64, -64.21) * mm, "end": v(-13.37, -63.9) * mm});
            skLineSegment(sketch, "E1344", {"start": v(-13.37, -63.9) * mm, "end": v(-13.12, -63.58) * mm});
            skLineSegment(sketch, "E1345", {"start": v(-13.12, -63.58) * mm, "end": v(-12.88, -63.28) * mm});
            skLineSegment(sketch, "E1346", {"start": v(-12.88, -63.28) * mm, "end": v(-12.65, -62.98) * mm});
            skLineSegment(sketch, "E1347", {"start": v(-12.65, -62.98) * mm, "end": v(-12.43, -62.68) * mm});
            skLineSegment(sketch, "E1348", {"start": v(-12.43, -62.68) * mm, "end": v(-12.22, -62.39) * mm});
            skLineSegment(sketch, "E1349", {"start": v(-12.22, -62.39) * mm, "end": v(-12.02, -62.1) * mm});
            skLineSegment(sketch, "E1350", {"start": v(-12.02, -62.1) * mm, "end": v(-11.83, -61.83) * mm});
            skLineSegment(sketch, "E1351", {"start": v(-11.83, -61.83) * mm, "end": v(-11.65, -61.55) * mm});
            skLineSegment(sketch, "E1352", {"start": v(-11.65, -61.55) * mm, "end": v(-11.47, -61.29) * mm});
            skLineSegment(sketch, "E1353", {"start": v(-11.47, -61.29) * mm, "end": v(-11.31, -61.03) * mm});
            skLineSegment(sketch, "E1354", {"start": v(-11.31, -61.03) * mm, "end": v(-11.16, -60.77) * mm});
            skLineSegment(sketch, "E1355", {"start": v(-11.16, -60.77) * mm, "end": v(-11, -60.53) * mm});
            skLineSegment(sketch, "E1356", {"start": v(-11, -60.53) * mm, "end": v(-10.87, -60.29) * mm});
            skLineSegment(sketch, "E1357", {"start": v(-10.87, -60.29) * mm, "end": v(-10.75, -60.06) * mm});
            skLineSegment(sketch, "E1358", {"start": v(-10.75, -60.06) * mm, "end": v(-10.62, -59.83) * mm});
            skLineSegment(sketch, "E1359", {"start": v(-10.62, -59.83) * mm, "end": v(-10.51, -59.62) * mm});
            skLineSegment(sketch, "E1360", {"start": v(-10.51, -59.62) * mm, "end": v(-10.4, -59.4) * mm});
            skLineSegment(sketch, "E1361", {"start": v(-10.4, -59.4) * mm, "end": v(-10.3, -59.2) * mm});
            skLineSegment(sketch, "E1362", {"start": v(-10.3, -59.2) * mm, "end": v(-10.22, -59.01) * mm});
            skLineSegment(sketch, "E1363", {"start": v(-10.22, -59.01) * mm, "end": v(-10.14, -58.83) * mm});
            skLineSegment(sketch, "E1364", {"start": v(-10.14, -58.83) * mm, "end": v(-10.06, -58.65) * mm});
            skLineSegment(sketch, "E1365", {"start": v(-10.06, -58.65) * mm, "end": v(-9.99, -58.49) * mm});
            skLineSegment(sketch, "E1366", {"start": v(-9.99, -58.49) * mm, "end": v(-9.75, -58.39) * mm});
            skLineSegment(sketch, "E1367", {"start": v(-9.75, -58.39) * mm, "end": v(-7.14, -58.77) * mm});
            skLineSegment(sketch, "E1368", {"start": v(-7.14, -58.77) * mm, "end": v(-6.93, -58.93) * mm});
            skLineSegment(sketch, "E1369", {"start": v(-6.93, -58.93) * mm, "end": v(-6.9, -59.1) * mm});
            skLineSegment(sketch, "E1370", {"start": v(-6.9, -59.1) * mm, "end": v(-6.88, -59.3) * mm});
            skLineSegment(sketch, "E1371", {"start": v(-6.88, -59.3) * mm, "end": v(-6.86, -59.5) * mm});
            skLineSegment(sketch, "E1372", {"start": v(-6.86, -59.5) * mm, "end": v(-6.82, -59.7) * mm});
            skLineSegment(sketch, "E1373", {"start": v(-6.82, -59.7) * mm, "end": v(-6.79, -59.93) * mm});
            skLineSegment(sketch, "E1374", {"start": v(-6.79, -59.93) * mm, "end": v(-6.75, -60.16) * mm});
            skLineSegment(sketch, "E1375", {"start": v(-6.75, -60.16) * mm, "end": v(-6.7, -60.4) * mm});
            skLineSegment(sketch, "E1376", {"start": v(-6.7, -60.4) * mm, "end": v(-6.65, -60.65) * mm});
            skLineSegment(sketch, "E1377", {"start": v(-6.65, -60.65) * mm, "end": v(-6.59, -60.9) * mm});
            skLineSegment(sketch, "E1378", {"start": v(-6.59, -60.9) * mm, "end": v(-6.52, -61.17) * mm});
            skLineSegment(sketch, "E1379", {"start": v(-6.52, -61.17) * mm, "end": v(-6.45, -61.45) * mm});
            skLineSegment(sketch, "E1380", {"start": v(-6.45, -61.45) * mm, "end": v(-6.38, -61.74) * mm});
            skLineSegment(sketch, "E1381", {"start": v(-6.38, -61.74) * mm, "end": v(-6.3, -62.03) * mm});
            skLineSegment(sketch, "E1382", {"start": v(-6.3, -62.03) * mm, "end": v(-6.2, -62.34) * mm});
            skLineSegment(sketch, "E1383", {"start": v(-6.2, -62.34) * mm, "end": v(-6.1, -62.65) * mm});
            skLineSegment(sketch, "E1384", {"start": v(-6.1, -62.65) * mm, "end": v(-6, -62.97) * mm});
            skLineSegment(sketch, "E1385", {"start": v(-6, -62.97) * mm, "end": v(-5.9, -63.3) * mm});
            skLineSegment(sketch, "E1386", {"start": v(-5.9, -63.3) * mm, "end": v(-5.77, -63.64) * mm});
            skLineSegment(sketch, "E1387", {"start": v(-5.77, -63.64) * mm, "end": v(-5.64, -63.98) * mm});
            skLineSegment(sketch, "E1388", {"start": v(-5.64, -63.98) * mm, "end": v(-5.5, -64.34) * mm});
            skLineSegment(sketch, "E1389", {"start": v(-5.5, -64.34) * mm, "end": v(-5.36, -64.7) * mm});
            skLineSegment(sketch, "E1390", {"start": v(-5.36, -64.7) * mm, "end": v(-5.2, -65.07) * mm});
            skLineSegment(sketch, "E1391", {"start": v(-5.2, -65.07) * mm, "end": v(-5.04, -65.45) * mm});
            skLineSegment(sketch, "E1392", {"start": v(-5.04, -65.45) * mm, "end": v(-4.87, -65.83) * mm});
            skLineSegment(sketch, "E1393", {"start": v(-4.87, -65.83) * mm, "end": v(-4.7, -66.22) * mm});
            skLineSegment(sketch, "E1394", {"start": v(-4.7, -66.22) * mm, "end": v(-4.5, -66.62) * mm});
            skLineSegment(sketch, "E1395", {"start": v(-4.5, -66.62) * mm, "end": v(-4.3, -67.03) * mm});
            skLineSegment(sketch, "E1396", {"start": v(-4.3, -67.03) * mm, "end": v(-4.08, -67.44) * mm});
            skLineSegment(sketch, "E1397", {"start": v(-4.08, -67.44) * mm, "end": v(-3.86, -67.86) * mm});
            skLineSegment(sketch, "E1398", {"start": v(-3.86, -67.86) * mm, "end": v(-3.63, -68.28) * mm});
            skLineSegment(sketch, "E1399", {"start": v(-3.63, -68.28) * mm, "end": v(-3.39, -68.71) * mm});
            skLineSegment(sketch, "E1400", {"start": v(-3.39, -68.71) * mm, "end": v(-3.13, -69.15) * mm});
            skLineSegment(sketch, "E1401", {"start": v(-3.13, -69.15) * mm, "end": v(-2.87, -69.59) * mm});
            skLineSegment(sketch, "E1402", {"start": v(-2.87, -69.59) * mm, "end": v(-2.58, -69.89) * mm});
            skLineSegment(sketch, "E1403", {"start": v(-2.58, -69.89) * mm, "end": v(-0.53, -69.94) * mm});
            skLineSegment(sketch, "E1404", {"start": v(-0.53, -69.94) * mm, "end": v(-0.24, -69.65) * mm});
            skLineSegment(sketch, "E1405", {"start": v(-0.24, -69.65) * mm, "end": v(0.05, -69.22) * mm});
            skLineSegment(sketch, "E1406", {"start": v(0.05, -69.22) * mm, "end": v(0.32, -68.8) * mm});
            skLineSegment(sketch, "E1407", {"start": v(0.32, -68.8) * mm, "end": v(0.59, -68.38) * mm});
            skLineSegment(sketch, "E1408", {"start": v(0.59, -68.38) * mm, "end": v(0.84, -67.96) * mm});
            skLineSegment(sketch, "E1409", {"start": v(0.84, -67.96) * mm, "end": v(1.08, -67.56) * mm});
            skLineSegment(sketch, "E1410", {"start": v(1.08, -67.56) * mm, "end": v(1.3, -67.15) * mm});
            skLineSegment(sketch, "E1411", {"start": v(1.3, -67.15) * mm, "end": v(1.53, -66.76) * mm});
            skLineSegment(sketch, "E1412", {"start": v(1.53, -66.76) * mm, "end": v(1.74, -66.37) * mm});
            skLineSegment(sketch, "E1413", {"start": v(1.74, -66.37) * mm, "end": v(1.94, -65.98) * mm});
            skLineSegment(sketch, "E1414", {"start": v(1.94, -65.98) * mm, "end": v(2.13, -65.6) * mm});
            skLineSegment(sketch, "E1415", {"start": v(2.13, -65.6) * mm, "end": v(2.3, -65.24) * mm});
            skLineSegment(sketch, "E1416", {"start": v(2.3, -65.24) * mm, "end": v(2.48, -64.88) * mm});
            skLineSegment(sketch, "E1417", {"start": v(2.48, -64.88) * mm, "end": v(2.64, -64.52) * mm});
            skLineSegment(sketch, "E1418", {"start": v(2.64, -64.52) * mm, "end": v(2.79, -64.17) * mm});
            skLineSegment(sketch, "E1419", {"start": v(2.79, -64.17) * mm, "end": v(2.93, -63.83) * mm});
            skLineSegment(sketch, "E1420", {"start": v(2.93, -63.83) * mm, "end": v(3.07, -63.5) * mm});
            skLineSegment(sketch, "E1421", {"start": v(3.07, -63.5) * mm, "end": v(3.2, -63.18) * mm});
            skLineSegment(sketch, "E1422", {"start": v(3.2, -63.18) * mm, "end": v(3.31, -62.86) * mm});
            skLineSegment(sketch, "E1423", {"start": v(3.31, -62.86) * mm, "end": v(3.42, -62.55) * mm});
            skLineSegment(sketch, "E1424", {"start": v(3.42, -62.55) * mm, "end": v(3.53, -62.25) * mm});
            skLineSegment(sketch, "E1425", {"start": v(3.53, -62.25) * mm, "end": v(3.62, -61.96) * mm});
            skLineSegment(sketch, "E1426", {"start": v(3.62, -61.96) * mm, "end": v(3.71, -61.68) * mm});
            skLineSegment(sketch, "E1427", {"start": v(3.71, -61.68) * mm, "end": v(3.8, -61.4) * mm});
            skLineSegment(sketch, "E1428", {"start": v(3.8, -61.4) * mm, "end": v(3.87, -61.14) * mm});
            skLineSegment(sketch, "E1429", {"start": v(3.87, -61.14) * mm, "end": v(3.94, -60.88) * mm});
            skLineSegment(sketch, "E1430", {"start": v(3.94, -60.88) * mm, "end": v(4, -60.64) * mm});
            skLineSegment(sketch, "E1431", {"start": v(4, -60.64) * mm, "end": v(4.06, -60.4) * mm});
            skLineSegment(sketch, "E1432", {"start": v(4.06, -60.4) * mm, "end": v(4.11, -60.17) * mm});
            skLineSegment(sketch, "E1433", {"start": v(4.11, -60.17) * mm, "end": v(4.16, -59.95) * mm});
            skLineSegment(sketch, "E1434", {"start": v(4.16, -59.95) * mm, "end": v(4.2, -59.75) * mm});
            skLineSegment(sketch, "E1435", {"start": v(4.2, -59.75) * mm, "end": v(4.24, -59.55) * mm});
            skLineSegment(sketch, "E1436", {"start": v(4.24, -59.55) * mm, "end": v(4.27, -59.36) * mm});
            skLineSegment(sketch, "E1437", {"start": v(4.27, -59.36) * mm, "end": v(4.3, -59.18) * mm});
            skLineSegment(sketch, "E1438", {"start": v(4.3, -59.18) * mm, "end": v(4.51, -59.02) * mm});
            skLineSegment(sketch, "E1439", {"start": v(4.51, -59.02) * mm, "end": v(7.14, -58.77) * mm});
            skLineSegment(sketch, "E1440", {"start": v(7.14, -58.77) * mm, "end": v(7.38, -58.87) * mm});
            skLineSegment(sketch, "E1441", {"start": v(7.38, -58.87) * mm, "end": v(7.44, -59.04) * mm});
            skLineSegment(sketch, "E1442", {"start": v(7.44, -59.04) * mm, "end": v(7.5, -59.22) * mm});
            skLineSegment(sketch, "E1443", {"start": v(7.5, -59.22) * mm, "end": v(7.58, -59.41) * mm});
            skLineSegment(sketch, "E1444", {"start": v(7.58, -59.41) * mm, "end": v(7.66, -59.6) * mm});
            skLineSegment(sketch, "E1445", {"start": v(7.66, -59.6) * mm, "end": v(7.75, -59.81) * mm});
            skLineSegment(sketch, "E1446", {"start": v(7.75, -59.81) * mm, "end": v(7.85, -60.03) * mm});
            skLineSegment(sketch, "E1447", {"start": v(7.85, -60.03) * mm, "end": v(7.95, -60.25) * mm});
            skLineSegment(sketch, "E1448", {"start": v(7.95, -60.25) * mm, "end": v(8.06, -60.48) * mm});
            skLineSegment(sketch, "E1449", {"start": v(8.06, -60.48) * mm, "end": v(8.18, -60.71) * mm});
            skLineSegment(sketch, "E1450", {"start": v(8.18, -60.71) * mm, "end": v(8.3, -60.96) * mm});
            skLineSegment(sketch, "E1451", {"start": v(8.3, -60.96) * mm, "end": v(8.44, -61.21) * mm});
            skLineSegment(sketch, "E1452", {"start": v(8.44, -61.21) * mm, "end": v(8.58, -61.47) * mm});
            skLineSegment(sketch, "E1453", {"start": v(8.58, -61.47) * mm, "end": v(8.73, -61.74) * mm});
            skLineSegment(sketch, "E1454", {"start": v(8.73, -61.74) * mm, "end": v(8.9, -62.01) * mm});
            skLineSegment(sketch, "E1455", {"start": v(8.9, -62.01) * mm, "end": v(9.06, -62.3) * mm});
            skLineSegment(sketch, "E1456", {"start": v(9.06, -62.3) * mm, "end": v(9.24, -62.58) * mm});
            skLineSegment(sketch, "E1457", {"start": v(9.24, -62.58) * mm, "end": v(9.43, -62.87) * mm});
            skLineSegment(sketch, "E1458", {"start": v(9.43, -62.87) * mm, "end": v(9.63, -63.17) * mm});
            skLineSegment(sketch, "E1459", {"start": v(9.63, -63.17) * mm, "end": v(9.83, -63.48) * mm});
            skLineSegment(sketch, "E1460", {"start": v(9.83, -63.48) * mm, "end": v(10.05, -63.79) * mm});
            skLineSegment(sketch, "E1461", {"start": v(10.05, -63.79) * mm, "end": v(10.28, -64.1) * mm});
            skLineSegment(sketch, "E1462", {"start": v(10.28, -64.1) * mm, "end": v(10.52, -64.43) * mm});
            skLineSegment(sketch, "E1463", {"start": v(10.52, -64.43) * mm, "end": v(10.76, -64.75) * mm});
            skLineSegment(sketch, "E1464", {"start": v(10.76, -64.75) * mm, "end": v(11.02, -65.09) * mm});
            skLineSegment(sketch, "E1465", {"start": v(11.02, -65.09) * mm, "end": v(11.3, -65.42) * mm});
            skLineSegment(sketch, "E1466", {"start": v(11.3, -65.42) * mm, "end": v(11.58, -65.76) * mm});
            skLineSegment(sketch, "E1467", {"start": v(11.58, -65.76) * mm, "end": v(11.87, -66.1) * mm});
            skLineSegment(sketch, "E1468", {"start": v(11.87, -66.1) * mm, "end": v(12.17, -66.46) * mm});
            skLineSegment(sketch, "E1469", {"start": v(12.17, -66.46) * mm, "end": v(12.49, -66.81) * mm});
            skLineSegment(sketch, "E1470", {"start": v(12.49, -66.81) * mm, "end": v(12.82, -67.17) * mm});
            skLineSegment(sketch, "E1471", {"start": v(12.82, -67.17) * mm, "end": v(13.16, -67.53) * mm});
            skLineSegment(sketch, "E1472", {"start": v(13.16, -67.53) * mm, "end": v(13.5, -67.89) * mm});
            skLineSegment(sketch, "E1473", {"start": v(13.5, -67.89) * mm, "end": v(13.87, -68.25) * mm});
            skLineSegment(sketch, "E1474", {"start": v(13.87, -68.25) * mm, "end": v(14.22, -68.48) * mm});
            skLineSegment(sketch, "E1475", {"start": v(14.22, -68.48) * mm, "end": v(16.22, -68.03) * mm});
            skLineSegment(sketch, "E1476", {"start": v(16.22, -68.03) * mm, "end": v(16.44, -67.68) * mm});
            skLineSegment(sketch, "E1477", {"start": v(16.44, -67.68) * mm, "end": v(16.61, -67.2) * mm});
            skLineSegment(sketch, "E1478", {"start": v(16.61, -67.2) * mm, "end": v(16.78, -66.72) * mm});
            skLineSegment(sketch, "E1479", {"start": v(16.78, -66.72) * mm, "end": v(16.93, -66.25) * mm});
            skLineSegment(sketch, "E1480", {"start": v(16.93, -66.25) * mm, "end": v(17.08, -65.79) * mm});
            skLineSegment(sketch, "E1481", {"start": v(17.08, -65.79) * mm, "end": v(17.21, -65.33) * mm});
            skLineSegment(sketch, "E1482", {"start": v(17.21, -65.33) * mm, "end": v(17.34, -64.89) * mm});
            skLineSegment(sketch, "E1483", {"start": v(17.34, -64.89) * mm, "end": v(17.46, -64.45) * mm});
            skLineSegment(sketch, "E1484", {"start": v(17.46, -64.45) * mm, "end": v(17.57, -64.02) * mm});
            skLineSegment(sketch, "E1485", {"start": v(17.57, -64.02) * mm, "end": v(17.67, -63.6) * mm});
            skLineSegment(sketch, "E1486", {"start": v(17.67, -63.6) * mm, "end": v(17.77, -63.2) * mm});
            skLineSegment(sketch, "E1487", {"start": v(17.77, -63.2) * mm, "end": v(17.85, -62.8) * mm});
            skLineSegment(sketch, "E1488", {"start": v(17.85, -62.8) * mm, "end": v(17.93, -62.4) * mm});
            skLineSegment(sketch, "E1489", {"start": v(17.93, -62.4) * mm, "end": v(18, -62.02) * mm});
            skLineSegment(sketch, "E1490", {"start": v(18, -62.02) * mm, "end": v(18.07, -61.64) * mm});
            skLineSegment(sketch, "E1491", {"start": v(18.07, -61.64) * mm, "end": v(18.12, -61.28) * mm});
            skLineSegment(sketch, "E1492", {"start": v(18.12, -61.28) * mm, "end": v(18.18, -60.92) * mm});
            skLineSegment(sketch, "E1493", {"start": v(18.18, -60.92) * mm, "end": v(18.22, -60.58) * mm});
            skLineSegment(sketch, "E1494", {"start": v(18.22, -60.58) * mm, "end": v(18.26, -60.24) * mm});
            skLineSegment(sketch, "E1495", {"start": v(18.26, -60.24) * mm, "end": v(18.3, -59.91) * mm});
            skLineSegment(sketch, "E1496", {"start": v(18.3, -59.91) * mm, "end": v(18.32, -59.6) * mm});
            skLineSegment(sketch, "E1497", {"start": v(18.32, -59.6) * mm, "end": v(18.35, -59.3) * mm});
            skLineSegment(sketch, "E1498", {"start": v(18.35, -59.3) * mm, "end": v(18.36, -59) * mm});
            skLineSegment(sketch, "E1499", {"start": v(18.36, -59) * mm, "end": v(18.38, -58.71) * mm});
            skLineSegment(sketch, "E1500", {"start": v(18.38, -58.71) * mm, "end": v(18.39, -58.44) * mm});
            skLineSegment(sketch, "E1501", {"start": v(18.39, -58.44) * mm, "end": v(18.4, -58.17) * mm});
            skLineSegment(sketch, "E1502", {"start": v(18.4, -58.17) * mm, "end": v(18.4, -57.92) * mm});
            skLineSegment(sketch, "E1503", {"start": v(18.4, -57.92) * mm, "end": v(18.4, -57.67) * mm});
            skLineSegment(sketch, "E1504", {"start": v(18.4, -57.67) * mm, "end": v(18.4, -57.44) * mm});
            skLineSegment(sketch, "E1505", {"start": v(18.4, -57.44) * mm, "end": v(18.39, -57.22) * mm});
            skLineSegment(sketch, "E1506", {"start": v(18.39, -57.22) * mm, "end": v(18.38, -57) * mm});
            skLineSegment(sketch, "E1507", {"start": v(18.38, -57) * mm, "end": v(18.36, -56.8) * mm});
            skLineSegment(sketch, "E1508", {"start": v(18.36, -56.8) * mm, "end": v(18.35, -56.61) * mm});
            skLineSegment(sketch, "E1509", {"start": v(18.35, -56.61) * mm, "end": v(18.34, -56.43) * mm});
            skLineSegment(sketch, "E1510", {"start": v(18.34, -56.43) * mm, "end": v(18.5, -56.23) * mm});
            skLineSegment(sketch, "E1511", {"start": v(18.5, -56.23) * mm, "end": v(21, -55.35) * mm});
            skLineSegment(sketch, "E1512", {"start": v(21, -55.35) * mm, "end": v(21.25, -55.4) * mm});
            skLineSegment(sketch, "E1513", {"start": v(21.25, -55.4) * mm, "end": v(21.35, -55.55) * mm});
            skLineSegment(sketch, "E1514", {"start": v(21.35, -55.55) * mm, "end": v(21.46, -55.7) * mm});
            skLineSegment(sketch, "E1515", {"start": v(21.46, -55.7) * mm, "end": v(21.58, -55.87) * mm});
            skLineSegment(sketch, "E1516", {"start": v(21.58, -55.87) * mm, "end": v(21.7, -56.04) * mm});
            skLineSegment(sketch, "E1517", {"start": v(21.7, -56.04) * mm, "end": v(21.84, -56.22) * mm});
            skLineSegment(sketch, "E1518", {"start": v(21.84, -56.22) * mm, "end": v(21.98, -56.4) * mm});
            skLineSegment(sketch, "E1519", {"start": v(21.98, -56.4) * mm, "end": v(22.14, -56.6) * mm});
            skLineSegment(sketch, "E1520", {"start": v(22.14, -56.6) * mm, "end": v(22.3, -56.79) * mm});
            skLineSegment(sketch, "E1521", {"start": v(22.3, -56.79) * mm, "end": v(22.47, -57) * mm});
            skLineSegment(sketch, "E1522", {"start": v(22.47, -57) * mm, "end": v(22.65, -57.2) * mm});
            skLineSegment(sketch, "E1523", {"start": v(22.65, -57.2) * mm, "end": v(22.84, -57.41) * mm});
            skLineSegment(sketch, "E1524", {"start": v(22.84, -57.41) * mm, "end": v(23.04, -57.63) * mm});
            skLineSegment(sketch, "E1525", {"start": v(23.04, -57.63) * mm, "end": v(23.25, -57.85) * mm});
            skLineSegment(sketch, "E1526", {"start": v(23.25, -57.85) * mm, "end": v(23.47, -58.08) * mm});
            skLineSegment(sketch, "E1527", {"start": v(23.47, -58.08) * mm, "end": v(23.7, -58.31) * mm});
            skLineSegment(sketch, "E1528", {"start": v(23.7, -58.31) * mm, "end": v(23.95, -58.55) * mm});
            skLineSegment(sketch, "E1529", {"start": v(23.95, -58.55) * mm, "end": v(24.2, -58.79) * mm});
            skLineSegment(sketch, "E1530", {"start": v(24.2, -58.79) * mm, "end": v(24.46, -59.03) * mm});
            skLineSegment(sketch, "E1531", {"start": v(24.46, -59.03) * mm, "end": v(24.74, -59.28) * mm});
            skLineSegment(sketch, "E1532", {"start": v(24.74, -59.28) * mm, "end": v(25.02, -59.53) * mm});
            skLineSegment(sketch, "E1533", {"start": v(25.02, -59.53) * mm, "end": v(25.32, -59.78) * mm});
            skLineSegment(sketch, "E1534", {"start": v(25.32, -59.78) * mm, "end": v(25.63, -60.04) * mm});
            skLineSegment(sketch, "E1535", {"start": v(25.63, -60.04) * mm, "end": v(25.95, -60.3) * mm});
            skLineSegment(sketch, "E1536", {"start": v(25.95, -60.3) * mm, "end": v(26.28, -60.56) * mm});
            skLineSegment(sketch, "E1537", {"start": v(26.28, -60.56) * mm, "end": v(26.62, -60.82) * mm});
            skLineSegment(sketch, "E1538", {"start": v(26.62, -60.82) * mm, "end": v(26.98, -61.08) * mm});
            skLineSegment(sketch, "E1539", {"start": v(26.98, -61.08) * mm, "end": v(27.34, -61.35) * mm});
            skLineSegment(sketch, "E1540", {"start": v(27.34, -61.35) * mm, "end": v(27.72, -61.61) * mm});
            skLineSegment(sketch, "E1541", {"start": v(27.72, -61.61) * mm, "end": v(28.11, -61.88) * mm});
            skLineSegment(sketch, "E1542", {"start": v(28.11, -61.88) * mm, "end": v(28.52, -62.15) * mm});
            skLineSegment(sketch, "E1543", {"start": v(28.52, -62.15) * mm, "end": v(28.93, -62.42) * mm});
            skLineSegment(sketch, "E1544", {"start": v(28.93, -62.42) * mm, "end": v(29.36, -62.68) * mm});
            skLineSegment(sketch, "E1545", {"start": v(29.36, -62.68) * mm, "end": v(29.8, -62.95) * mm});
            skLineSegment(sketch, "E1546", {"start": v(29.8, -62.95) * mm, "end": v(30.2, -63.08) * mm});
            skLineSegment(sketch, "E1547", {"start": v(30.2, -63.08) * mm, "end": v(32.03, -62.17) * mm});
            skLineSegment(sketch, "E1548", {"start": v(32.03, -62.17) * mm, "end": v(32.16, -61.78) * mm});
            skLineSegment(sketch, "E1549", {"start": v(32.16, -61.78) * mm, "end": v(32.21, -61.27) * mm});
            skLineSegment(sketch, "E1550", {"start": v(32.21, -61.27) * mm, "end": v(32.26, -60.76) * mm});
            skLineSegment(sketch, "E1551", {"start": v(32.26, -60.76) * mm, "end": v(32.3, -60.27) * mm});
            skLineSegment(sketch, "E1552", {"start": v(32.3, -60.27) * mm, "end": v(32.33, -59.79) * mm});
            skLineSegment(sketch, "E1553", {"start": v(32.33, -59.79) * mm, "end": v(32.35, -59.32) * mm});
            skLineSegment(sketch, "E1554", {"start": v(32.35, -59.32) * mm, "end": v(32.37, -58.85) * mm});
            skLineSegment(sketch, "E1555", {"start": v(32.37, -58.85) * mm, "end": v(32.38, -58.4) * mm});
            skLineSegment(sketch, "E1556", {"start": v(32.38, -58.4) * mm, "end": v(32.38, -57.96) * mm});
            skLineSegment(sketch, "E1557", {"start": v(32.38, -57.96) * mm, "end": v(32.38, -57.53) * mm});
            skLineSegment(sketch, "E1558", {"start": v(32.38, -57.53) * mm, "end": v(32.37, -57.1) * mm});
            skLineSegment(sketch, "E1559", {"start": v(32.37, -57.1) * mm, "end": v(32.36, -56.7) * mm});
            skLineSegment(sketch, "E1560", {"start": v(32.36, -56.7) * mm, "end": v(32.34, -56.3) * mm});
            skLineSegment(sketch, "E1561", {"start": v(32.34, -56.3) * mm, "end": v(32.32, -55.9) * mm});
            skLineSegment(sketch, "E1562", {"start": v(32.32, -55.9) * mm, "end": v(32.3, -55.53) * mm});
            skLineSegment(sketch, "E1563", {"start": v(32.3, -55.53) * mm, "end": v(32.26, -55.16) * mm});
            skLineSegment(sketch, "E1564", {"start": v(32.26, -55.16) * mm, "end": v(32.23, -54.8) * mm});
            skLineSegment(sketch, "E1565", {"start": v(32.23, -54.8) * mm, "end": v(32.19, -54.46) * mm});
            skLineSegment(sketch, "E1566", {"start": v(32.19, -54.46) * mm, "end": v(32.15, -54.12) * mm});
            skLineSegment(sketch, "E1567", {"start": v(32.15, -54.12) * mm, "end": v(32.1, -53.8) * mm});
            skLineSegment(sketch, "E1568", {"start": v(32.1, -53.8) * mm, "end": v(32.05, -53.48) * mm});
            skLineSegment(sketch, "E1569", {"start": v(32.05, -53.48) * mm, "end": v(32, -53.18) * mm});
            skLineSegment(sketch, "E1570", {"start": v(32, -53.18) * mm, "end": v(31.95, -52.89) * mm});
            skLineSegment(sketch, "E1571", {"start": v(31.95, -52.89) * mm, "end": v(31.9, -52.6) * mm});
            skLineSegment(sketch, "E1572", {"start": v(31.9, -52.6) * mm, "end": v(31.84, -52.34) * mm});
            skLineSegment(sketch, "E1573", {"start": v(31.84, -52.34) * mm, "end": v(31.78, -52.08) * mm});
            skLineSegment(sketch, "E1574", {"start": v(31.78, -52.08) * mm, "end": v(31.72, -51.83) * mm});
            skLineSegment(sketch, "E1575", {"start": v(31.72, -51.83) * mm, "end": v(31.66, -51.6) * mm});
            skLineSegment(sketch, "E1576", {"start": v(31.66, -51.6) * mm, "end": v(31.6, -51.37) * mm});
            skLineSegment(sketch, "E1577", {"start": v(31.6, -51.37) * mm, "end": v(31.54, -51.15) * mm});
            skLineSegment(sketch, "E1578", {"start": v(31.54, -51.15) * mm, "end": v(31.48, -50.95) * mm});
            skLineSegment(sketch, "E1579", {"start": v(31.48, -50.95) * mm, "end": v(31.42, -50.76) * mm});
            skLineSegment(sketch, "E1580", {"start": v(31.42, -50.76) * mm, "end": v(31.37, -50.57) * mm});
            skLineSegment(sketch, "E1581", {"start": v(31.37, -50.57) * mm, "end": v(31.3, -50.4) * mm});
            skLineSegment(sketch, "E1582", {"start": v(31.3, -50.4) * mm, "end": v(31.42, -50.17) * mm});
            skLineSegment(sketch, "E1583", {"start": v(31.42, -50.17) * mm, "end": v(33.63, -48.72) * mm});
            skLineSegment(sketch, "E1584", {"start": v(33.63, -48.72) * mm, "end": v(33.9, -48.7) * mm});
            skLineSegment(sketch, "E1585", {"start": v(33.9, -48.7) * mm, "end": v(34.02, -48.82) * mm});
            skLineSegment(sketch, "E1586", {"start": v(34.02, -48.82) * mm, "end": v(34.17, -48.95) * mm});
            skLineSegment(sketch, "E1587", {"start": v(34.17, -48.95) * mm, "end": v(34.32, -49.08) * mm});
            skLineSegment(sketch, "E1588", {"start": v(34.32, -49.08) * mm, "end": v(34.49, -49.22) * mm});
            skLineSegment(sketch, "E1589", {"start": v(34.49, -49.22) * mm, "end": v(34.66, -49.36) * mm});
            skLineSegment(sketch, "E1590", {"start": v(34.66, -49.36) * mm, "end": v(34.84, -49.5) * mm});
            skLineSegment(sketch, "E1591", {"start": v(34.84, -49.5) * mm, "end": v(35.04, -49.65) * mm});
            skLineSegment(sketch, "E1592", {"start": v(35.04, -49.65) * mm, "end": v(35.24, -49.8) * mm});
            skLineSegment(sketch, "E1593", {"start": v(35.24, -49.8) * mm, "end": v(35.46, -49.96) * mm});
            skLineSegment(sketch, "E1594", {"start": v(35.46, -49.96) * mm, "end": v(35.68, -50.12) * mm});
            skLineSegment(sketch, "E1595", {"start": v(35.68, -50.12) * mm, "end": v(35.92, -50.28) * mm});
            skLineSegment(sketch, "E1596", {"start": v(35.92, -50.28) * mm, "end": v(36.17, -50.44) * mm});
            skLineSegment(sketch, "E1597", {"start": v(36.17, -50.44) * mm, "end": v(36.42, -50.6) * mm});
            skLineSegment(sketch, "E1598", {"start": v(36.42, -50.6) * mm, "end": v(36.7, -50.77) * mm});
            skLineSegment(sketch, "E1599", {"start": v(36.7, -50.77) * mm, "end": v(36.97, -50.94) * mm});
            skLineSegment(sketch, "E1600", {"start": v(36.97, -50.94) * mm, "end": v(37.26, -51.12) * mm});
            skLineSegment(sketch, "E1601", {"start": v(37.26, -51.12) * mm, "end": v(37.57, -51.29) * mm});
            skLineSegment(sketch, "E1602", {"start": v(37.57, -51.29) * mm, "end": v(37.88, -51.46) * mm});
            skLineSegment(sketch, "E1603", {"start": v(37.88, -51.46) * mm, "end": v(38.2, -51.64) * mm});
            skLineSegment(sketch, "E1604", {"start": v(38.2, -51.64) * mm, "end": v(38.54, -51.81) * mm});
            skLineSegment(sketch, "E1605", {"start": v(38.54, -51.81) * mm, "end": v(38.9, -51.99) * mm});
            skLineSegment(sketch, "E1606", {"start": v(38.9, -51.99) * mm, "end": v(39.25, -52.16) * mm});
            skLineSegment(sketch, "E1607", {"start": v(39.25, -52.16) * mm, "end": v(39.62, -52.33) * mm});
            skLineSegment(sketch, "E1608", {"start": v(39.62, -52.33) * mm, "end": v(40, -52.5) * mm});
            skLineSegment(sketch, "E1609", {"start": v(40, -52.5) * mm, "end": v(40.4, -52.68) * mm});
            skLineSegment(sketch, "E1610", {"start": v(40.4, -52.68) * mm, "end": v(40.81, -52.85) * mm});
            skLineSegment(sketch, "E1611", {"start": v(40.81, -52.85) * mm, "end": v(41.23, -53.02) * mm});
            skLineSegment(sketch, "E1612", {"start": v(41.23, -53.02) * mm, "end": v(41.66, -53.19) * mm});
            skLineSegment(sketch, "E1613", {"start": v(41.66, -53.19) * mm, "end": v(42.1, -53.35) * mm});
            skLineSegment(sketch, "E1614", {"start": v(42.1, -53.35) * mm, "end": v(42.56, -53.52) * mm});
            skLineSegment(sketch, "E1615", {"start": v(42.56, -53.52) * mm, "end": v(43.03, -53.68) * mm});
            skLineSegment(sketch, "E1616", {"start": v(43.03, -53.68) * mm, "end": v(43.5, -53.83) * mm});
            skLineSegment(sketch, "E1617", {"start": v(43.5, -53.83) * mm, "end": v(44, -53.99) * mm});
            skLineSegment(sketch, "E1618", {"start": v(44, -53.99) * mm, "end": v(44.41, -54.03) * mm});
            skLineSegment(sketch, "E1619", {"start": v(44.41, -54.03) * mm, "end": v(45.98, -52.7) * mm});
            skLineSegment(sketch, "E1620", {"start": v(45.98, -52.7) * mm, "end": v(46, -52.29) * mm});
            skLineSegment(sketch, "E1621", {"start": v(46, -52.29) * mm, "end": v(45.94, -51.78) * mm});
            skLineSegment(sketch, "E1622", {"start": v(45.94, -51.78) * mm, "end": v(45.86, -51.28) * mm});
            skLineSegment(sketch, "E1623", {"start": v(45.86, -51.28) * mm, "end": v(45.78, -50.8) * mm});
            skLineSegment(sketch, "E1624", {"start": v(45.78, -50.8) * mm, "end": v(45.7, -50.32) * mm});
            skLineSegment(sketch, "E1625", {"start": v(45.7, -50.32) * mm, "end": v(45.6, -49.85) * mm});
            skLineSegment(sketch, "E1626", {"start": v(45.6, -49.85) * mm, "end": v(45.5, -49.4) * mm});
            skLineSegment(sketch, "E1627", {"start": v(45.5, -49.4) * mm, "end": v(45.41, -48.96) * mm});
            skLineSegment(sketch, "E1628", {"start": v(45.41, -48.96) * mm, "end": v(45.3, -48.52) * mm});
            skLineSegment(sketch, "E1629", {"start": v(45.3, -48.52) * mm, "end": v(45.2, -48.1) * mm});
            skLineSegment(sketch, "E1630", {"start": v(45.2, -48.1) * mm, "end": v(45.1, -47.7) * mm});
            skLineSegment(sketch, "E1631", {"start": v(45.1, -47.7) * mm, "end": v(44.99, -47.3) * mm});
            skLineSegment(sketch, "E1632", {"start": v(44.99, -47.3) * mm, "end": v(44.87, -46.92) * mm});
            skLineSegment(sketch, "E1633", {"start": v(44.87, -46.92) * mm, "end": v(44.76, -46.54) * mm});
            skLineSegment(sketch, "E1634", {"start": v(44.76, -46.54) * mm, "end": v(44.64, -46.18) * mm});
            skLineSegment(sketch, "E1635", {"start": v(44.64, -46.18) * mm, "end": v(44.52, -45.83) * mm});
            skLineSegment(sketch, "E1636", {"start": v(44.52, -45.83) * mm, "end": v(44.4, -45.5) * mm});
            skLineSegment(sketch, "E1637", {"start": v(44.4, -45.5) * mm, "end": v(44.28, -45.17) * mm});
            skLineSegment(sketch, "E1638", {"start": v(44.28, -45.17) * mm, "end": v(44.16, -44.85) * mm});
            skLineSegment(sketch, "E1639", {"start": v(44.16, -44.85) * mm, "end": v(44.04, -44.55) * mm});
            skLineSegment(sketch, "E1640", {"start": v(44.04, -44.55) * mm, "end": v(43.92, -44.26) * mm});
            skLineSegment(sketch, "E1641", {"start": v(43.92, -44.26) * mm, "end": v(43.8, -43.98) * mm});
            skLineSegment(sketch, "E1642", {"start": v(43.8, -43.98) * mm, "end": v(43.68, -43.7) * mm});
            skLineSegment(sketch, "E1643", {"start": v(43.68, -43.7) * mm, "end": v(43.56, -43.45) * mm});
            skLineSegment(sketch, "E1644", {"start": v(43.56, -43.45) * mm, "end": v(43.44, -43.2) * mm});
            skLineSegment(sketch, "E1645", {"start": v(43.44, -43.2) * mm, "end": v(43.32, -42.96) * mm});
            skLineSegment(sketch, "E1646", {"start": v(43.32, -42.96) * mm, "end": v(43.2, -42.73) * mm});
            skLineSegment(sketch, "E1647", {"start": v(43.2, -42.73) * mm, "end": v(43.1, -42.52) * mm});
            skLineSegment(sketch, "E1648", {"start": v(43.1, -42.52) * mm, "end": v(42.98, -42.31) * mm});
            skLineSegment(sketch, "E1649", {"start": v(42.98, -42.31) * mm, "end": v(42.87, -42.12) * mm});
            skLineSegment(sketch, "E1650", {"start": v(42.87, -42.12) * mm, "end": v(42.76, -41.93) * mm});
            skLineSegment(sketch, "E1651", {"start": v(42.76, -41.93) * mm, "end": v(42.66, -41.76) * mm});
            skLineSegment(sketch, "E1652", {"start": v(42.66, -41.76) * mm, "end": v(42.56, -41.6) * mm});
            skLineSegment(sketch, "E1653", {"start": v(42.56, -41.6) * mm, "end": v(42.46, -41.44) * mm});
            skLineSegment(sketch, "E1654", {"start": v(42.46, -41.44) * mm, "end": v(42.52, -41.19) * mm});
            skLineSegment(sketch, "E1655", {"start": v(42.52, -41.19) * mm, "end": v(44.31, -39.25) * mm});
            skLineSegment(sketch, "E1656", {"start": v(44.31, -39.25) * mm, "end": v(44.56, -39.18) * mm});
            skLineSegment(sketch, "E1657", {"start": v(44.56, -39.18) * mm, "end": v(44.72, -39.26) * mm});
            skLineSegment(sketch, "E1658", {"start": v(44.72, -39.26) * mm, "end": v(44.9, -39.35) * mm});
            skLineSegment(sketch, "E1659", {"start": v(44.9, -39.35) * mm, "end": v(45.07, -39.44) * mm});
            skLineSegment(sketch, "E1660", {"start": v(45.07, -39.44) * mm, "end": v(45.26, -39.53) * mm});
            skLineSegment(sketch, "E1661", {"start": v(45.26, -39.53) * mm, "end": v(45.46, -39.63) * mm});
            skLineSegment(sketch, "E1662", {"start": v(45.46, -39.63) * mm, "end": v(45.68, -39.73) * mm});
            skLineSegment(sketch, "E1663", {"start": v(45.68, -39.73) * mm, "end": v(45.9, -39.82) * mm});
            skLineSegment(sketch, "E1664", {"start": v(45.9, -39.82) * mm, "end": v(46.14, -39.92) * mm});
            skLineSegment(sketch, "E1665", {"start": v(46.14, -39.92) * mm, "end": v(46.38, -40.02) * mm});
            skLineSegment(sketch, "E1666", {"start": v(46.38, -40.02) * mm, "end": v(46.64, -40.12) * mm});
            skLineSegment(sketch, "E1667", {"start": v(46.64, -40.12) * mm, "end": v(46.9, -40.22) * mm});
            skLineSegment(sketch, "E1668", {"start": v(46.9, -40.22) * mm, "end": v(47.19, -40.32) * mm});
            skLineSegment(sketch, "E1669", {"start": v(47.19, -40.32) * mm, "end": v(47.48, -40.42) * mm});
            skLineSegment(sketch, "E1670", {"start": v(47.48, -40.42) * mm, "end": v(47.78, -40.52) * mm});
            skLineSegment(sketch, "E1671", {"start": v(47.78, -40.52) * mm, "end": v(48.09, -40.62) * mm});
            skLineSegment(sketch, "E1672", {"start": v(48.09, -40.62) * mm, "end": v(48.41, -40.71) * mm});
            skLineSegment(sketch, "E1673", {"start": v(48.41, -40.71) * mm, "end": v(48.75, -40.8) * mm});
            skLineSegment(sketch, "E1674", {"start": v(48.75, -40.8) * mm, "end": v(49.1, -40.9) * mm});
            skLineSegment(sketch, "E1675", {"start": v(49.1, -40.9) * mm, "end": v(49.45, -41) * mm});
            skLineSegment(sketch, "E1676", {"start": v(49.45, -41) * mm, "end": v(49.82, -41.08) * mm});
            skLineSegment(sketch, "E1677", {"start": v(49.82, -41.08) * mm, "end": v(50.2, -41.17) * mm});
            skLineSegment(sketch, "E1678", {"start": v(50.2, -41.17) * mm, "end": v(50.6, -41.25) * mm});
            skLineSegment(sketch, "E1679", {"start": v(50.6, -41.25) * mm, "end": v(51, -41.33) * mm});
            skLineSegment(sketch, "E1680", {"start": v(51, -41.33) * mm, "end": v(51.41, -41.4) * mm});
            skLineSegment(sketch, "E1681", {"start": v(51.41, -41.4) * mm, "end": v(51.84, -41.48) * mm});
            skLineSegment(sketch, "E1682", {"start": v(51.84, -41.48) * mm, "end": v(52.27, -41.55) * mm});
            skLineSegment(sketch, "E1683", {"start": v(52.27, -41.55) * mm, "end": v(52.72, -41.61) * mm});
            skLineSegment(sketch, "E1684", {"start": v(52.72, -41.61) * mm, "end": v(53.18, -41.67) * mm});
            skLineSegment(sketch, "E1685", {"start": v(53.18, -41.67) * mm, "end": v(53.65, -41.73) * mm});
            skLineSegment(sketch, "E1686", {"start": v(53.65, -41.73) * mm, "end": v(54.13, -41.78) * mm});
            skLineSegment(sketch, "E1687", {"start": v(54.13, -41.78) * mm, "end": v(54.63, -41.82) * mm});
            skLineSegment(sketch, "E1688", {"start": v(54.63, -41.82) * mm, "end": v(55.13, -41.86) * mm});
            skLineSegment(sketch, "E1689", {"start": v(55.13, -41.86) * mm, "end": v(55.64, -41.89) * mm});
            skLineSegment(sketch, "E1690", {"start": v(55.64, -41.89) * mm, "end": v(56.05, -41.83) * mm});
            skLineSegment(sketch, "E1691", {"start": v(56.05, -41.83) * mm, "end": v(57.25, -40.17) * mm});
            skLineSegment(sketch, "E1692", {"start": v(57.25, -40.17) * mm, "end": v(57.19, -39.76) * mm});
            skLineSegment(sketch, "E1693", {"start": v(57.19, -39.76) * mm, "end": v(57, -39.28) * mm});
            skLineSegment(sketch, "E1694", {"start": v(57, -39.28) * mm, "end": v(56.8, -38.81) * mm});
            skLineSegment(sketch, "E1695", {"start": v(56.8, -38.81) * mm, "end": v(56.6, -38.36) * mm});
            skLineSegment(sketch, "E1696", {"start": v(56.6, -38.36) * mm, "end": v(56.4, -37.92) * mm});
            skLineSegment(sketch, "E1697", {"start": v(56.4, -37.92) * mm, "end": v(56.2, -37.49) * mm});
            skLineSegment(sketch, "E1698", {"start": v(56.2, -37.49) * mm, "end": v(56, -37.07) * mm});
            skLineSegment(sketch, "E1699", {"start": v(56, -37.07) * mm, "end": v(55.8, -36.66) * mm});
            skLineSegment(sketch, "E1700", {"start": v(55.8, -36.66) * mm, "end": v(55.6, -36.27) * mm});
            skLineSegment(sketch, "E1701", {"start": v(55.6, -36.27) * mm, "end": v(55.4, -35.89) * mm});
            skLineSegment(sketch, "E1702", {"start": v(55.4, -35.89) * mm, "end": v(55.2, -35.52) * mm});
            skLineSegment(sketch, "E1703", {"start": v(55.2, -35.52) * mm, "end": v(55, -35.16) * mm});
            skLineSegment(sketch, "E1704", {"start": v(55, -35.16) * mm, "end": v(54.8, -34.82) * mm});
            skLineSegment(sketch, "E1705", {"start": v(54.8, -34.82) * mm, "end": v(54.6, -34.48) * mm});
            skLineSegment(sketch, "E1706", {"start": v(54.6, -34.48) * mm, "end": v(54.4, -34.16) * mm});
            skLineSegment(sketch, "E1707", {"start": v(54.4, -34.16) * mm, "end": v(54.2, -33.85) * mm});
            skLineSegment(sketch, "E1708", {"start": v(54.2, -33.85) * mm, "end": v(54, -33.55) * mm});
            skLineSegment(sketch, "E1709", {"start": v(54, -33.55) * mm, "end": v(53.8, -33.26) * mm});
            skLineSegment(sketch, "E1710", {"start": v(53.8, -33.26) * mm, "end": v(53.61, -32.98) * mm});
            skLineSegment(sketch, "E1711", {"start": v(53.61, -32.98) * mm, "end": v(53.42, -32.72) * mm});
            skLineSegment(sketch, "E1712", {"start": v(53.42, -32.72) * mm, "end": v(53.24, -32.46) * mm});
            skLineSegment(sketch, "E1713", {"start": v(53.24, -32.46) * mm, "end": v(53.05, -32.22) * mm});
            skLineSegment(sketch, "E1714", {"start": v(53.05, -32.22) * mm, "end": v(52.87, -31.98) * mm});
            skLineSegment(sketch, "E1715", {"start": v(52.87, -31.98) * mm, "end": v(52.69, -31.76) * mm});
            skLineSegment(sketch, "E1716", {"start": v(52.69, -31.76) * mm, "end": v(52.51, -31.55) * mm});
            skLineSegment(sketch, "E1717", {"start": v(52.51, -31.55) * mm, "end": v(52.34, -31.34) * mm});
            skLineSegment(sketch, "E1718", {"start": v(52.34, -31.34) * mm, "end": v(52.18, -31.15) * mm});
            skLineSegment(sketch, "E1719", {"start": v(52.18, -31.15) * mm, "end": v(52.01, -30.97) * mm});
            skLineSegment(sketch, "E1720", {"start": v(52.01, -30.97) * mm, "end": v(51.86, -30.8) * mm});
            skLineSegment(sketch, "E1721", {"start": v(51.86, -30.8) * mm, "end": v(51.7, -30.64) * mm});
            skLineSegment(sketch, "E1722", {"start": v(51.7, -30.64) * mm, "end": v(51.55, -30.48) * mm});
            skLineSegment(sketch, "E1723", {"start": v(51.55, -30.48) * mm, "end": v(51.41, -30.34) * mm});
            skLineSegment(sketch, "E1724", {"start": v(51.41, -30.34) * mm, "end": v(51.28, -30.2) * mm});
            skLineSegment(sketch, "E1725", {"start": v(51.28, -30.2) * mm, "end": v(51.14, -30.08) * mm});
            skLineSegment(sketch, "E1726", {"start": v(51.14, -30.08) * mm, "end": v(51.14, -29.82) * mm});
            skLineSegment(sketch, "E1727", {"start": v(51.14, -29.82) * mm, "end": v(52.42, -27.51) * mm});
            skLineSegment(sketch, "E1728", {"start": v(52.42, -27.51) * mm, "end": v(52.64, -27.38) * mm});
            skLineSegment(sketch, "E1729", {"start": v(52.64, -27.38) * mm, "end": v(52.82, -27.42) * mm});
            skLineSegment(sketch, "E1730", {"start": v(52.82, -27.42) * mm, "end": v(53, -27.47) * mm});
            skLineSegment(sketch, "E1731", {"start": v(53, -27.47) * mm, "end": v(53.2, -27.51) * mm});
            skLineSegment(sketch, "E1732", {"start": v(53.2, -27.51) * mm, "end": v(53.4, -27.55) * mm});
            skLineSegment(sketch, "E1733", {"start": v(53.4, -27.55) * mm, "end": v(53.63, -27.6) * mm});
            skLineSegment(sketch, "E1734", {"start": v(53.63, -27.6) * mm, "end": v(53.86, -27.64) * mm});
            skLineSegment(sketch, "E1735", {"start": v(53.86, -27.64) * mm, "end": v(54.1, -27.68) * mm});
            skLineSegment(sketch, "E1736", {"start": v(54.1, -27.68) * mm, "end": v(54.35, -27.72) * mm});
            skLineSegment(sketch, "E1737", {"start": v(54.35, -27.72) * mm, "end": v(54.61, -27.76) * mm});
            skLineSegment(sketch, "E1738", {"start": v(54.61, -27.76) * mm, "end": v(54.88, -27.8) * mm});
            skLineSegment(sketch, "E1739", {"start": v(54.88, -27.8) * mm, "end": v(55.17, -27.83) * mm});
            skLineSegment(sketch, "E1740", {"start": v(55.17, -27.83) * mm, "end": v(55.46, -27.86) * mm});
            skLineSegment(sketch, "E1741", {"start": v(55.46, -27.86) * mm, "end": v(55.77, -27.88) * mm});
            skLineSegment(sketch, "E1742", {"start": v(55.77, -27.88) * mm, "end": v(56.08, -27.9) * mm});
            skLineSegment(sketch, "E1743", {"start": v(56.08, -27.9) * mm, "end": v(56.41, -27.93) * mm});
            skLineSegment(sketch, "E1744", {"start": v(56.41, -27.93) * mm, "end": v(56.75, -27.94) * mm});
            skLineSegment(sketch, "E1745", {"start": v(56.75, -27.94) * mm, "end": v(57.1, -27.96) * mm});
            skLineSegment(sketch, "E1746", {"start": v(57.1, -27.96) * mm, "end": v(57.46, -27.96) * mm});
            skLineSegment(sketch, "E1747", {"start": v(57.46, -27.96) * mm, "end": v(57.83, -27.97) * mm});
            skLineSegment(sketch, "E1748", {"start": v(57.83, -27.97) * mm, "end": v(58.2, -27.96) * mm});
            skLineSegment(sketch, "E1749", {"start": v(58.2, -27.96) * mm, "end": v(58.6, -27.96) * mm});
            skLineSegment(sketch, "E1750", {"start": v(58.6, -27.96) * mm, "end": v(59, -27.94) * mm});
            skLineSegment(sketch, "E1751", {"start": v(59, -27.94) * mm, "end": v(59.4, -27.93) * mm});
            skLineSegment(sketch, "E1752", {"start": v(59.4, -27.93) * mm, "end": v(59.83, -27.9) * mm});
            skLineSegment(sketch, "E1753", {"start": v(59.83, -27.9) * mm, "end": v(60.26, -27.87) * mm});
            skLineSegment(sketch, "E1754", {"start": v(60.26, -27.87) * mm, "end": v(60.7, -27.83) * mm});
            skLineSegment(sketch, "E1755", {"start": v(60.7, -27.83) * mm, "end": v(61.15, -27.79) * mm});
            skLineSegment(sketch, "E1756", {"start": v(61.15, -27.79) * mm, "end": v(61.6, -27.73) * mm});
            skLineSegment(sketch, "E1757", {"start": v(61.6, -27.73) * mm, "end": v(62.08, -27.67) * mm});
            skLineSegment(sketch, "E1758", {"start": v(62.08, -27.67) * mm, "end": v(62.56, -27.6) * mm});
            skLineSegment(sketch, "E1759", {"start": v(62.56, -27.6) * mm, "end": v(63.05, -27.53) * mm});
            skLineSegment(sketch, "E1760", {"start": v(63.05, -27.53) * mm, "end": v(63.54, -27.45) * mm});
            skLineSegment(sketch, "E1761", {"start": v(63.54, -27.45) * mm, "end": v(64.05, -27.36) * mm});
            skLineSegment(sketch, "E1762", {"start": v(64.05, -27.36) * mm, "end": v(64.43, -27.2) * mm});
            skLineSegment(sketch, "E1763", {"start": v(64.43, -27.2) * mm, "end": v(65.2, -25.3) * mm});
            skLineSegment(sketch, "E1764", {"start": v(65.2, -25.3) * mm, "end": v(65.04, -24.92) * mm});
            skLineSegment(sketch, "E1765", {"start": v(65.04, -24.92) * mm, "end": v(64.74, -24.5) * mm});
            skLineSegment(sketch, "E1766", {"start": v(64.74, -24.5) * mm, "end": v(64.44, -24.1) * mm});
            skLineSegment(sketch, "E1767", {"start": v(64.44, -24.1) * mm, "end": v(64.14, -23.7) * mm});
            skLineSegment(sketch, "E1768", {"start": v(64.14, -23.7) * mm, "end": v(63.84, -23.32) * mm});
            skLineSegment(sketch, "E1769", {"start": v(63.84, -23.32) * mm, "end": v(63.55, -22.95) * mm});
            skLineSegment(sketch, "E1770", {"start": v(63.55, -22.95) * mm, "end": v(63.25, -22.59) * mm});
            skLineSegment(sketch, "E1771", {"start": v(63.25, -22.59) * mm, "end": v(62.96, -22.24) * mm});
            skLineSegment(sketch, "E1772", {"start": v(62.96, -22.24) * mm, "end": v(62.67, -21.91) * mm});
            skLineSegment(sketch, "E1773", {"start": v(62.67, -21.91) * mm, "end": v(62.38, -21.59) * mm});
            skLineSegment(sketch, "E1774", {"start": v(62.38, -21.59) * mm, "end": v(62.1, -21.28) * mm});
            skLineSegment(sketch, "E1775", {"start": v(62.1, -21.28) * mm, "end": v(61.82, -20.98) * mm});
            skLineSegment(sketch, "E1776", {"start": v(61.82, -20.98) * mm, "end": v(61.54, -20.7) * mm});
            skLineSegment(sketch, "E1777", {"start": v(61.54, -20.7) * mm, "end": v(61.26, -20.41) * mm});
            skLineSegment(sketch, "E1778", {"start": v(61.26, -20.41) * mm, "end": v(61, -20.15) * mm});
            skLineSegment(sketch, "E1779", {"start": v(61, -20.15) * mm, "end": v(60.72, -19.9) * mm});
            skLineSegment(sketch, "E1780", {"start": v(60.72, -19.9) * mm, "end": v(60.46, -19.65) * mm});
            skLineSegment(sketch, "E1781", {"start": v(60.46, -19.65) * mm, "end": v(60.2, -19.42) * mm});
            skLineSegment(sketch, "E1782", {"start": v(60.2, -19.42) * mm, "end": v(59.95, -19.2) * mm});
            skLineSegment(sketch, "E1783", {"start": v(59.95, -19.2) * mm, "end": v(59.7, -18.98) * mm});
            skLineSegment(sketch, "E1784", {"start": v(59.7, -18.98) * mm, "end": v(59.46, -18.78) * mm});
            skLineSegment(sketch, "E1785", {"start": v(59.46, -18.78) * mm, "end": v(59.22, -18.58) * mm});
            skLineSegment(sketch, "E1786", {"start": v(59.22, -18.58) * mm, "end": v(58.99, -18.4) * mm});
            skLineSegment(sketch, "E1787", {"start": v(58.99, -18.4) * mm, "end": v(58.76, -18.23) * mm});
            skLineSegment(sketch, "E1788", {"start": v(58.76, -18.23) * mm, "end": v(58.54, -18.06) * mm});
            skLineSegment(sketch, "E1789", {"start": v(58.54, -18.06) * mm, "end": v(58.32, -17.9) * mm});
            skLineSegment(sketch, "E1790", {"start": v(58.32, -17.9) * mm, "end": v(58.12, -17.76) * mm});
            skLineSegment(sketch, "E1791", {"start": v(58.12, -17.76) * mm, "end": v(57.91, -17.62) * mm});
            skLineSegment(sketch, "E1792", {"start": v(57.91, -17.62) * mm, "end": v(57.72, -17.5) * mm});
            skLineSegment(sketch, "E1793", {"start": v(57.72, -17.5) * mm, "end": v(57.53, -17.37) * mm});
            skLineSegment(sketch, "E1794", {"start": v(57.53, -17.37) * mm, "end": v(57.35, -17.26) * mm});
            skLineSegment(sketch, "E1795", {"start": v(57.35, -17.26) * mm, "end": v(57.18, -17.15) * mm});
            skLineSegment(sketch, "E1796", {"start": v(57.18, -17.15) * mm, "end": v(57.01, -17.06) * mm});
            skLineSegment(sketch, "E1797", {"start": v(57.01, -17.06) * mm, "end": v(56.86, -16.97) * mm});
            skLineSegment(sketch, "E1798", {"start": v(56.86, -16.97) * mm, "end": v(56.79, -16.71) * mm});
            skLineSegment(sketch, "E1799", {"start": v(56.79, -16.71) * mm, "end": v(57.48, -14.17) * mm});
            skLineSegment(sketch, "E1800", {"start": v(57.48, -14.17) * mm, "end": v(57.66, -13.98) * mm});
            skLineSegment(sketch, "E1801", {"start": v(57.66, -13.98) * mm, "end": v(57.84, -13.98) * mm});
            skLineSegment(sketch, "E1802", {"start": v(57.84, -13.98) * mm, "end": v(58.04, -13.98) * mm});
            skLineSegment(sketch, "E1803", {"start": v(58.04, -13.98) * mm, "end": v(58.24, -13.98) * mm});
            skLineSegment(sketch, "E1804", {"start": v(58.24, -13.98) * mm, "end": v(58.45, -13.97) * mm});
            skLineSegment(sketch, "E1805", {"start": v(58.45, -13.97) * mm, "end": v(58.67, -13.96) * mm});
            skLineSegment(sketch, "E1806", {"start": v(58.67, -13.96) * mm, "end": v(58.9, -13.95) * mm});
            skLineSegment(sketch, "E1807", {"start": v(58.9, -13.95) * mm, "end": v(59.15, -13.93) * mm});
            skLineSegment(sketch, "E1808", {"start": v(59.15, -13.93) * mm, "end": v(59.4, -13.9) * mm});
            skLineSegment(sketch, "E1809", {"start": v(59.4, -13.9) * mm, "end": v(59.67, -13.88) * mm});
            skLineSegment(sketch, "E1810", {"start": v(59.67, -13.88) * mm, "end": v(59.94, -13.85) * mm});
            skLineSegment(sketch, "E1811", {"start": v(59.94, -13.85) * mm, "end": v(60.23, -13.81) * mm});
            skLineSegment(sketch, "E1812", {"start": v(60.23, -13.81) * mm, "end": v(60.52, -13.77) * mm});
            skLineSegment(sketch, "E1813", {"start": v(60.52, -13.77) * mm, "end": v(60.82, -13.73) * mm});
            skLineSegment(sketch, "E1814", {"start": v(60.82, -13.73) * mm, "end": v(61.13, -13.67) * mm});
            skLineSegment(sketch, "E1815", {"start": v(61.13, -13.67) * mm, "end": v(61.46, -13.62) * mm});
            skLineSegment(sketch, "E1816", {"start": v(61.46, -13.62) * mm, "end": v(61.79, -13.55) * mm});
            skLineSegment(sketch, "E1817", {"start": v(61.79, -13.55) * mm, "end": v(62.13, -13.48) * mm});
            skLineSegment(sketch, "E1818", {"start": v(62.13, -13.48) * mm, "end": v(62.48, -13.4) * mm});
            skLineSegment(sketch, "E1819", {"start": v(62.48, -13.4) * mm, "end": v(62.84, -13.32) * mm});
            skLineSegment(sketch, "E1820", {"start": v(62.84, -13.32) * mm, "end": v(63.2, -13.22) * mm});
            skLineSegment(sketch, "E1821", {"start": v(63.2, -13.22) * mm, "end": v(63.58, -13.12) * mm});
            skLineSegment(sketch, "E1822", {"start": v(63.58, -13.12) * mm, "end": v(63.97, -13.01) * mm});
            skLineSegment(sketch, "E1823", {"start": v(63.97, -13.01) * mm, "end": v(64.36, -12.9) * mm});
            skLineSegment(sketch, "E1824", {"start": v(64.36, -12.9) * mm, "end": v(64.77, -12.77) * mm});
            skLineSegment(sketch, "E1825", {"start": v(64.77, -12.77) * mm, "end": v(65.18, -12.64) * mm});
            skLineSegment(sketch, "E1826", {"start": v(65.18, -12.64) * mm, "end": v(65.6, -12.5) * mm});
            skLineSegment(sketch, "E1827", {"start": v(65.6, -12.5) * mm, "end": v(66.02, -12.35) * mm});
            skLineSegment(sketch, "E1828", {"start": v(66.02, -12.35) * mm, "end": v(66.46, -12.18) * mm});
            skLineSegment(sketch, "E1829", {"start": v(66.46, -12.18) * mm, "end": v(66.9, -12.01) * mm});
            skLineSegment(sketch, "E1830", {"start": v(66.9, -12.01) * mm, "end": v(67.35, -11.83) * mm});
            skLineSegment(sketch, "E1831", {"start": v(67.35, -11.83) * mm, "end": v(67.8, -11.64) * mm});
            skLineSegment(sketch, "E1832", {"start": v(67.8, -11.64) * mm, "end": v(68.27, -11.44) * mm});
            skLineSegment(sketch, "E1833", {"start": v(68.27, -11.44) * mm, "end": v(68.74, -11.23) * mm});
            skLineSegment(sketch, "E1834", {"start": v(68.74, -11.23) * mm, "end": v(69.07, -10.99) * mm});
            skLineSegment(sketch, "E1835", {"start": v(69.07, -10.99) * mm, "end": v(69.36, -8.96) * mm});
            skLineSegment(sketch, "E1836", {"start": v(69.36, -8.96) * mm, "end": v(69.11, -8.63) * mm});
            skLineSegment(sketch, "E1837", {"start": v(69.11, -8.63) * mm, "end": v(68.72, -8.3) * mm});
            skLineSegment(sketch, "E1838", {"start": v(68.72, -8.3) * mm, "end": v(68.33, -7.97) * mm});
            skLineSegment(sketch, "E1839", {"start": v(68.33, -7.97) * mm, "end": v(67.95, -7.66) * mm});
            skLineSegment(sketch, "E1840", {"start": v(67.95, -7.66) * mm, "end": v(67.57, -7.36) * mm});
            skLineSegment(sketch, "E1841", {"start": v(67.57, -7.36) * mm, "end": v(67.2, -7.07) * mm});
            skLineSegment(sketch, "E1842", {"start": v(67.2, -7.07) * mm, "end": v(66.82, -6.8) * mm});
            skLineSegment(sketch, "E1843", {"start": v(66.82, -6.8) * mm, "end": v(66.45, -6.53) * mm});
            skLineSegment(sketch, "E1844", {"start": v(66.45, -6.53) * mm, "end": v(66.1, -6.27) * mm});
            skLineSegment(sketch, "E1845", {"start": v(66.1, -6.27) * mm, "end": v(65.74, -6.03) * mm});
            skLineSegment(sketch, "E1846", {"start": v(65.74, -6.03) * mm, "end": v(65.39, -5.8) * mm});
            skLineSegment(sketch, "E1847", {"start": v(65.39, -5.8) * mm, "end": v(65.04, -5.57) * mm});
            skLineSegment(sketch, "E1848", {"start": v(65.04, -5.57) * mm, "end": v(64.7, -5.36) * mm});
            skLineSegment(sketch, "E1849", {"start": v(64.7, -5.36) * mm, "end": v(64.37, -5.16) * mm});
            skLineSegment(sketch, "E1850", {"start": v(64.37, -5.16) * mm, "end": v(64.04, -4.97) * mm});
            skLineSegment(sketch, "E1851", {"start": v(64.04, -4.97) * mm, "end": v(63.72, -4.78) * mm});
            skLineSegment(sketch, "E1852", {"start": v(63.72, -4.78) * mm, "end": v(63.4, -4.6) * mm});
            skLineSegment(sketch, "E1853", {"start": v(63.4, -4.6) * mm, "end": v(63.1, -4.44) * mm});
            skLineSegment(sketch, "E1854", {"start": v(63.1, -4.44) * mm, "end": v(62.8, -4.29) * mm});
            skLineSegment(sketch, "E1855", {"start": v(62.8, -4.29) * mm, "end": v(62.5, -4.14) * mm});
            skLineSegment(sketch, "E1856", {"start": v(62.5, -4.14) * mm, "end": v(62.22, -4) * mm});
            skLineSegment(sketch, "E1857", {"start": v(62.22, -4) * mm, "end": v(61.94, -3.87) * mm});
            skLineSegment(sketch, "E1858", {"start": v(61.94, -3.87) * mm, "end": v(61.68, -3.75) * mm});
            skLineSegment(sketch, "E1859", {"start": v(61.68, -3.75) * mm, "end": v(61.41, -3.63) * mm});
            skLineSegment(sketch, "E1860", {"start": v(61.41, -3.63) * mm, "end": v(61.16, -3.53) * mm});
            skLineSegment(sketch, "E1861", {"start": v(61.16, -3.53) * mm, "end": v(60.91, -3.43) * mm});
            skLineSegment(sketch, "E1862", {"start": v(60.91, -3.43) * mm, "end": v(60.68, -3.34) * mm});
            skLineSegment(sketch, "E1863", {"start": v(60.68, -3.34) * mm, "end": v(60.45, -3.25) * mm});
            skLineSegment(sketch, "E1864", {"start": v(60.45, -3.25) * mm, "end": v(60.23, -3.17) * mm});
            skLineSegment(sketch, "E1865", {"start": v(60.23, -3.17) * mm, "end": v(60.02, -3.1) * mm});
            skLineSegment(sketch, "E1866", {"start": v(60.02, -3.1) * mm, "end": v(59.82, -3.03) * mm});
            skLineSegment(sketch, "E1867", {"start": v(59.82, -3.03) * mm, "end": v(59.62, -2.97) * mm});
            skLineSegment(sketch, "E1868", {"start": v(59.62, -2.97) * mm, "end": v(59.44, -2.92) * mm});
            skLineSegment(sketch, "E1869", {"start": v(59.44, -2.92) * mm, "end": v(59.26, -2.87) * mm});
            skLineSegment(sketch, "E1870", {"start": v(59.26, -2.87) * mm, "end": v(59.14, -2.64) * mm});
            skLineSegment(sketch, "E1871", {"start": v(59.14, -2.64) * mm, "end": v(59.2, 0) * mm});
            skSolve(sketch);
        }
        {
            var Q0;
            Q0=makeQuery(id+"F0.imprint","IMPRINT",FACE,{"disambiguationData":[TD([[makeQuery(id+"F0.imprint","IMPRINT",EDGE,{"derivedFrom":sQuery(id+"F0.wireOp",EDGE,"E0")}),1.0]])]});
            extrude(context, id + "F1", {"entities" : qUnion([Q0]), "depth" : 5 * mm});
        }
        {
            var Q0;
            Q0=makeQuery(id+"F1.opExtrude","CAP_FACE",FACE,{"disambiguationData":[OSD([sQuery(id+"F0.wireOp",EDGE,"E0"),sQuery(id+"F0.wireOp",EDGE,"E1"),sQuery(id+"F0.wireOp",EDGE,"E2"),sQuery(id+"F0.wireOp",EDGE,"E3"),sQuery(id+"F0.wireOp",EDGE,"E4"),sQuery(id+"F0.wireOp",EDGE,"E5"),sQuery(id+"F0.wireOp",EDGE,"E6"),sQuery(id+"F0.wireOp",EDGE,"E7"),sQuery(id+"F0.wireOp",EDGE,"E8"),sQuery(id+"F0.wireOp",EDGE,"E9"),sQuery(id+"F0.wireOp",EDGE,"E10"),sQuery(id+"F0.wireOp",EDGE,"E11"),sQuery(id+"F0.wireOp",EDGE,"E12"),sQuery(id+"F0.wireOp",EDGE,"E13"),sQuery(id+"F0.wireOp",EDGE,"E14"),sQuery(id+"F0.wireOp",EDGE,"E15"),sQuery(id+"F0.wireOp",EDGE,"E16"),sQuery(id+"F0.wireOp",EDGE,"E17"),sQuery(id+"F0.wireOp",EDGE,"E18"),sQuery(id+"F0.wireOp",EDGE,"E19"),sQuery(id+"F0.wireOp",EDGE,"E20"),sQuery(id+"F0.wireOp",EDGE,"E21"),sQuery(id+"F0.wireOp",EDGE,"E22"),sQuery(id+"F0.wireOp",EDGE,"E23"),sQuery(id+"F0.wireOp",EDGE,"E24"),sQuery(id+"F0.wireOp",EDGE,"E25"),sQuery(id+"F0.wireOp",EDGE,"E26"),sQuery(id+"F0.wireOp",EDGE,"E27"),sQuery(id+"F0.wireOp",EDGE,"E28"),sQuery(id+"F0.wireOp",EDGE,"E29"),sQuery(id+"F0.wireOp",EDGE,"E30"),sQuery(id+"F0.wireOp",EDGE,"E31"),sQuery(id+"F0.wireOp",EDGE,"E32"),sQuery(id+"F0.wireOp",EDGE,"E33"),sQuery(id+"F0.wireOp",EDGE,"E34"),sQuery(id+"F0.wireOp",EDGE,"E35"),sQuery(id+"F0.wireOp",EDGE,"E36"),sQuery(id+"F0.wireOp",EDGE,"E37"),sQuery(id+"F0.wireOp",EDGE,"E38"),sQuery(id+"F0.wireOp",EDGE,"E39"),sQuery(id+"F0.wireOp",EDGE,"E40"),sQuery(id+"F0.wireOp",EDGE,"E41"),sQuery(id+"F0.wireOp",EDGE,"E42"),sQuery(id+"F0.wireOp",EDGE,"E43"),sQuery(id+"F0.wireOp",EDGE,"E44"),sQuery(id+"F0.wireOp",EDGE,"E45"),sQuery(id+"F0.wireOp",EDGE,"E46"),sQuery(id+"F0.wireOp",EDGE,"E47"),sQuery(id+"F0.wireOp",EDGE,"E48"),sQuery(id+"F0.wireOp",EDGE,"E49"),sQuery(id+"F0.wireOp",EDGE,"E50"),sQuery(id+"F0.wireOp",EDGE,"E51"),sQuery(id+"F0.wireOp",EDGE,"E52"),sQuery(id+"F0.wireOp",EDGE,"E53"),sQuery(id+"F0.wireOp",EDGE,"E54"),sQuery(id+"F0.wireOp",EDGE,"E55"),sQuery(id+"F0.wireOp",EDGE,"E56"),sQuery(id+"F0.wireOp",EDGE,"E57"),sQuery(id+"F0.wireOp",EDGE,"E58"),sQuery(id+"F0.wireOp",EDGE,"E59"),sQuery(id+"F0.wireOp",EDGE,"E60"),sQuery(id+"F0.wireOp",EDGE,"E61"),sQuery(id+"F0.wireOp",EDGE,"E62"),sQuery(id+"F0.wireOp",EDGE,"E63"),sQuery(id+"F0.wireOp",EDGE,"E64"),sQuery(id+"F0.wireOp",EDGE,"E65"),sQuery(id+"F0.wireOp",EDGE,"E66"),sQuery(id+"F0.wireOp",EDGE,"E67"),sQuery(id+"F0.wireOp",EDGE,"E68"),sQuery(id+"F0.wireOp",EDGE,"E69"),sQuery(id+"F0.wireOp",EDGE,"E70"),sQuery(id+"F0.wireOp",EDGE,"E71"),sQuery(id+"F0.wireOp",EDGE,"E72"),sQuery(id+"F0.wireOp",EDGE,"E73"),sQuery(id+"F0.wireOp",EDGE,"E74"),sQuery(id+"F0.wireOp",EDGE,"E75"),sQuery(id+"F0.wireOp",EDGE,"E76"),sQuery(id+"F0.wireOp",EDGE,"E77"),sQuery(id+"F0.wireOp",EDGE,"E78"),sQuery(id+"F0.wireOp",EDGE,"E79"),sQuery(id+"F0.wireOp",EDGE,"E80"),sQuery(id+"F0.wireOp",EDGE,"E81"),sQuery(id+"F0.wireOp",EDGE,"E82"),sQuery(id+"F0.wireOp",EDGE,"E83"),sQuery(id+"F0.wireOp",EDGE,"E84"),sQuery(id+"F0.wireOp",EDGE,"E85"),sQuery(id+"F0.wireOp",EDGE,"E86"),sQuery(id+"F0.wireOp",EDGE,"E87"),sQuery(id+"F0.wireOp",EDGE,"E88"),sQuery(id+"F0.wireOp",EDGE,"E89"),sQuery(id+"F0.wireOp",EDGE,"E90"),sQuery(id+"F0.wireOp",EDGE,"E91"),sQuery(id+"F0.wireOp",EDGE,"E92"),sQuery(id+"F0.wireOp",EDGE,"E93"),sQuery(id+"F0.wireOp",EDGE,"E94"),sQuery(id+"F0.wireOp",EDGE,"E95"),sQuery(id+"F0.wireOp",EDGE,"E96"),sQuery(id+"F0.wireOp",EDGE,"E97"),sQuery(id+"F0.wireOp",EDGE,"E98"),sQuery(id+"F0.wireOp",EDGE,"E99"),sQuery(id+"F0.wireOp",EDGE,"E100"),sQuery(id+"F0.wireOp",EDGE,"E101"),sQuery(id+"F0.wireOp",EDGE,"E102"),sQuery(id+"F0.wireOp",EDGE,"E103"),sQuery(id+"F0.wireOp",EDGE,"E104"),sQuery(id+"F0.wireOp",EDGE,"E105"),sQuery(id+"F0.wireOp",EDGE,"E106"),sQuery(id+"F0.wireOp",EDGE,"E107"),sQuery(id+"F0.wireOp",EDGE,"E108"),sQuery(id+"F0.wireOp",EDGE,"E109"),sQuery(id+"F0.wireOp",EDGE,"E110"),sQuery(id+"F0.wireOp",EDGE,"E111"),sQuery(id+"F0.wireOp",EDGE,"E112"),sQuery(id+"F0.wireOp",EDGE,"E113"),sQuery(id+"F0.wireOp",EDGE,"E114"),sQuery(id+"F0.wireOp",EDGE,"E115"),sQuery(id+"F0.wireOp",EDGE,"E116"),sQuery(id+"F0.wireOp",EDGE,"E117"),sQuery(id+"F0.wireOp",EDGE,"E118"),sQuery(id+"F0.wireOp",EDGE,"E119"),sQuery(id+"F0.wireOp",EDGE,"E120"),sQuery(id+"F0.wireOp",EDGE,"E121"),sQuery(id+"F0.wireOp",EDGE,"E122"),sQuery(id+"F0.wireOp",EDGE,"E123"),sQuery(id+"F0.wireOp",EDGE,"E124"),sQuery(id+"F0.wireOp",EDGE,"E125"),sQuery(id+"F0.wireOp",EDGE,"E126"),sQuery(id+"F0.wireOp",EDGE,"E127"),sQuery(id+"F0.wireOp",EDGE,"E128"),sQuery(id+"F0.wireOp",EDGE,"E129"),sQuery(id+"F0.wireOp",EDGE,"E130"),sQuery(id+"F0.wireOp",EDGE,"E131"),sQuery(id+"F0.wireOp",EDGE,"E132"),sQuery(id+"F0.wireOp",EDGE,"E133"),sQuery(id+"F0.wireOp",EDGE,"E134"),sQuery(id+"F0.wireOp",EDGE,"E135"),sQuery(id+"F0.wireOp",EDGE,"E136"),sQuery(id+"F0.wireOp",EDGE,"E137"),sQuery(id+"F0.wireOp",EDGE,"E138"),sQuery(id+"F0.wireOp",EDGE,"E139"),sQuery(id+"F0.wireOp",EDGE,"E140"),sQuery(id+"F0.wireOp",EDGE,"E141"),sQuery(id+"F0.wireOp",EDGE,"E142"),sQuery(id+"F0.wireOp",EDGE,"E143"),sQuery(id+"F0.wireOp",EDGE,"E144"),sQuery(id+"F0.wireOp",EDGE,"E145"),sQuery(id+"F0.wireOp",EDGE,"E146"),sQuery(id+"F0.wireOp",EDGE,"E147"),sQuery(id+"F0.wireOp",EDGE,"E148"),sQuery(id+"F0.wireOp",EDGE,"E149"),sQuery(id+"F0.wireOp",EDGE,"E150"),sQuery(id+"F0.wireOp",EDGE,"E151"),sQuery(id+"F0.wireOp",EDGE,"E152"),sQuery(id+"F0.wireOp",EDGE,"E153"),sQuery(id+"F0.wireOp",EDGE,"E154"),sQuery(id+"F0.wireOp",EDGE,"E155"),sQuery(id+"F0.wireOp",EDGE,"E156"),sQuery(id+"F0.wireOp",EDGE,"E157"),sQuery(id+"F0.wireOp",EDGE,"E158"),sQuery(id+"F0.wireOp",EDGE,"E159"),sQuery(id+"F0.wireOp",EDGE,"E160"),sQuery(id+"F0.wireOp",EDGE,"E161"),sQuery(id+"F0.wireOp",EDGE,"E162"),sQuery(id+"F0.wireOp",EDGE,"E163"),sQuery(id+"F0.wireOp",EDGE,"E164"),sQuery(id+"F0.wireOp",EDGE,"E165"),sQuery(id+"F0.wireOp",EDGE,"E166"),sQuery(id+"F0.wireOp",EDGE,"E167"),sQuery(id+"F0.wireOp",EDGE,"E168"),sQuery(id+"F0.wireOp",EDGE,"E169"),sQuery(id+"F0.wireOp",EDGE,"E170"),sQuery(id+"F0.wireOp",EDGE,"E171"),sQuery(id+"F0.wireOp",EDGE,"E172"),sQuery(id+"F0.wireOp",EDGE,"E173"),sQuery(id+"F0.wireOp",EDGE,"E174"),sQuery(id+"F0.wireOp",EDGE,"E175"),sQuery(id+"F0.wireOp",EDGE,"E176"),sQuery(id+"F0.wireOp",EDGE,"E177"),sQuery(id+"F0.wireOp",EDGE,"E178"),sQuery(id+"F0.wireOp",EDGE,"E179"),sQuery(id+"F0.wireOp",EDGE,"E180"),sQuery(id+"F0.wireOp",EDGE,"E181"),sQuery(id+"F0.wireOp",EDGE,"E182"),sQuery(id+"F0.wireOp",EDGE,"E183"),sQuery(id+"F0.wireOp",EDGE,"E184"),sQuery(id+"F0.wireOp",EDGE,"E185"),sQuery(id+"F0.wireOp",EDGE,"E186"),sQuery(id+"F0.wireOp",EDGE,"E187"),sQuery(id+"F0.wireOp",EDGE,"E188"),sQuery(id+"F0.wireOp",EDGE,"E189"),sQuery(id+"F0.wireOp",EDGE,"E190"),sQuery(id+"F0.wireOp",EDGE,"E191"),sQuery(id+"F0.wireOp",EDGE,"E192"),sQuery(id+"F0.wireOp",EDGE,"E193"),sQuery(id+"F0.wireOp",EDGE,"E194"),sQuery(id+"F0.wireOp",EDGE,"E195"),sQuery(id+"F0.wireOp",EDGE,"E196"),sQuery(id+"F0.wireOp",EDGE,"E197"),sQuery(id+"F0.wireOp",EDGE,"E198"),sQuery(id+"F0.wireOp",EDGE,"E199"),sQuery(id+"F0.wireOp",EDGE,"E200"),sQuery(id+"F0.wireOp",EDGE,"E201"),sQuery(id+"F0.wireOp",EDGE,"E202"),sQuery(id+"F0.wireOp",EDGE,"E203"),sQuery(id+"F0.wireOp",EDGE,"E204"),sQuery(id+"F0.wireOp",EDGE,"E205"),sQuery(id+"F0.wireOp",EDGE,"E206"),sQuery(id+"F0.wireOp",EDGE,"E207"),sQuery(id+"F0.wireOp",EDGE,"E208"),sQuery(id+"F0.wireOp",EDGE,"E209"),sQuery(id+"F0.wireOp",EDGE,"E210"),sQuery(id+"F0.wireOp",EDGE,"E211"),sQuery(id+"F0.wireOp",EDGE,"E212"),sQuery(id+"F0.wireOp",EDGE,"E213"),sQuery(id+"F0.wireOp",EDGE,"E214"),sQuery(id+"F0.wireOp",EDGE,"E215"),sQuery(id+"F0.wireOp",EDGE,"E216"),sQuery(id+"F0.wireOp",EDGE,"E217"),sQuery(id+"F0.wireOp",EDGE,"E218"),sQuery(id+"F0.wireOp",EDGE,"E219"),sQuery(id+"F0.wireOp",EDGE,"E220"),sQuery(id+"F0.wireOp",EDGE,"E221"),sQuery(id+"F0.wireOp",EDGE,"E222"),sQuery(id+"F0.wireOp",EDGE,"E223"),sQuery(id+"F0.wireOp",EDGE,"E224"),sQuery(id+"F0.wireOp",EDGE,"E225"),sQuery(id+"F0.wireOp",EDGE,"E226"),sQuery(id+"F0.wireOp",EDGE,"E227"),sQuery(id+"F0.wireOp",EDGE,"E228"),sQuery(id+"F0.wireOp",EDGE,"E229"),sQuery(id+"F0.wireOp",EDGE,"E230"),sQuery(id+"F0.wireOp",EDGE,"E231"),sQuery(id+"F0.wireOp",EDGE,"E232"),sQuery(id+"F0.wireOp",EDGE,"E233"),sQuery(id+"F0.wireOp",EDGE,"E234"),sQuery(id+"F0.wireOp",EDGE,"E235"),sQuery(id+"F0.wireOp",EDGE,"E236"),sQuery(id+"F0.wireOp",EDGE,"E237"),sQuery(id+"F0.wireOp",EDGE,"E238"),sQuery(id+"F0.wireOp",EDGE,"E239"),sQuery(id+"F0.wireOp",EDGE,"E240"),sQuery(id+"F0.wireOp",EDGE,"E241"),sQuery(id+"F0.wireOp",EDGE,"E242"),sQuery(id+"F0.wireOp",EDGE,"E243"),sQuery(id+"F0.wireOp",EDGE,"E244"),sQuery(id+"F0.wireOp",EDGE,"E245"),sQuery(id+"F0.wireOp",EDGE,"E246"),sQuery(id+"F0.wireOp",EDGE,"E247"),sQuery(id+"F0.wireOp",EDGE,"E248"),sQuery(id+"F0.wireOp",EDGE,"E249"),sQuery(id+"F0.wireOp",EDGE,"E250"),sQuery(id+"F0.wireOp",EDGE,"E251"),sQuery(id+"F0.wireOp",EDGE,"E252"),sQuery(id+"F0.wireOp",EDGE,"E253"),sQuery(id+"F0.wireOp",EDGE,"E254"),sQuery(id+"F0.wireOp",EDGE,"E255"),sQuery(id+"F0.wireOp",EDGE,"E256"),sQuery(id+"F0.wireOp",EDGE,"E257"),sQuery(id+"F0.wireOp",EDGE,"E258"),sQuery(id+"F0.wireOp",EDGE,"E259"),sQuery(id+"F0.wireOp",EDGE,"E260"),sQuery(id+"F0.wireOp",EDGE,"E261"),sQuery(id+"F0.wireOp",EDGE,"E262"),sQuery(id+"F0.wireOp",EDGE,"E263"),sQuery(id+"F0.wireOp",EDGE,"E264"),sQuery(id+"F0.wireOp",EDGE,"E265"),sQuery(id+"F0.wireOp",EDGE,"E266"),sQuery(id+"F0.wireOp",EDGE,"E267"),sQuery(id+"F0.wireOp",EDGE,"E268"),sQuery(id+"F0.wireOp",EDGE,"E269"),sQuery(id+"F0.wireOp",EDGE,"E270"),sQuery(id+"F0.wireOp",EDGE,"E271"),sQuery(id+"F0.wireOp",EDGE,"E272"),sQuery(id+"F0.wireOp",EDGE,"E273"),sQuery(id+"F0.wireOp",EDGE,"E274"),sQuery(id+"F0.wireOp",EDGE,"E275"),sQuery(id+"F0.wireOp",EDGE,"E276"),sQuery(id+"F0.wireOp",EDGE,"E277"),sQuery(id+"F0.wireOp",EDGE,"E278"),sQuery(id+"F0.wireOp",EDGE,"E279"),sQuery(id+"F0.wireOp",EDGE,"E280"),sQuery(id+"F0.wireOp",EDGE,"E281"),sQuery(id+"F0.wireOp",EDGE,"E282"),sQuery(id+"F0.wireOp",EDGE,"E283"),sQuery(id+"F0.wireOp",EDGE,"E284"),sQuery(id+"F0.wireOp",EDGE,"E285"),sQuery(id+"F0.wireOp",EDGE,"E286"),sQuery(id+"F0.wireOp",EDGE,"E287"),sQuery(id+"F0.wireOp",EDGE,"E288"),sQuery(id+"F0.wireOp",EDGE,"E289"),sQuery(id+"F0.wireOp",EDGE,"E290"),sQuery(id+"F0.wireOp",EDGE,"E291"),sQuery(id+"F0.wireOp",EDGE,"E292"),sQuery(id+"F0.wireOp",EDGE,"E293"),sQuery(id+"F0.wireOp",EDGE,"E294"),sQuery(id+"F0.wireOp",EDGE,"E295"),sQuery(id+"F0.wireOp",EDGE,"E296"),sQuery(id+"F0.wireOp",EDGE,"E297"),sQuery(id+"F0.wireOp",EDGE,"E298"),sQuery(id+"F0.wireOp",EDGE,"E299"),sQuery(id+"F0.wireOp",EDGE,"E300"),sQuery(id+"F0.wireOp",EDGE,"E301"),sQuery(id+"F0.wireOp",EDGE,"E302"),sQuery(id+"F0.wireOp",EDGE,"E303"),sQuery(id+"F0.wireOp",EDGE,"E304"),sQuery(id+"F0.wireOp",EDGE,"E305"),sQuery(id+"F0.wireOp",EDGE,"E306"),sQuery(id+"F0.wireOp",EDGE,"E307"),sQuery(id+"F0.wireOp",EDGE,"E308"),sQuery(id+"F0.wireOp",EDGE,"E309"),sQuery(id+"F0.wireOp",EDGE,"E310"),sQuery(id+"F0.wireOp",EDGE,"E311"),sQuery(id+"F0.wireOp",EDGE,"E312"),sQuery(id+"F0.wireOp",EDGE,"E313"),sQuery(id+"F0.wireOp",EDGE,"E314"),sQuery(id+"F0.wireOp",EDGE,"E315"),sQuery(id+"F0.wireOp",EDGE,"E316"),sQuery(id+"F0.wireOp",EDGE,"E317"),sQuery(id+"F0.wireOp",EDGE,"E318"),sQuery(id+"F0.wireOp",EDGE,"E319"),sQuery(id+"F0.wireOp",EDGE,"E320"),sQuery(id+"F0.wireOp",EDGE,"E321"),sQuery(id+"F0.wireOp",EDGE,"E322"),sQuery(id+"F0.wireOp",EDGE,"E323"),sQuery(id+"F0.wireOp",EDGE,"E324"),sQuery(id+"F0.wireOp",EDGE,"E325"),sQuery(id+"F0.wireOp",EDGE,"E326"),sQuery(id+"F0.wireOp",EDGE,"E327"),sQuery(id+"F0.wireOp",EDGE,"E328"),sQuery(id+"F0.wireOp",EDGE,"E329"),sQuery(id+"F0.wireOp",EDGE,"E330"),sQuery(id+"F0.wireOp",EDGE,"E331"),sQuery(id+"F0.wireOp",EDGE,"E332"),sQuery(id+"F0.wireOp",EDGE,"E333"),sQuery(id+"F0.wireOp",EDGE,"E334"),sQuery(id+"F0.wireOp",EDGE,"E335"),sQuery(id+"F0.wireOp",EDGE,"E336"),sQuery(id+"F0.wireOp",EDGE,"E337"),sQuery(id+"F0.wireOp",EDGE,"E338"),sQuery(id+"F0.wireOp",EDGE,"E339"),sQuery(id+"F0.wireOp",EDGE,"E340"),sQuery(id+"F0.wireOp",EDGE,"E341"),sQuery(id+"F0.wireOp",EDGE,"E342"),sQuery(id+"F0.wireOp",EDGE,"E343"),sQuery(id+"F0.wireOp",EDGE,"E344"),sQuery(id+"F0.wireOp",EDGE,"E345"),sQuery(id+"F0.wireOp",EDGE,"E346"),sQuery(id+"F0.wireOp",EDGE,"E347"),sQuery(id+"F0.wireOp",EDGE,"E348"),sQuery(id+"F0.wireOp",EDGE,"E349"),sQuery(id+"F0.wireOp",EDGE,"E350"),sQuery(id+"F0.wireOp",EDGE,"E351"),sQuery(id+"F0.wireOp",EDGE,"E352"),sQuery(id+"F0.wireOp",EDGE,"E353"),sQuery(id+"F0.wireOp",EDGE,"E354"),sQuery(id+"F0.wireOp",EDGE,"E355"),sQuery(id+"F0.wireOp",EDGE,"E356"),sQuery(id+"F0.wireOp",EDGE,"E357"),sQuery(id+"F0.wireOp",EDGE,"E358"),sQuery(id+"F0.wireOp",EDGE,"E359"),sQuery(id+"F0.wireOp",EDGE,"E360"),sQuery(id+"F0.wireOp",EDGE,"E361"),sQuery(id+"F0.wireOp",EDGE,"E362"),sQuery(id+"F0.wireOp",EDGE,"E363"),sQuery(id+"F0.wireOp",EDGE,"E364"),sQuery(id+"F0.wireOp",EDGE,"E365"),sQuery(id+"F0.wireOp",EDGE,"E366"),sQuery(id+"F0.wireOp",EDGE,"E367"),sQuery(id+"F0.wireOp",EDGE,"E368"),sQuery(id+"F0.wireOp",EDGE,"E369"),sQuery(id+"F0.wireOp",EDGE,"E370"),sQuery(id+"F0.wireOp",EDGE,"E371"),sQuery(id+"F0.wireOp",EDGE,"E372"),sQuery(id+"F0.wireOp",EDGE,"E373"),sQuery(id+"F0.wireOp",EDGE,"E374"),sQuery(id+"F0.wireOp",EDGE,"E375"),sQuery(id+"F0.wireOp",EDGE,"E376"),sQuery(id+"F0.wireOp",EDGE,"E377"),sQuery(id+"F0.wireOp",EDGE,"E378"),sQuery(id+"F0.wireOp",EDGE,"E379"),sQuery(id+"F0.wireOp",EDGE,"E380"),sQuery(id+"F0.wireOp",EDGE,"E381"),sQuery(id+"F0.wireOp",EDGE,"E382"),sQuery(id+"F0.wireOp",EDGE,"E383"),sQuery(id+"F0.wireOp",EDGE,"E384"),sQuery(id+"F0.wireOp",EDGE,"E385"),sQuery(id+"F0.wireOp",EDGE,"E386"),sQuery(id+"F0.wireOp",EDGE,"E387"),sQuery(id+"F0.wireOp",EDGE,"E388"),sQuery(id+"F0.wireOp",EDGE,"E389"),sQuery(id+"F0.wireOp",EDGE,"E390"),sQuery(id+"F0.wireOp",EDGE,"E391"),sQuery(id+"F0.wireOp",EDGE,"E392"),sQuery(id+"F0.wireOp",EDGE,"E393"),sQuery(id+"F0.wireOp",EDGE,"E394"),sQuery(id+"F0.wireOp",EDGE,"E395"),sQuery(id+"F0.wireOp",EDGE,"E396"),sQuery(id+"F0.wireOp",EDGE,"E397"),sQuery(id+"F0.wireOp",EDGE,"E398"),sQuery(id+"F0.wireOp",EDGE,"E399"),sQuery(id+"F0.wireOp",EDGE,"E400"),sQuery(id+"F0.wireOp",EDGE,"E401"),sQuery(id+"F0.wireOp",EDGE,"E402"),sQuery(id+"F0.wireOp",EDGE,"E403"),sQuery(id+"F0.wireOp",EDGE,"E404"),sQuery(id+"F0.wireOp",EDGE,"E405"),sQuery(id+"F0.wireOp",EDGE,"E406"),sQuery(id+"F0.wireOp",EDGE,"E407"),sQuery(id+"F0.wireOp",EDGE,"E408"),sQuery(id+"F0.wireOp",EDGE,"E409"),sQuery(id+"F0.wireOp",EDGE,"E410"),sQuery(id+"F0.wireOp",EDGE,"E411"),sQuery(id+"F0.wireOp",EDGE,"E412"),sQuery(id+"F0.wireOp",EDGE,"E413"),sQuery(id+"F0.wireOp",EDGE,"E414"),sQuery(id+"F0.wireOp",EDGE,"E415"),sQuery(id+"F0.wireOp",EDGE,"E416"),sQuery(id+"F0.wireOp",EDGE,"E417"),sQuery(id+"F0.wireOp",EDGE,"E418"),sQuery(id+"F0.wireOp",EDGE,"E419"),sQuery(id+"F0.wireOp",EDGE,"E420"),sQuery(id+"F0.wireOp",EDGE,"E421"),sQuery(id+"F0.wireOp",EDGE,"E422"),sQuery(id+"F0.wireOp",EDGE,"E423"),sQuery(id+"F0.wireOp",EDGE,"E424"),sQuery(id+"F0.wireOp",EDGE,"E425"),sQuery(id+"F0.wireOp",EDGE,"E426"),sQuery(id+"F0.wireOp",EDGE,"E427"),sQuery(id+"F0.wireOp",EDGE,"E428"),sQuery(id+"F0.wireOp",EDGE,"E429"),sQuery(id+"F0.wireOp",EDGE,"E430"),sQuery(id+"F0.wireOp",EDGE,"E431"),sQuery(id+"F0.wireOp",EDGE,"E432"),sQuery(id+"F0.wireOp",EDGE,"E433"),sQuery(id+"F0.wireOp",EDGE,"E434"),sQuery(id+"F0.wireOp",EDGE,"E435"),sQuery(id+"F0.wireOp",EDGE,"E436"),sQuery(id+"F0.wireOp",EDGE,"E437"),sQuery(id+"F0.wireOp",EDGE,"E438"),sQuery(id+"F0.wireOp",EDGE,"E439"),sQuery(id+"F0.wireOp",EDGE,"E440"),sQuery(id+"F0.wireOp",EDGE,"E441"),sQuery(id+"F0.wireOp",EDGE,"E442"),sQuery(id+"F0.wireOp",EDGE,"E443"),sQuery(id+"F0.wireOp",EDGE,"E444"),sQuery(id+"F0.wireOp",EDGE,"E445"),sQuery(id+"F0.wireOp",EDGE,"E446"),sQuery(id+"F0.wireOp",EDGE,"E447"),sQuery(id+"F0.wireOp",EDGE,"E448"),sQuery(id+"F0.wireOp",EDGE,"E449"),sQuery(id+"F0.wireOp",EDGE,"E450"),sQuery(id+"F0.wireOp",EDGE,"E451"),sQuery(id+"F0.wireOp",EDGE,"E452"),sQuery(id+"F0.wireOp",EDGE,"E453"),sQuery(id+"F0.wireOp",EDGE,"E454"),sQuery(id+"F0.wireOp",EDGE,"E455"),sQuery(id+"F0.wireOp",EDGE,"E456"),sQuery(id+"F0.wireOp",EDGE,"E457"),sQuery(id+"F0.wireOp",EDGE,"E458"),sQuery(id+"F0.wireOp",EDGE,"E459"),sQuery(id+"F0.wireOp",EDGE,"E460"),sQuery(id+"F0.wireOp",EDGE,"E461"),sQuery(id+"F0.wireOp",EDGE,"E462"),sQuery(id+"F0.wireOp",EDGE,"E463"),sQuery(id+"F0.wireOp",EDGE,"E464"),sQuery(id+"F0.wireOp",EDGE,"E465"),sQuery(id+"F0.wireOp",EDGE,"E466"),sQuery(id+"F0.wireOp",EDGE,"E467"),sQuery(id+"F0.wireOp",EDGE,"E468"),sQuery(id+"F0.wireOp",EDGE,"E469"),sQuery(id+"F0.wireOp",EDGE,"E470"),sQuery(id+"F0.wireOp",EDGE,"E471"),sQuery(id+"F0.wireOp",EDGE,"E472"),sQuery(id+"F0.wireOp",EDGE,"E473"),sQuery(id+"F0.wireOp",EDGE,"E474"),sQuery(id+"F0.wireOp",EDGE,"E475"),sQuery(id+"F0.wireOp",EDGE,"E476"),sQuery(id+"F0.wireOp",EDGE,"E477"),sQuery(id+"F0.wireOp",EDGE,"E478"),sQuery(id+"F0.wireOp",EDGE,"E479"),sQuery(id+"F0.wireOp",EDGE,"E480"),sQuery(id+"F0.wireOp",EDGE,"E481"),sQuery(id+"F0.wireOp",EDGE,"E482"),sQuery(id+"F0.wireOp",EDGE,"E483"),sQuery(id+"F0.wireOp",EDGE,"E484"),sQuery(id+"F0.wireOp",EDGE,"E485"),sQuery(id+"F0.wireOp",EDGE,"E486"),sQuery(id+"F0.wireOp",EDGE,"E487"),sQuery(id+"F0.wireOp",EDGE,"E488"),sQuery(id+"F0.wireOp",EDGE,"E489"),sQuery(id+"F0.wireOp",EDGE,"E490"),sQuery(id+"F0.wireOp",EDGE,"E491"),sQuery(id+"F0.wireOp",EDGE,"E492"),sQuery(id+"F0.wireOp",EDGE,"E493"),sQuery(id+"F0.wireOp",EDGE,"E494"),sQuery(id+"F0.wireOp",EDGE,"E495"),sQuery(id+"F0.wireOp",EDGE,"E496"),sQuery(id+"F0.wireOp",EDGE,"E497"),sQuery(id+"F0.wireOp",EDGE,"E498"),sQuery(id+"F0.wireOp",EDGE,"E499"),sQuery(id+"F0.wireOp",EDGE,"E500"),sQuery(id+"F0.wireOp",EDGE,"E501"),sQuery(id+"F0.wireOp",EDGE,"E502"),sQuery(id+"F0.wireOp",EDGE,"E503"),sQuery(id+"F0.wireOp",EDGE,"E504"),sQuery(id+"F0.wireOp",EDGE,"E505"),sQuery(id+"F0.wireOp",EDGE,"E506"),sQuery(id+"F0.wireOp",EDGE,"E507"),sQuery(id+"F0.wireOp",EDGE,"E508"),sQuery(id+"F0.wireOp",EDGE,"E509"),sQuery(id+"F0.wireOp",EDGE,"E510"),sQuery(id+"F0.wireOp",EDGE,"E511"),sQuery(id+"F0.wireOp",EDGE,"E512"),sQuery(id+"F0.wireOp",EDGE,"E513"),sQuery(id+"F0.wireOp",EDGE,"E514"),sQuery(id+"F0.wireOp",EDGE,"E515"),sQuery(id+"F0.wireOp",EDGE,"E516"),sQuery(id+"F0.wireOp",EDGE,"E517"),sQuery(id+"F0.wireOp",EDGE,"E518"),sQuery(id+"F0.wireOp",EDGE,"E519"),sQuery(id+"F0.wireOp",EDGE,"E520"),sQuery(id+"F0.wireOp",EDGE,"E521"),sQuery(id+"F0.wireOp",EDGE,"E522"),sQuery(id+"F0.wireOp",EDGE,"E523"),sQuery(id+"F0.wireOp",EDGE,"E524"),sQuery(id+"F0.wireOp",EDGE,"E525"),sQuery(id+"F0.wireOp",EDGE,"E526"),sQuery(id+"F0.wireOp",EDGE,"E527"),sQuery(id+"F0.wireOp",EDGE,"E528"),sQuery(id+"F0.wireOp",EDGE,"E529"),sQuery(id+"F0.wireOp",EDGE,"E530"),sQuery(id+"F0.wireOp",EDGE,"E531"),sQuery(id+"F0.wireOp",EDGE,"E532"),sQuery(id+"F0.wireOp",EDGE,"E533"),sQuery(id+"F0.wireOp",EDGE,"E534"),sQuery(id+"F0.wireOp",EDGE,"E535"),sQuery(id+"F0.wireOp",EDGE,"E536"),sQuery(id+"F0.wireOp",EDGE,"E537"),sQuery(id+"F0.wireOp",EDGE,"E538"),sQuery(id+"F0.wireOp",EDGE,"E539"),sQuery(id+"F0.wireOp",EDGE,"E540"),sQuery(id+"F0.wireOp",EDGE,"E541"),sQuery(id+"F0.wireOp",EDGE,"E542"),sQuery(id+"F0.wireOp",EDGE,"E543"),sQuery(id+"F0.wireOp",EDGE,"E544"),sQuery(id+"F0.wireOp",EDGE,"E545"),sQuery(id+"F0.wireOp",EDGE,"E546"),sQuery(id+"F0.wireOp",EDGE,"E547"),sQuery(id+"F0.wireOp",EDGE,"E548"),sQuery(id+"F0.wireOp",EDGE,"E549"),sQuery(id+"F0.wireOp",EDGE,"E550"),sQuery(id+"F0.wireOp",EDGE,"E551"),sQuery(id+"F0.wireOp",EDGE,"E552"),sQuery(id+"F0.wireOp",EDGE,"E553"),sQuery(id+"F0.wireOp",EDGE,"E554"),sQuery(id+"F0.wireOp",EDGE,"E555"),sQuery(id+"F0.wireOp",EDGE,"E556"),sQuery(id+"F0.wireOp",EDGE,"E557"),sQuery(id+"F0.wireOp",EDGE,"E558"),sQuery(id+"F0.wireOp",EDGE,"E559"),sQuery(id+"F0.wireOp",EDGE,"E560"),sQuery(id+"F0.wireOp",EDGE,"E561"),sQuery(id+"F0.wireOp",EDGE,"E562"),sQuery(id+"F0.wireOp",EDGE,"E563"),sQuery(id+"F0.wireOp",EDGE,"E564"),sQuery(id+"F0.wireOp",EDGE,"E565"),sQuery(id+"F0.wireOp",EDGE,"E566"),sQuery(id+"F0.wireOp",EDGE,"E567"),sQuery(id+"F0.wireOp",EDGE,"E568"),sQuery(id+"F0.wireOp",EDGE,"E569"),sQuery(id+"F0.wireOp",EDGE,"E570"),sQuery(id+"F0.wireOp",EDGE,"E571"),sQuery(id+"F0.wireOp",EDGE,"E572"),sQuery(id+"F0.wireOp",EDGE,"E573"),sQuery(id+"F0.wireOp",EDGE,"E574"),sQuery(id+"F0.wireOp",EDGE,"E575"),sQuery(id+"F0.wireOp",EDGE,"E576"),sQuery(id+"F0.wireOp",EDGE,"E577"),sQuery(id+"F0.wireOp",EDGE,"E578"),sQuery(id+"F0.wireOp",EDGE,"E579"),sQuery(id+"F0.wireOp",EDGE,"E580"),sQuery(id+"F0.wireOp",EDGE,"E581"),sQuery(id+"F0.wireOp",EDGE,"E582"),sQuery(id+"F0.wireOp",EDGE,"E583"),sQuery(id+"F0.wireOp",EDGE,"E584"),sQuery(id+"F0.wireOp",EDGE,"E585"),sQuery(id+"F0.wireOp",EDGE,"E586"),sQuery(id+"F0.wireOp",EDGE,"E587"),sQuery(id+"F0.wireOp",EDGE,"E588"),sQuery(id+"F0.wireOp",EDGE,"E589"),sQuery(id+"F0.wireOp",EDGE,"E590"),sQuery(id+"F0.wireOp",EDGE,"E591"),sQuery(id+"F0.wireOp",EDGE,"E592"),sQuery(id+"F0.wireOp",EDGE,"E593"),sQuery(id+"F0.wireOp",EDGE,"E594"),sQuery(id+"F0.wireOp",EDGE,"E595"),sQuery(id+"F0.wireOp",EDGE,"E596"),sQuery(id+"F0.wireOp",EDGE,"E597"),sQuery(id+"F0.wireOp",EDGE,"E598"),sQuery(id+"F0.wireOp",EDGE,"E599"),sQuery(id+"F0.wireOp",EDGE,"E600"),sQuery(id+"F0.wireOp",EDGE,"E601"),sQuery(id+"F0.wireOp",EDGE,"E602"),sQuery(id+"F0.wireOp",EDGE,"E603"),sQuery(id+"F0.wireOp",EDGE,"E604"),sQuery(id+"F0.wireOp",EDGE,"E605"),sQuery(id+"F0.wireOp",EDGE,"E606"),sQuery(id+"F0.wireOp",EDGE,"E607"),sQuery(id+"F0.wireOp",EDGE,"E608"),sQuery(id+"F0.wireOp",EDGE,"E609"),sQuery(id+"F0.wireOp",EDGE,"E610"),sQuery(id+"F0.wireOp",EDGE,"E611"),sQuery(id+"F0.wireOp",EDGE,"E612"),sQuery(id+"F0.wireOp",EDGE,"E613"),sQuery(id+"F0.wireOp",EDGE,"E614"),sQuery(id+"F0.wireOp",EDGE,"E615"),sQuery(id+"F0.wireOp",EDGE,"E616"),sQuery(id+"F0.wireOp",EDGE,"E617"),sQuery(id+"F0.wireOp",EDGE,"E618"),sQuery(id+"F0.wireOp",EDGE,"E619"),sQuery(id+"F0.wireOp",EDGE,"E620"),sQuery(id+"F0.wireOp",EDGE,"E621"),sQuery(id+"F0.wireOp",EDGE,"E622"),sQuery(id+"F0.wireOp",EDGE,"E623"),sQuery(id+"F0.wireOp",EDGE,"E624"),sQuery(id+"F0.wireOp",EDGE,"E625"),sQuery(id+"F0.wireOp",EDGE,"E626"),sQuery(id+"F0.wireOp",EDGE,"E627"),sQuery(id+"F0.wireOp",EDGE,"E628"),sQuery(id+"F0.wireOp",EDGE,"E629"),sQuery(id+"F0.wireOp",EDGE,"E630"),sQuery(id+"F0.wireOp",EDGE,"E631"),sQuery(id+"F0.wireOp",EDGE,"E632"),sQuery(id+"F0.wireOp",EDGE,"E633"),sQuery(id+"F0.wireOp",EDGE,"E634"),sQuery(id+"F0.wireOp",EDGE,"E635"),sQuery(id+"F0.wireOp",EDGE,"E636"),sQuery(id+"F0.wireOp",EDGE,"E637"),sQuery(id+"F0.wireOp",EDGE,"E638"),sQuery(id+"F0.wireOp",EDGE,"E639"),sQuery(id+"F0.wireOp",EDGE,"E640"),sQuery(id+"F0.wireOp",EDGE,"E641"),sQuery(id+"F0.wireOp",EDGE,"E642"),sQuery(id+"F0.wireOp",EDGE,"E643"),sQuery(id+"F0.wireOp",EDGE,"E644"),sQuery(id+"F0.wireOp",EDGE,"E645"),sQuery(id+"F0.wireOp",EDGE,"E646"),sQuery(id+"F0.wireOp",EDGE,"E647"),sQuery(id+"F0.wireOp",EDGE,"E648"),sQuery(id+"F0.wireOp",EDGE,"E649"),sQuery(id+"F0.wireOp",EDGE,"E650"),sQuery(id+"F0.wireOp",EDGE,"E651"),sQuery(id+"F0.wireOp",EDGE,"E652"),sQuery(id+"F0.wireOp",EDGE,"E653"),sQuery(id+"F0.wireOp",EDGE,"E654"),sQuery(id+"F0.wireOp",EDGE,"E655"),sQuery(id+"F0.wireOp",EDGE,"E656"),sQuery(id+"F0.wireOp",EDGE,"E657"),sQuery(id+"F0.wireOp",EDGE,"E658"),sQuery(id+"F0.wireOp",EDGE,"E659"),sQuery(id+"F0.wireOp",EDGE,"E660"),sQuery(id+"F0.wireOp",EDGE,"E661"),sQuery(id+"F0.wireOp",EDGE,"E662"),sQuery(id+"F0.wireOp",EDGE,"E663"),sQuery(id+"F0.wireOp",EDGE,"E664"),sQuery(id+"F0.wireOp",EDGE,"E665"),sQuery(id+"F0.wireOp",EDGE,"E666"),sQuery(id+"F0.wireOp",EDGE,"E667"),sQuery(id+"F0.wireOp",EDGE,"E668"),sQuery(id+"F0.wireOp",EDGE,"E669"),sQuery(id+"F0.wireOp",EDGE,"E670"),sQuery(id+"F0.wireOp",EDGE,"E671"),sQuery(id+"F0.wireOp",EDGE,"E672"),sQuery(id+"F0.wireOp",EDGE,"E673"),sQuery(id+"F0.wireOp",EDGE,"E674"),sQuery(id+"F0.wireOp",EDGE,"E675"),sQuery(id+"F0.wireOp",EDGE,"E676"),sQuery(id+"F0.wireOp",EDGE,"E677"),sQuery(id+"F0.wireOp",EDGE,"E678"),sQuery(id+"F0.wireOp",EDGE,"E679"),sQuery(id+"F0.wireOp",EDGE,"E680"),sQuery(id+"F0.wireOp",EDGE,"E681"),sQuery(id+"F0.wireOp",EDGE,"E682"),sQuery(id+"F0.wireOp",EDGE,"E683"),sQuery(id+"F0.wireOp",EDGE,"E684"),sQuery(id+"F0.wireOp",EDGE,"E685"),sQuery(id+"F0.wireOp",EDGE,"E686"),sQuery(id+"F0.wireOp",EDGE,"E687"),sQuery(id+"F0.wireOp",EDGE,"E688"),sQuery(id+"F0.wireOp",EDGE,"E689"),sQuery(id+"F0.wireOp",EDGE,"E690"),sQuery(id+"F0.wireOp",EDGE,"E691"),sQuery(id+"F0.wireOp",EDGE,"E692"),sQuery(id+"F0.wireOp",EDGE,"E693"),sQuery(id+"F0.wireOp",EDGE,"E694"),sQuery(id+"F0.wireOp",EDGE,"E695"),sQuery(id+"F0.wireOp",EDGE,"E696"),sQuery(id+"F0.wireOp",EDGE,"E697"),sQuery(id+"F0.wireOp",EDGE,"E698"),sQuery(id+"F0.wireOp",EDGE,"E699"),sQuery(id+"F0.wireOp",EDGE,"E700"),sQuery(id+"F0.wireOp",EDGE,"E701"),sQuery(id+"F0.wireOp",EDGE,"E702"),sQuery(id+"F0.wireOp",EDGE,"E703"),sQuery(id+"F0.wireOp",EDGE,"E704"),sQuery(id+"F0.wireOp",EDGE,"E705"),sQuery(id+"F0.wireOp",EDGE,"E706"),sQuery(id+"F0.wireOp",EDGE,"E707"),sQuery(id+"F0.wireOp",EDGE,"E708"),sQuery(id+"F0.wireOp",EDGE,"E709"),sQuery(id+"F0.wireOp",EDGE,"E710"),sQuery(id+"F0.wireOp",EDGE,"E711"),sQuery(id+"F0.wireOp",EDGE,"E712"),sQuery(id+"F0.wireOp",EDGE,"E713"),sQuery(id+"F0.wireOp",EDGE,"E714"),sQuery(id+"F0.wireOp",EDGE,"E715"),sQuery(id+"F0.wireOp",EDGE,"E716"),sQuery(id+"F0.wireOp",EDGE,"E717"),sQuery(id+"F0.wireOp",EDGE,"E718"),sQuery(id+"F0.wireOp",EDGE,"E719"),sQuery(id+"F0.wireOp",EDGE,"E720"),sQuery(id+"F0.wireOp",EDGE,"E721"),sQuery(id+"F0.wireOp",EDGE,"E722"),sQuery(id+"F0.wireOp",EDGE,"E723"),sQuery(id+"F0.wireOp",EDGE,"E724"),sQuery(id+"F0.wireOp",EDGE,"E725"),sQuery(id+"F0.wireOp",EDGE,"E726"),sQuery(id+"F0.wireOp",EDGE,"E727"),sQuery(id+"F0.wireOp",EDGE,"E728"),sQuery(id+"F0.wireOp",EDGE,"E729"),sQuery(id+"F0.wireOp",EDGE,"E730"),sQuery(id+"F0.wireOp",EDGE,"E731"),sQuery(id+"F0.wireOp",EDGE,"E732"),sQuery(id+"F0.wireOp",EDGE,"E733"),sQuery(id+"F0.wireOp",EDGE,"E734"),sQuery(id+"F0.wireOp",EDGE,"E735"),sQuery(id+"F0.wireOp",EDGE,"E736"),sQuery(id+"F0.wireOp",EDGE,"E737"),sQuery(id+"F0.wireOp",EDGE,"E738"),sQuery(id+"F0.wireOp",EDGE,"E739"),sQuery(id+"F0.wireOp",EDGE,"E740"),sQuery(id+"F0.wireOp",EDGE,"E741"),sQuery(id+"F0.wireOp",EDGE,"E742"),sQuery(id+"F0.wireOp",EDGE,"E743"),sQuery(id+"F0.wireOp",EDGE,"E744"),sQuery(id+"F0.wireOp",EDGE,"E745"),sQuery(id+"F0.wireOp",EDGE,"E746"),sQuery(id+"F0.wireOp",EDGE,"E747"),sQuery(id+"F0.wireOp",EDGE,"E748"),sQuery(id+"F0.wireOp",EDGE,"E749"),sQuery(id+"F0.wireOp",EDGE,"E750"),sQuery(id+"F0.wireOp",EDGE,"E751"),sQuery(id+"F0.wireOp",EDGE,"E752"),sQuery(id+"F0.wireOp",EDGE,"E753"),sQuery(id+"F0.wireOp",EDGE,"E754"),sQuery(id+"F0.wireOp",EDGE,"E755"),sQuery(id+"F0.wireOp",EDGE,"E756"),sQuery(id+"F0.wireOp",EDGE,"E757"),sQuery(id+"F0.wireOp",EDGE,"E758"),sQuery(id+"F0.wireOp",EDGE,"E759"),sQuery(id+"F0.wireOp",EDGE,"E760"),sQuery(id+"F0.wireOp",EDGE,"E761"),sQuery(id+"F0.wireOp",EDGE,"E762"),sQuery(id+"F0.wireOp",EDGE,"E763"),sQuery(id+"F0.wireOp",EDGE,"E764"),sQuery(id+"F0.wireOp",EDGE,"E765"),sQuery(id+"F0.wireOp",EDGE,"E766"),sQuery(id+"F0.wireOp",EDGE,"E767"),sQuery(id+"F0.wireOp",EDGE,"E768"),sQuery(id+"F0.wireOp",EDGE,"E769"),sQuery(id+"F0.wireOp",EDGE,"E770"),sQuery(id+"F0.wireOp",EDGE,"E771"),sQuery(id+"F0.wireOp",EDGE,"E772"),sQuery(id+"F0.wireOp",EDGE,"E773"),sQuery(id+"F0.wireOp",EDGE,"E774"),sQuery(id+"F0.wireOp",EDGE,"E775"),sQuery(id+"F0.wireOp",EDGE,"E776"),sQuery(id+"F0.wireOp",EDGE,"E777"),sQuery(id+"F0.wireOp",EDGE,"E778"),sQuery(id+"F0.wireOp",EDGE,"E779"),sQuery(id+"F0.wireOp",EDGE,"E780"),sQuery(id+"F0.wireOp",EDGE,"E781"),sQuery(id+"F0.wireOp",EDGE,"E782"),sQuery(id+"F0.wireOp",EDGE,"E783"),sQuery(id+"F0.wireOp",EDGE,"E784"),sQuery(id+"F0.wireOp",EDGE,"E785"),sQuery(id+"F0.wireOp",EDGE,"E786"),sQuery(id+"F0.wireOp",EDGE,"E787"),sQuery(id+"F0.wireOp",EDGE,"E788"),sQuery(id+"F0.wireOp",EDGE,"E789"),sQuery(id+"F0.wireOp",EDGE,"E790"),sQuery(id+"F0.wireOp",EDGE,"E791"),sQuery(id+"F0.wireOp",EDGE,"E792"),sQuery(id+"F0.wireOp",EDGE,"E793"),sQuery(id+"F0.wireOp",EDGE,"E794"),sQuery(id+"F0.wireOp",EDGE,"E795"),sQuery(id+"F0.wireOp",EDGE,"E796"),sQuery(id+"F0.wireOp",EDGE,"E797"),sQuery(id+"F0.wireOp",EDGE,"E798"),sQuery(id+"F0.wireOp",EDGE,"E799"),sQuery(id+"F0.wireOp",EDGE,"E800"),sQuery(id+"F0.wireOp",EDGE,"E801"),sQuery(id+"F0.wireOp",EDGE,"E802"),sQuery(id+"F0.wireOp",EDGE,"E803"),sQuery(id+"F0.wireOp",EDGE,"E804"),sQuery(id+"F0.wireOp",EDGE,"E805"),sQuery(id+"F0.wireOp",EDGE,"E806"),sQuery(id+"F0.wireOp",EDGE,"E807"),sQuery(id+"F0.wireOp",EDGE,"E808"),sQuery(id+"F0.wireOp",EDGE,"E809"),sQuery(id+"F0.wireOp",EDGE,"E810"),sQuery(id+"F0.wireOp",EDGE,"E811"),sQuery(id+"F0.wireOp",EDGE,"E812"),sQuery(id+"F0.wireOp",EDGE,"E813"),sQuery(id+"F0.wireOp",EDGE,"E814"),sQuery(id+"F0.wireOp",EDGE,"E815"),sQuery(id+"F0.wireOp",EDGE,"E816"),sQuery(id+"F0.wireOp",EDGE,"E817"),sQuery(id+"F0.wireOp",EDGE,"E818"),sQuery(id+"F0.wireOp",EDGE,"E819"),sQuery(id+"F0.wireOp",EDGE,"E820"),sQuery(id+"F0.wireOp",EDGE,"E821"),sQuery(id+"F0.wireOp",EDGE,"E822"),sQuery(id+"F0.wireOp",EDGE,"E823"),sQuery(id+"F0.wireOp",EDGE,"E824"),sQuery(id+"F0.wireOp",EDGE,"E825"),sQuery(id+"F0.wireOp",EDGE,"E826"),sQuery(id+"F0.wireOp",EDGE,"E827"),sQuery(id+"F0.wireOp",EDGE,"E828"),sQuery(id+"F0.wireOp",EDGE,"E829"),sQuery(id+"F0.wireOp",EDGE,"E830"),sQuery(id+"F0.wireOp",EDGE,"E831"),sQuery(id+"F0.wireOp",EDGE,"E832"),sQuery(id+"F0.wireOp",EDGE,"E833"),sQuery(id+"F0.wireOp",EDGE,"E834"),sQuery(id+"F0.wireOp",EDGE,"E835"),sQuery(id+"F0.wireOp",EDGE,"E836"),sQuery(id+"F0.wireOp",EDGE,"E837"),sQuery(id+"F0.wireOp",EDGE,"E838"),sQuery(id+"F0.wireOp",EDGE,"E839"),sQuery(id+"F0.wireOp",EDGE,"E840"),sQuery(id+"F0.wireOp",EDGE,"E841"),sQuery(id+"F0.wireOp",EDGE,"E842"),sQuery(id+"F0.wireOp",EDGE,"E843"),sQuery(id+"F0.wireOp",EDGE,"E844"),sQuery(id+"F0.wireOp",EDGE,"E845"),sQuery(id+"F0.wireOp",EDGE,"E846"),sQuery(id+"F0.wireOp",EDGE,"E847"),sQuery(id+"F0.wireOp",EDGE,"E848"),sQuery(id+"F0.wireOp",EDGE,"E849"),sQuery(id+"F0.wireOp",EDGE,"E850"),sQuery(id+"F0.wireOp",EDGE,"E851"),sQuery(id+"F0.wireOp",EDGE,"E852"),sQuery(id+"F0.wireOp",EDGE,"E853"),sQuery(id+"F0.wireOp",EDGE,"E854"),sQuery(id+"F0.wireOp",EDGE,"E855"),sQuery(id+"F0.wireOp",EDGE,"E856"),sQuery(id+"F0.wireOp",EDGE,"E857"),sQuery(id+"F0.wireOp",EDGE,"E858"),sQuery(id+"F0.wireOp",EDGE,"E859"),sQuery(id+"F0.wireOp",EDGE,"E860"),sQuery(id+"F0.wireOp",EDGE,"E861"),sQuery(id+"F0.wireOp",EDGE,"E862"),sQuery(id+"F0.wireOp",EDGE,"E863"),sQuery(id+"F0.wireOp",EDGE,"E864"),sQuery(id+"F0.wireOp",EDGE,"E865"),sQuery(id+"F0.wireOp",EDGE,"E866"),sQuery(id+"F0.wireOp",EDGE,"E867"),sQuery(id+"F0.wireOp",EDGE,"E868"),sQuery(id+"F0.wireOp",EDGE,"E869"),sQuery(id+"F0.wireOp",EDGE,"E870"),sQuery(id+"F0.wireOp",EDGE,"E871"),sQuery(id+"F0.wireOp",EDGE,"E872"),sQuery(id+"F0.wireOp",EDGE,"E873"),sQuery(id+"F0.wireOp",EDGE,"E874"),sQuery(id+"F0.wireOp",EDGE,"E875"),sQuery(id+"F0.wireOp",EDGE,"E876"),sQuery(id+"F0.wireOp",EDGE,"E877"),sQuery(id+"F0.wireOp",EDGE,"E878"),sQuery(id+"F0.wireOp",EDGE,"E879"),sQuery(id+"F0.wireOp",EDGE,"E880"),sQuery(id+"F0.wireOp",EDGE,"E881"),sQuery(id+"F0.wireOp",EDGE,"E882"),sQuery(id+"F0.wireOp",EDGE,"E883"),sQuery(id+"F0.wireOp",EDGE,"E884"),sQuery(id+"F0.wireOp",EDGE,"E885"),sQuery(id+"F0.wireOp",EDGE,"E886"),sQuery(id+"F0.wireOp",EDGE,"E887"),sQuery(id+"F0.wireOp",EDGE,"E888"),sQuery(id+"F0.wireOp",EDGE,"E889"),sQuery(id+"F0.wireOp",EDGE,"E890"),sQuery(id+"F0.wireOp",EDGE,"E891"),sQuery(id+"F0.wireOp",EDGE,"E892"),sQuery(id+"F0.wireOp",EDGE,"E893"),sQuery(id+"F0.wireOp",EDGE,"E894"),sQuery(id+"F0.wireOp",EDGE,"E895"),sQuery(id+"F0.wireOp",EDGE,"E896"),sQuery(id+"F0.wireOp",EDGE,"E897"),sQuery(id+"F0.wireOp",EDGE,"E898"),sQuery(id+"F0.wireOp",EDGE,"E899"),sQuery(id+"F0.wireOp",EDGE,"E900"),sQuery(id+"F0.wireOp",EDGE,"E901"),sQuery(id+"F0.wireOp",EDGE,"E902"),sQuery(id+"F0.wireOp",EDGE,"E903"),sQuery(id+"F0.wireOp",EDGE,"E904"),sQuery(id+"F0.wireOp",EDGE,"E905"),sQuery(id+"F0.wireOp",EDGE,"E906"),sQuery(id+"F0.wireOp",EDGE,"E907"),sQuery(id+"F0.wireOp",EDGE,"E908"),sQuery(id+"F0.wireOp",EDGE,"E909"),sQuery(id+"F0.wireOp",EDGE,"E910"),sQuery(id+"F0.wireOp",EDGE,"E911"),sQuery(id+"F0.wireOp",EDGE,"E912"),sQuery(id+"F0.wireOp",EDGE,"E913"),sQuery(id+"F0.wireOp",EDGE,"E914"),sQuery(id+"F0.wireOp",EDGE,"E915"),sQuery(id+"F0.wireOp",EDGE,"E916"),sQuery(id+"F0.wireOp",EDGE,"E917"),sQuery(id+"F0.wireOp",EDGE,"E918"),sQuery(id+"F0.wireOp",EDGE,"E919"),sQuery(id+"F0.wireOp",EDGE,"E920"),sQuery(id+"F0.wireOp",EDGE,"E921"),sQuery(id+"F0.wireOp",EDGE,"E922"),sQuery(id+"F0.wireOp",EDGE,"E923"),sQuery(id+"F0.wireOp",EDGE,"E924"),sQuery(id+"F0.wireOp",EDGE,"E925"),sQuery(id+"F0.wireOp",EDGE,"E926"),sQuery(id+"F0.wireOp",EDGE,"E927"),sQuery(id+"F0.wireOp",EDGE,"E928"),sQuery(id+"F0.wireOp",EDGE,"E929"),sQuery(id+"F0.wireOp",EDGE,"E930"),sQuery(id+"F0.wireOp",EDGE,"E931"),sQuery(id+"F0.wireOp",EDGE,"E932"),sQuery(id+"F0.wireOp",EDGE,"E933"),sQuery(id+"F0.wireOp",EDGE,"E934"),sQuery(id+"F0.wireOp",EDGE,"E935"),sQuery(id+"F0.wireOp",EDGE,"E936"),sQuery(id+"F0.wireOp",EDGE,"E937"),sQuery(id+"F0.wireOp",EDGE,"E938"),sQuery(id+"F0.wireOp",EDGE,"E939"),sQuery(id+"F0.wireOp",EDGE,"E940"),sQuery(id+"F0.wireOp",EDGE,"E941"),sQuery(id+"F0.wireOp",EDGE,"E942"),sQuery(id+"F0.wireOp",EDGE,"E943"),sQuery(id+"F0.wireOp",EDGE,"E944"),sQuery(id+"F0.wireOp",EDGE,"E945"),sQuery(id+"F0.wireOp",EDGE,"E946"),sQuery(id+"F0.wireOp",EDGE,"E947"),sQuery(id+"F0.wireOp",EDGE,"E948"),sQuery(id+"F0.wireOp",EDGE,"E949"),sQuery(id+"F0.wireOp",EDGE,"E950"),sQuery(id+"F0.wireOp",EDGE,"E951"),sQuery(id+"F0.wireOp",EDGE,"E952"),sQuery(id+"F0.wireOp",EDGE,"E953"),sQuery(id+"F0.wireOp",EDGE,"E954"),sQuery(id+"F0.wireOp",EDGE,"E955"),sQuery(id+"F0.wireOp",EDGE,"E956"),sQuery(id+"F0.wireOp",EDGE,"E957"),sQuery(id+"F0.wireOp",EDGE,"E958"),sQuery(id+"F0.wireOp",EDGE,"E959"),sQuery(id+"F0.wireOp",EDGE,"E960"),sQuery(id+"F0.wireOp",EDGE,"E961"),sQuery(id+"F0.wireOp",EDGE,"E962"),sQuery(id+"F0.wireOp",EDGE,"E963"),sQuery(id+"F0.wireOp",EDGE,"E964"),sQuery(id+"F0.wireOp",EDGE,"E965"),sQuery(id+"F0.wireOp",EDGE,"E966"),sQuery(id+"F0.wireOp",EDGE,"E967"),sQuery(id+"F0.wireOp",EDGE,"E968"),sQuery(id+"F0.wireOp",EDGE,"E969"),sQuery(id+"F0.wireOp",EDGE,"E970"),sQuery(id+"F0.wireOp",EDGE,"E971"),sQuery(id+"F0.wireOp",EDGE,"E972"),sQuery(id+"F0.wireOp",EDGE,"E973"),sQuery(id+"F0.wireOp",EDGE,"E974"),sQuery(id+"F0.wireOp",EDGE,"E975"),sQuery(id+"F0.wireOp",EDGE,"E976"),sQuery(id+"F0.wireOp",EDGE,"E977"),sQuery(id+"F0.wireOp",EDGE,"E978"),sQuery(id+"F0.wireOp",EDGE,"E979"),sQuery(id+"F0.wireOp",EDGE,"E980"),sQuery(id+"F0.wireOp",EDGE,"E981"),sQuery(id+"F0.wireOp",EDGE,"E982"),sQuery(id+"F0.wireOp",EDGE,"E983"),sQuery(id+"F0.wireOp",EDGE,"E984"),sQuery(id+"F0.wireOp",EDGE,"E985"),sQuery(id+"F0.wireOp",EDGE,"E986"),sQuery(id+"F0.wireOp",EDGE,"E987"),sQuery(id+"F0.wireOp",EDGE,"E988"),sQuery(id+"F0.wireOp",EDGE,"E989"),sQuery(id+"F0.wireOp",EDGE,"E990"),sQuery(id+"F0.wireOp",EDGE,"E991"),sQuery(id+"F0.wireOp",EDGE,"E992"),sQuery(id+"F0.wireOp",EDGE,"E993"),sQuery(id+"F0.wireOp",EDGE,"E994"),sQuery(id+"F0.wireOp",EDGE,"E995"),sQuery(id+"F0.wireOp",EDGE,"E996"),sQuery(id+"F0.wireOp",EDGE,"E997"),sQuery(id+"F0.wireOp",EDGE,"E998"),sQuery(id+"F0.wireOp",EDGE,"E999"),sQuery(id+"F0.wireOp",EDGE,"E1000"),sQuery(id+"F0.wireOp",EDGE,"E1001"),sQuery(id+"F0.wireOp",EDGE,"E1002"),sQuery(id+"F0.wireOp",EDGE,"E1003"),sQuery(id+"F0.wireOp",EDGE,"E1004"),sQuery(id+"F0.wireOp",EDGE,"E1005"),sQuery(id+"F0.wireOp",EDGE,"E1006"),sQuery(id+"F0.wireOp",EDGE,"E1007"),sQuery(id+"F0.wireOp",EDGE,"E1008"),sQuery(id+"F0.wireOp",EDGE,"E1009"),sQuery(id+"F0.wireOp",EDGE,"E1010"),sQuery(id+"F0.wireOp",EDGE,"E1011"),sQuery(id+"F0.wireOp",EDGE,"E1012"),sQuery(id+"F0.wireOp",EDGE,"E1013"),sQuery(id+"F0.wireOp",EDGE,"E1014"),sQuery(id+"F0.wireOp",EDGE,"E1015"),sQuery(id+"F0.wireOp",EDGE,"E1016"),sQuery(id+"F0.wireOp",EDGE,"E1017"),sQuery(id+"F0.wireOp",EDGE,"E1018"),sQuery(id+"F0.wireOp",EDGE,"E1019"),sQuery(id+"F0.wireOp",EDGE,"E1020"),sQuery(id+"F0.wireOp",EDGE,"E1021"),sQuery(id+"F0.wireOp",EDGE,"E1022"),sQuery(id+"F0.wireOp",EDGE,"E1023"),sQuery(id+"F0.wireOp",EDGE,"E1024"),sQuery(id+"F0.wireOp",EDGE,"E1025"),sQuery(id+"F0.wireOp",EDGE,"E1026"),sQuery(id+"F0.wireOp",EDGE,"E1027"),sQuery(id+"F0.wireOp",EDGE,"E1028"),sQuery(id+"F0.wireOp",EDGE,"E1029"),sQuery(id+"F0.wireOp",EDGE,"E1030"),sQuery(id+"F0.wireOp",EDGE,"E1031"),sQuery(id+"F0.wireOp",EDGE,"E1032"),sQuery(id+"F0.wireOp",EDGE,"E1033"),sQuery(id+"F0.wireOp",EDGE,"E1034"),sQuery(id+"F0.wireOp",EDGE,"E1035"),sQuery(id+"F0.wireOp",EDGE,"E1036"),sQuery(id+"F0.wireOp",EDGE,"E1037"),sQuery(id+"F0.wireOp",EDGE,"E1038"),sQuery(id+"F0.wireOp",EDGE,"E1039"),sQuery(id+"F0.wireOp",EDGE,"E1040"),sQuery(id+"F0.wireOp",EDGE,"E1041"),sQuery(id+"F0.wireOp",EDGE,"E1042"),sQuery(id+"F0.wireOp",EDGE,"E1043"),sQuery(id+"F0.wireOp",EDGE,"E1044"),sQuery(id+"F0.wireOp",EDGE,"E1045"),sQuery(id+"F0.wireOp",EDGE,"E1046"),sQuery(id+"F0.wireOp",EDGE,"E1047"),sQuery(id+"F0.wireOp",EDGE,"E1048"),sQuery(id+"F0.wireOp",EDGE,"E1049"),sQuery(id+"F0.wireOp",EDGE,"E1050"),sQuery(id+"F0.wireOp",EDGE,"E1051"),sQuery(id+"F0.wireOp",EDGE,"E1052"),sQuery(id+"F0.wireOp",EDGE,"E1053"),sQuery(id+"F0.wireOp",EDGE,"E1054"),sQuery(id+"F0.wireOp",EDGE,"E1055"),sQuery(id+"F0.wireOp",EDGE,"E1056"),sQuery(id+"F0.wireOp",EDGE,"E1057"),sQuery(id+"F0.wireOp",EDGE,"E1058"),sQuery(id+"F0.wireOp",EDGE,"E1059"),sQuery(id+"F0.wireOp",EDGE,"E1060"),sQuery(id+"F0.wireOp",EDGE,"E1061"),sQuery(id+"F0.wireOp",EDGE,"E1062"),sQuery(id+"F0.wireOp",EDGE,"E1063"),sQuery(id+"F0.wireOp",EDGE,"E1064"),sQuery(id+"F0.wireOp",EDGE,"E1065"),sQuery(id+"F0.wireOp",EDGE,"E1066"),sQuery(id+"F0.wireOp",EDGE,"E1067"),sQuery(id+"F0.wireOp",EDGE,"E1068"),sQuery(id+"F0.wireOp",EDGE,"E1069"),sQuery(id+"F0.wireOp",EDGE,"E1070"),sQuery(id+"F0.wireOp",EDGE,"E1071"),sQuery(id+"F0.wireOp",EDGE,"E1072"),sQuery(id+"F0.wireOp",EDGE,"E1073"),sQuery(id+"F0.wireOp",EDGE,"E1074"),sQuery(id+"F0.wireOp",EDGE,"E1075"),sQuery(id+"F0.wireOp",EDGE,"E1076"),sQuery(id+"F0.wireOp",EDGE,"E1077"),sQuery(id+"F0.wireOp",EDGE,"E1078"),sQuery(id+"F0.wireOp",EDGE,"E1079"),sQuery(id+"F0.wireOp",EDGE,"E1080"),sQuery(id+"F0.wireOp",EDGE,"E1081"),sQuery(id+"F0.wireOp",EDGE,"E1082"),sQuery(id+"F0.wireOp",EDGE,"E1083"),sQuery(id+"F0.wireOp",EDGE,"E1084"),sQuery(id+"F0.wireOp",EDGE,"E1085"),sQuery(id+"F0.wireOp",EDGE,"E1086"),sQuery(id+"F0.wireOp",EDGE,"E1087"),sQuery(id+"F0.wireOp",EDGE,"E1088"),sQuery(id+"F0.wireOp",EDGE,"E1089"),sQuery(id+"F0.wireOp",EDGE,"E1090"),sQuery(id+"F0.wireOp",EDGE,"E1091"),sQuery(id+"F0.wireOp",EDGE,"E1092"),sQuery(id+"F0.wireOp",EDGE,"E1093"),sQuery(id+"F0.wireOp",EDGE,"E1094"),sQuery(id+"F0.wireOp",EDGE,"E1095"),sQuery(id+"F0.wireOp",EDGE,"E1096"),sQuery(id+"F0.wireOp",EDGE,"E1097"),sQuery(id+"F0.wireOp",EDGE,"E1098"),sQuery(id+"F0.wireOp",EDGE,"E1099"),sQuery(id+"F0.wireOp",EDGE,"E1100"),sQuery(id+"F0.wireOp",EDGE,"E1101"),sQuery(id+"F0.wireOp",EDGE,"E1102"),sQuery(id+"F0.wireOp",EDGE,"E1103"),sQuery(id+"F0.wireOp",EDGE,"E1104"),sQuery(id+"F0.wireOp",EDGE,"E1105"),sQuery(id+"F0.wireOp",EDGE,"E1106"),sQuery(id+"F0.wireOp",EDGE,"E1107"),sQuery(id+"F0.wireOp",EDGE,"E1108"),sQuery(id+"F0.wireOp",EDGE,"E1109"),sQuery(id+"F0.wireOp",EDGE,"E1110"),sQuery(id+"F0.wireOp",EDGE,"E1111"),sQuery(id+"F0.wireOp",EDGE,"E1112"),sQuery(id+"F0.wireOp",EDGE,"E1113"),sQuery(id+"F0.wireOp",EDGE,"E1114"),sQuery(id+"F0.wireOp",EDGE,"E1115"),sQuery(id+"F0.wireOp",EDGE,"E1116"),sQuery(id+"F0.wireOp",EDGE,"E1117"),sQuery(id+"F0.wireOp",EDGE,"E1118"),sQuery(id+"F0.wireOp",EDGE,"E1119"),sQuery(id+"F0.wireOp",EDGE,"E1120"),sQuery(id+"F0.wireOp",EDGE,"E1121"),sQuery(id+"F0.wireOp",EDGE,"E1122"),sQuery(id+"F0.wireOp",EDGE,"E1123"),sQuery(id+"F0.wireOp",EDGE,"E1124"),sQuery(id+"F0.wireOp",EDGE,"E1125"),sQuery(id+"F0.wireOp",EDGE,"E1126"),sQuery(id+"F0.wireOp",EDGE,"E1127"),sQuery(id+"F0.wireOp",EDGE,"E1128"),sQuery(id+"F0.wireOp",EDGE,"E1129"),sQuery(id+"F0.wireOp",EDGE,"E1130"),sQuery(id+"F0.wireOp",EDGE,"E1131"),sQuery(id+"F0.wireOp",EDGE,"E1132"),sQuery(id+"F0.wireOp",EDGE,"E1133"),sQuery(id+"F0.wireOp",EDGE,"E1134"),sQuery(id+"F0.wireOp",EDGE,"E1135"),sQuery(id+"F0.wireOp",EDGE,"E1136"),sQuery(id+"F0.wireOp",EDGE,"E1137"),sQuery(id+"F0.wireOp",EDGE,"E1138"),sQuery(id+"F0.wireOp",EDGE,"E1139"),sQuery(id+"F0.wireOp",EDGE,"E1140"),sQuery(id+"F0.wireOp",EDGE,"E1141"),sQuery(id+"F0.wireOp",EDGE,"E1142"),sQuery(id+"F0.wireOp",EDGE,"E1143"),sQuery(id+"F0.wireOp",EDGE,"E1144"),sQuery(id+"F0.wireOp",EDGE,"E1145"),sQuery(id+"F0.wireOp",EDGE,"E1146"),sQuery(id+"F0.wireOp",EDGE,"E1147"),sQuery(id+"F0.wireOp",EDGE,"E1148"),sQuery(id+"F0.wireOp",EDGE,"E1149"),sQuery(id+"F0.wireOp",EDGE,"E1150"),sQuery(id+"F0.wireOp",EDGE,"E1151"),sQuery(id+"F0.wireOp",EDGE,"E1152"),sQuery(id+"F0.wireOp",EDGE,"E1153"),sQuery(id+"F0.wireOp",EDGE,"E1154"),sQuery(id+"F0.wireOp",EDGE,"E1155"),sQuery(id+"F0.wireOp",EDGE,"E1156"),sQuery(id+"F0.wireOp",EDGE,"E1157"),sQuery(id+"F0.wireOp",EDGE,"E1158"),sQuery(id+"F0.wireOp",EDGE,"E1159"),sQuery(id+"F0.wireOp",EDGE,"E1160"),sQuery(id+"F0.wireOp",EDGE,"E1161"),sQuery(id+"F0.wireOp",EDGE,"E1162"),sQuery(id+"F0.wireOp",EDGE,"E1163"),sQuery(id+"F0.wireOp",EDGE,"E1164"),sQuery(id+"F0.wireOp",EDGE,"E1165"),sQuery(id+"F0.wireOp",EDGE,"E1166"),sQuery(id+"F0.wireOp",EDGE,"E1167"),sQuery(id+"F0.wireOp",EDGE,"E1168"),sQuery(id+"F0.wireOp",EDGE,"E1169"),sQuery(id+"F0.wireOp",EDGE,"E1170"),sQuery(id+"F0.wireOp",EDGE,"E1171"),sQuery(id+"F0.wireOp",EDGE,"E1172"),sQuery(id+"F0.wireOp",EDGE,"E1173"),sQuery(id+"F0.wireOp",EDGE,"E1174"),sQuery(id+"F0.wireOp",EDGE,"E1175"),sQuery(id+"F0.wireOp",EDGE,"E1176"),sQuery(id+"F0.wireOp",EDGE,"E1177"),sQuery(id+"F0.wireOp",EDGE,"E1178"),sQuery(id+"F0.wireOp",EDGE,"E1179"),sQuery(id+"F0.wireOp",EDGE,"E1180"),sQuery(id+"F0.wireOp",EDGE,"E1181"),sQuery(id+"F0.wireOp",EDGE,"E1182"),sQuery(id+"F0.wireOp",EDGE,"E1183"),sQuery(id+"F0.wireOp",EDGE,"E1184"),sQuery(id+"F0.wireOp",EDGE,"E1185"),sQuery(id+"F0.wireOp",EDGE,"E1186"),sQuery(id+"F0.wireOp",EDGE,"E1187"),sQuery(id+"F0.wireOp",EDGE,"E1188"),sQuery(id+"F0.wireOp",EDGE,"E1189"),sQuery(id+"F0.wireOp",EDGE,"E1190"),sQuery(id+"F0.wireOp",EDGE,"E1191"),sQuery(id+"F0.wireOp",EDGE,"E1192"),sQuery(id+"F0.wireOp",EDGE,"E1193"),sQuery(id+"F0.wireOp",EDGE,"E1194"),sQuery(id+"F0.wireOp",EDGE,"E1195"),sQuery(id+"F0.wireOp",EDGE,"E1196"),sQuery(id+"F0.wireOp",EDGE,"E1197"),sQuery(id+"F0.wireOp",EDGE,"E1198"),sQuery(id+"F0.wireOp",EDGE,"E1199"),sQuery(id+"F0.wireOp",EDGE,"E1200"),sQuery(id+"F0.wireOp",EDGE,"E1201"),sQuery(id+"F0.wireOp",EDGE,"E1202"),sQuery(id+"F0.wireOp",EDGE,"E1203"),sQuery(id+"F0.wireOp",EDGE,"E1204"),sQuery(id+"F0.wireOp",EDGE,"E1205"),sQuery(id+"F0.wireOp",EDGE,"E1206"),sQuery(id+"F0.wireOp",EDGE,"E1207"),sQuery(id+"F0.wireOp",EDGE,"E1208"),sQuery(id+"F0.wireOp",EDGE,"E1209"),sQuery(id+"F0.wireOp",EDGE,"E1210"),sQuery(id+"F0.wireOp",EDGE,"E1211"),sQuery(id+"F0.wireOp",EDGE,"E1212"),sQuery(id+"F0.wireOp",EDGE,"E1213"),sQuery(id+"F0.wireOp",EDGE,"E1214"),sQuery(id+"F0.wireOp",EDGE,"E1215"),sQuery(id+"F0.wireOp",EDGE,"E1216"),sQuery(id+"F0.wireOp",EDGE,"E1217"),sQuery(id+"F0.wireOp",EDGE,"E1218"),sQuery(id+"F0.wireOp",EDGE,"E1219"),sQuery(id+"F0.wireOp",EDGE,"E1220"),sQuery(id+"F0.wireOp",EDGE,"E1221"),sQuery(id+"F0.wireOp",EDGE,"E1222"),sQuery(id+"F0.wireOp",EDGE,"E1223"),sQuery(id+"F0.wireOp",EDGE,"E1224"),sQuery(id+"F0.wireOp",EDGE,"E1225"),sQuery(id+"F0.wireOp",EDGE,"E1226"),sQuery(id+"F0.wireOp",EDGE,"E1227"),sQuery(id+"F0.wireOp",EDGE,"E1228"),sQuery(id+"F0.wireOp",EDGE,"E1229"),sQuery(id+"F0.wireOp",EDGE,"E1230"),sQuery(id+"F0.wireOp",EDGE,"E1231"),sQuery(id+"F0.wireOp",EDGE,"E1232"),sQuery(id+"F0.wireOp",EDGE,"E1233"),sQuery(id+"F0.wireOp",EDGE,"E1234"),sQuery(id+"F0.wireOp",EDGE,"E1235"),sQuery(id+"F0.wireOp",EDGE,"E1236"),sQuery(id+"F0.wireOp",EDGE,"E1237"),sQuery(id+"F0.wireOp",EDGE,"E1238"),sQuery(id+"F0.wireOp",EDGE,"E1239"),sQuery(id+"F0.wireOp",EDGE,"E1240"),sQuery(id+"F0.wireOp",EDGE,"E1241"),sQuery(id+"F0.wireOp",EDGE,"E1242"),sQuery(id+"F0.wireOp",EDGE,"E1243"),sQuery(id+"F0.wireOp",EDGE,"E1244"),sQuery(id+"F0.wireOp",EDGE,"E1245"),sQuery(id+"F0.wireOp",EDGE,"E1246"),sQuery(id+"F0.wireOp",EDGE,"E1247"),sQuery(id+"F0.wireOp",EDGE,"E1248"),sQuery(id+"F0.wireOp",EDGE,"E1249"),sQuery(id+"F0.wireOp",EDGE,"E1250"),sQuery(id+"F0.wireOp",EDGE,"E1251"),sQuery(id+"F0.wireOp",EDGE,"E1252"),sQuery(id+"F0.wireOp",EDGE,"E1253"),sQuery(id+"F0.wireOp",EDGE,"E1254"),sQuery(id+"F0.wireOp",EDGE,"E1255"),sQuery(id+"F0.wireOp",EDGE,"E1256"),sQuery(id+"F0.wireOp",EDGE,"E1257"),sQuery(id+"F0.wireOp",EDGE,"E1258"),sQuery(id+"F0.wireOp",EDGE,"E1259"),sQuery(id+"F0.wireOp",EDGE,"E1260"),sQuery(id+"F0.wireOp",EDGE,"E1261"),sQuery(id+"F0.wireOp",EDGE,"E1262"),sQuery(id+"F0.wireOp",EDGE,"E1263"),sQuery(id+"F0.wireOp",EDGE,"E1264"),sQuery(id+"F0.wireOp",EDGE,"E1265"),sQuery(id+"F0.wireOp",EDGE,"E1266"),sQuery(id+"F0.wireOp",EDGE,"E1267"),sQuery(id+"F0.wireOp",EDGE,"E1268"),sQuery(id+"F0.wireOp",EDGE,"E1269"),sQuery(id+"F0.wireOp",EDGE,"E1270"),sQuery(id+"F0.wireOp",EDGE,"E1271"),sQuery(id+"F0.wireOp",EDGE,"E1272"),sQuery(id+"F0.wireOp",EDGE,"E1273"),sQuery(id+"F0.wireOp",EDGE,"E1274"),sQuery(id+"F0.wireOp",EDGE,"E1275"),sQuery(id+"F0.wireOp",EDGE,"E1276"),sQuery(id+"F0.wireOp",EDGE,"E1277"),sQuery(id+"F0.wireOp",EDGE,"E1278"),sQuery(id+"F0.wireOp",EDGE,"E1279"),sQuery(id+"F0.wireOp",EDGE,"E1280"),sQuery(id+"F0.wireOp",EDGE,"E1281"),sQuery(id+"F0.wireOp",EDGE,"E1282"),sQuery(id+"F0.wireOp",EDGE,"E1283"),sQuery(id+"F0.wireOp",EDGE,"E1284"),sQuery(id+"F0.wireOp",EDGE,"E1285"),sQuery(id+"F0.wireOp",EDGE,"E1286"),sQuery(id+"F0.wireOp",EDGE,"E1287"),sQuery(id+"F0.wireOp",EDGE,"E1288"),sQuery(id+"F0.wireOp",EDGE,"E1289"),sQuery(id+"F0.wireOp",EDGE,"E1290"),sQuery(id+"F0.wireOp",EDGE,"E1291"),sQuery(id+"F0.wireOp",EDGE,"E1292"),sQuery(id+"F0.wireOp",EDGE,"E1293"),sQuery(id+"F0.wireOp",EDGE,"E1294"),sQuery(id+"F0.wireOp",EDGE,"E1295"),sQuery(id+"F0.wireOp",EDGE,"E1296"),sQuery(id+"F0.wireOp",EDGE,"E1297"),sQuery(id+"F0.wireOp",EDGE,"E1298"),sQuery(id+"F0.wireOp",EDGE,"E1299"),sQuery(id+"F0.wireOp",EDGE,"E1300"),sQuery(id+"F0.wireOp",EDGE,"E1301"),sQuery(id+"F0.wireOp",EDGE,"E1302"),sQuery(id+"F0.wireOp",EDGE,"E1303"),sQuery(id+"F0.wireOp",EDGE,"E1304"),sQuery(id+"F0.wireOp",EDGE,"E1305"),sQuery(id+"F0.wireOp",EDGE,"E1306"),sQuery(id+"F0.wireOp",EDGE,"E1307"),sQuery(id+"F0.wireOp",EDGE,"E1308"),sQuery(id+"F0.wireOp",EDGE,"E1309"),sQuery(id+"F0.wireOp",EDGE,"E1310"),sQuery(id+"F0.wireOp",EDGE,"E1311"),sQuery(id+"F0.wireOp",EDGE,"E1312"),sQuery(id+"F0.wireOp",EDGE,"E1313"),sQuery(id+"F0.wireOp",EDGE,"E1314"),sQuery(id+"F0.wireOp",EDGE,"E1315"),sQuery(id+"F0.wireOp",EDGE,"E1316"),sQuery(id+"F0.wireOp",EDGE,"E1317"),sQuery(id+"F0.wireOp",EDGE,"E1318"),sQuery(id+"F0.wireOp",EDGE,"E1319"),sQuery(id+"F0.wireOp",EDGE,"E1320"),sQuery(id+"F0.wireOp",EDGE,"E1321"),sQuery(id+"F0.wireOp",EDGE,"E1322"),sQuery(id+"F0.wireOp",EDGE,"E1323"),sQuery(id+"F0.wireOp",EDGE,"E1324"),sQuery(id+"F0.wireOp",EDGE,"E1325"),sQuery(id+"F0.wireOp",EDGE,"E1326"),sQuery(id+"F0.wireOp",EDGE,"E1327"),sQuery(id+"F0.wireOp",EDGE,"E1328"),sQuery(id+"F0.wireOp",EDGE,"E1329"),sQuery(id+"F0.wireOp",EDGE,"E1330"),sQuery(id+"F0.wireOp",EDGE,"E1331"),sQuery(id+"F0.wireOp",EDGE,"E1332"),sQuery(id+"F0.wireOp",EDGE,"E1333"),sQuery(id+"F0.wireOp",EDGE,"E1334"),sQuery(id+"F0.wireOp",EDGE,"E1335"),sQuery(id+"F0.wireOp",EDGE,"E1336"),sQuery(id+"F0.wireOp",EDGE,"E1337"),sQuery(id+"F0.wireOp",EDGE,"E1338"),sQuery(id+"F0.wireOp",EDGE,"E1339"),sQuery(id+"F0.wireOp",EDGE,"E1340"),sQuery(id+"F0.wireOp",EDGE,"E1341"),sQuery(id+"F0.wireOp",EDGE,"E1342"),sQuery(id+"F0.wireOp",EDGE,"E1343"),sQuery(id+"F0.wireOp",EDGE,"E1344"),sQuery(id+"F0.wireOp",EDGE,"E1345"),sQuery(id+"F0.wireOp",EDGE,"E1346"),sQuery(id+"F0.wireOp",EDGE,"E1347"),sQuery(id+"F0.wireOp",EDGE,"E1348"),sQuery(id+"F0.wireOp",EDGE,"E1349"),sQuery(id+"F0.wireOp",EDGE,"E1350"),sQuery(id+"F0.wireOp",EDGE,"E1351"),sQuery(id+"F0.wireOp",EDGE,"E1352"),sQuery(id+"F0.wireOp",EDGE,"E1353"),sQuery(id+"F0.wireOp",EDGE,"E1354"),sQuery(id+"F0.wireOp",EDGE,"E1355"),sQuery(id+"F0.wireOp",EDGE,"E1356"),sQuery(id+"F0.wireOp",EDGE,"E1357"),sQuery(id+"F0.wireOp",EDGE,"E1358"),sQuery(id+"F0.wireOp",EDGE,"E1359"),sQuery(id+"F0.wireOp",EDGE,"E1360"),sQuery(id+"F0.wireOp",EDGE,"E1361"),sQuery(id+"F0.wireOp",EDGE,"E1362"),sQuery(id+"F0.wireOp",EDGE,"E1363"),sQuery(id+"F0.wireOp",EDGE,"E1364"),sQuery(id+"F0.wireOp",EDGE,"E1365"),sQuery(id+"F0.wireOp",EDGE,"E1366"),sQuery(id+"F0.wireOp",EDGE,"E1367"),sQuery(id+"F0.wireOp",EDGE,"E1368"),sQuery(id+"F0.wireOp",EDGE,"E1369"),sQuery(id+"F0.wireOp",EDGE,"E1370"),sQuery(id+"F0.wireOp",EDGE,"E1371"),sQuery(id+"F0.wireOp",EDGE,"E1372"),sQuery(id+"F0.wireOp",EDGE,"E1373"),sQuery(id+"F0.wireOp",EDGE,"E1374"),sQuery(id+"F0.wireOp",EDGE,"E1375"),sQuery(id+"F0.wireOp",EDGE,"E1376"),sQuery(id+"F0.wireOp",EDGE,"E1377"),sQuery(id+"F0.wireOp",EDGE,"E1378"),sQuery(id+"F0.wireOp",EDGE,"E1379"),sQuery(id+"F0.wireOp",EDGE,"E1380"),sQuery(id+"F0.wireOp",EDGE,"E1381"),sQuery(id+"F0.wireOp",EDGE,"E1382"),sQuery(id+"F0.wireOp",EDGE,"E1383"),sQuery(id+"F0.wireOp",EDGE,"E1384"),sQuery(id+"F0.wireOp",EDGE,"E1385"),sQuery(id+"F0.wireOp",EDGE,"E1386"),sQuery(id+"F0.wireOp",EDGE,"E1387"),sQuery(id+"F0.wireOp",EDGE,"E1388"),sQuery(id+"F0.wireOp",EDGE,"E1389"),sQuery(id+"F0.wireOp",EDGE,"E1390"),sQuery(id+"F0.wireOp",EDGE,"E1391"),sQuery(id+"F0.wireOp",EDGE,"E1392"),sQuery(id+"F0.wireOp",EDGE,"E1393"),sQuery(id+"F0.wireOp",EDGE,"E1394"),sQuery(id+"F0.wireOp",EDGE,"E1395"),sQuery(id+"F0.wireOp",EDGE,"E1396"),sQuery(id+"F0.wireOp",EDGE,"E1397"),sQuery(id+"F0.wireOp",EDGE,"E1398"),sQuery(id+"F0.wireOp",EDGE,"E1399"),sQuery(id+"F0.wireOp",EDGE,"E1400"),sQuery(id+"F0.wireOp",EDGE,"E1401"),sQuery(id+"F0.wireOp",EDGE,"E1402"),sQuery(id+"F0.wireOp",EDGE,"E1403"),sQuery(id+"F0.wireOp",EDGE,"E1404"),sQuery(id+"F0.wireOp",EDGE,"E1405"),sQuery(id+"F0.wireOp",EDGE,"E1406"),sQuery(id+"F0.wireOp",EDGE,"E1407"),sQuery(id+"F0.wireOp",EDGE,"E1408"),sQuery(id+"F0.wireOp",EDGE,"E1409"),sQuery(id+"F0.wireOp",EDGE,"E1410"),sQuery(id+"F0.wireOp",EDGE,"E1411"),sQuery(id+"F0.wireOp",EDGE,"E1412"),sQuery(id+"F0.wireOp",EDGE,"E1413"),sQuery(id+"F0.wireOp",EDGE,"E1414"),sQuery(id+"F0.wireOp",EDGE,"E1415"),sQuery(id+"F0.wireOp",EDGE,"E1416"),sQuery(id+"F0.wireOp",EDGE,"E1417"),sQuery(id+"F0.wireOp",EDGE,"E1418"),sQuery(id+"F0.wireOp",EDGE,"E1419"),sQuery(id+"F0.wireOp",EDGE,"E1420"),sQuery(id+"F0.wireOp",EDGE,"E1421"),sQuery(id+"F0.wireOp",EDGE,"E1422"),sQuery(id+"F0.wireOp",EDGE,"E1423"),sQuery(id+"F0.wireOp",EDGE,"E1424"),sQuery(id+"F0.wireOp",EDGE,"E1425"),sQuery(id+"F0.wireOp",EDGE,"E1426"),sQuery(id+"F0.wireOp",EDGE,"E1427"),sQuery(id+"F0.wireOp",EDGE,"E1428"),sQuery(id+"F0.wireOp",EDGE,"E1429"),sQuery(id+"F0.wireOp",EDGE,"E1430"),sQuery(id+"F0.wireOp",EDGE,"E1431"),sQuery(id+"F0.wireOp",EDGE,"E1432"),sQuery(id+"F0.wireOp",EDGE,"E1433"),sQuery(id+"F0.wireOp",EDGE,"E1434"),sQuery(id+"F0.wireOp",EDGE,"E1435"),sQuery(id+"F0.wireOp",EDGE,"E1436"),sQuery(id+"F0.wireOp",EDGE,"E1437"),sQuery(id+"F0.wireOp",EDGE,"E1438"),sQuery(id+"F0.wireOp",EDGE,"E1439"),sQuery(id+"F0.wireOp",EDGE,"E1440"),sQuery(id+"F0.wireOp",EDGE,"E1441"),sQuery(id+"F0.wireOp",EDGE,"E1442"),sQuery(id+"F0.wireOp",EDGE,"E1443"),sQuery(id+"F0.wireOp",EDGE,"E1444"),sQuery(id+"F0.wireOp",EDGE,"E1445"),sQuery(id+"F0.wireOp",EDGE,"E1446"),sQuery(id+"F0.wireOp",EDGE,"E1447"),sQuery(id+"F0.wireOp",EDGE,"E1448"),sQuery(id+"F0.wireOp",EDGE,"E1449"),sQuery(id+"F0.wireOp",EDGE,"E1450"),sQuery(id+"F0.wireOp",EDGE,"E1451"),sQuery(id+"F0.wireOp",EDGE,"E1452"),sQuery(id+"F0.wireOp",EDGE,"E1453"),sQuery(id+"F0.wireOp",EDGE,"E1454"),sQuery(id+"F0.wireOp",EDGE,"E1455"),sQuery(id+"F0.wireOp",EDGE,"E1456"),sQuery(id+"F0.wireOp",EDGE,"E1457"),sQuery(id+"F0.wireOp",EDGE,"E1458"),sQuery(id+"F0.wireOp",EDGE,"E1459"),sQuery(id+"F0.wireOp",EDGE,"E1460"),sQuery(id+"F0.wireOp",EDGE,"E1461"),sQuery(id+"F0.wireOp",EDGE,"E1462"),sQuery(id+"F0.wireOp",EDGE,"E1463"),sQuery(id+"F0.wireOp",EDGE,"E1464"),sQuery(id+"F0.wireOp",EDGE,"E1465"),sQuery(id+"F0.wireOp",EDGE,"E1466"),sQuery(id+"F0.wireOp",EDGE,"E1467"),sQuery(id+"F0.wireOp",EDGE,"E1468"),sQuery(id+"F0.wireOp",EDGE,"E1469"),sQuery(id+"F0.wireOp",EDGE,"E1470"),sQuery(id+"F0.wireOp",EDGE,"E1471"),sQuery(id+"F0.wireOp",EDGE,"E1472"),sQuery(id+"F0.wireOp",EDGE,"E1473"),sQuery(id+"F0.wireOp",EDGE,"E1474"),sQuery(id+"F0.wireOp",EDGE,"E1475"),sQuery(id+"F0.wireOp",EDGE,"E1476"),sQuery(id+"F0.wireOp",EDGE,"E1477"),sQuery(id+"F0.wireOp",EDGE,"E1478"),sQuery(id+"F0.wireOp",EDGE,"E1479"),sQuery(id+"F0.wireOp",EDGE,"E1480"),sQuery(id+"F0.wireOp",EDGE,"E1481"),sQuery(id+"F0.wireOp",EDGE,"E1482"),sQuery(id+"F0.wireOp",EDGE,"E1483"),sQuery(id+"F0.wireOp",EDGE,"E1484"),sQuery(id+"F0.wireOp",EDGE,"E1485"),sQuery(id+"F0.wireOp",EDGE,"E1486"),sQuery(id+"F0.wireOp",EDGE,"E1487"),sQuery(id+"F0.wireOp",EDGE,"E1488"),sQuery(id+"F0.wireOp",EDGE,"E1489"),sQuery(id+"F0.wireOp",EDGE,"E1490"),sQuery(id+"F0.wireOp",EDGE,"E1491"),sQuery(id+"F0.wireOp",EDGE,"E1492"),sQuery(id+"F0.wireOp",EDGE,"E1493"),sQuery(id+"F0.wireOp",EDGE,"E1494"),sQuery(id+"F0.wireOp",EDGE,"E1495"),sQuery(id+"F0.wireOp",EDGE,"E1496"),sQuery(id+"F0.wireOp",EDGE,"E1497"),sQuery(id+"F0.wireOp",EDGE,"E1498"),sQuery(id+"F0.wireOp",EDGE,"E1499"),sQuery(id+"F0.wireOp",EDGE,"E1500"),sQuery(id+"F0.wireOp",EDGE,"E1501"),sQuery(id+"F0.wireOp",EDGE,"E1502"),sQuery(id+"F0.wireOp",EDGE,"E1503"),sQuery(id+"F0.wireOp",EDGE,"E1504"),sQuery(id+"F0.wireOp",EDGE,"E1505"),sQuery(id+"F0.wireOp",EDGE,"E1506"),sQuery(id+"F0.wireOp",EDGE,"E1507"),sQuery(id+"F0.wireOp",EDGE,"E1508"),sQuery(id+"F0.wireOp",EDGE,"E1509"),sQuery(id+"F0.wireOp",EDGE,"E1510"),sQuery(id+"F0.wireOp",EDGE,"E1511"),sQuery(id+"F0.wireOp",EDGE,"E1512"),sQuery(id+"F0.wireOp",EDGE,"E1513"),sQuery(id+"F0.wireOp",EDGE,"E1514"),sQuery(id+"F0.wireOp",EDGE,"E1515"),sQuery(id+"F0.wireOp",EDGE,"E1516"),sQuery(id+"F0.wireOp",EDGE,"E1517"),sQuery(id+"F0.wireOp",EDGE,"E1518"),sQuery(id+"F0.wireOp",EDGE,"E1519"),sQuery(id+"F0.wireOp",EDGE,"E1520"),sQuery(id+"F0.wireOp",EDGE,"E1521"),sQuery(id+"F0.wireOp",EDGE,"E1522"),sQuery(id+"F0.wireOp",EDGE,"E1523"),sQuery(id+"F0.wireOp",EDGE,"E1524"),sQuery(id+"F0.wireOp",EDGE,"E1525"),sQuery(id+"F0.wireOp",EDGE,"E1526"),sQuery(id+"F0.wireOp",EDGE,"E1527"),sQuery(id+"F0.wireOp",EDGE,"E1528"),sQuery(id+"F0.wireOp",EDGE,"E1529"),sQuery(id+"F0.wireOp",EDGE,"E1530"),sQuery(id+"F0.wireOp",EDGE,"E1531"),sQuery(id+"F0.wireOp",EDGE,"E1532"),sQuery(id+"F0.wireOp",EDGE,"E1533"),sQuery(id+"F0.wireOp",EDGE,"E1534"),sQuery(id+"F0.wireOp",EDGE,"E1535"),sQuery(id+"F0.wireOp",EDGE,"E1536"),sQuery(id+"F0.wireOp",EDGE,"E1537"),sQuery(id+"F0.wireOp",EDGE,"E1538"),sQuery(id+"F0.wireOp",EDGE,"E1539"),sQuery(id+"F0.wireOp",EDGE,"E1540"),sQuery(id+"F0.wireOp",EDGE,"E1541"),sQuery(id+"F0.wireOp",EDGE,"E1542"),sQuery(id+"F0.wireOp",EDGE,"E1543"),sQuery(id+"F0.wireOp",EDGE,"E1544"),sQuery(id+"F0.wireOp",EDGE,"E1545"),sQuery(id+"F0.wireOp",EDGE,"E1546"),sQuery(id+"F0.wireOp",EDGE,"E1547"),sQuery(id+"F0.wireOp",EDGE,"E1548"),sQuery(id+"F0.wireOp",EDGE,"E1549"),sQuery(id+"F0.wireOp",EDGE,"E1550"),sQuery(id+"F0.wireOp",EDGE,"E1551"),sQuery(id+"F0.wireOp",EDGE,"E1552"),sQuery(id+"F0.wireOp",EDGE,"E1553"),sQuery(id+"F0.wireOp",EDGE,"E1554"),sQuery(id+"F0.wireOp",EDGE,"E1555"),sQuery(id+"F0.wireOp",EDGE,"E1556"),sQuery(id+"F0.wireOp",EDGE,"E1557"),sQuery(id+"F0.wireOp",EDGE,"E1558"),sQuery(id+"F0.wireOp",EDGE,"E1559"),sQuery(id+"F0.wireOp",EDGE,"E1560"),sQuery(id+"F0.wireOp",EDGE,"E1561"),sQuery(id+"F0.wireOp",EDGE,"E1562"),sQuery(id+"F0.wireOp",EDGE,"E1563"),sQuery(id+"F0.wireOp",EDGE,"E1564"),sQuery(id+"F0.wireOp",EDGE,"E1565"),sQuery(id+"F0.wireOp",EDGE,"E1566"),sQuery(id+"F0.wireOp",EDGE,"E1567"),sQuery(id+"F0.wireOp",EDGE,"E1568"),sQuery(id+"F0.wireOp",EDGE,"E1569"),sQuery(id+"F0.wireOp",EDGE,"E1570"),sQuery(id+"F0.wireOp",EDGE,"E1571"),sQuery(id+"F0.wireOp",EDGE,"E1572"),sQuery(id+"F0.wireOp",EDGE,"E1573"),sQuery(id+"F0.wireOp",EDGE,"E1574"),sQuery(id+"F0.wireOp",EDGE,"E1575"),sQuery(id+"F0.wireOp",EDGE,"E1576"),sQuery(id+"F0.wireOp",EDGE,"E1577"),sQuery(id+"F0.wireOp",EDGE,"E1578"),sQuery(id+"F0.wireOp",EDGE,"E1579"),sQuery(id+"F0.wireOp",EDGE,"E1580"),sQuery(id+"F0.wireOp",EDGE,"E1581"),sQuery(id+"F0.wireOp",EDGE,"E1582"),sQuery(id+"F0.wireOp",EDGE,"E1583"),sQuery(id+"F0.wireOp",EDGE,"E1584"),sQuery(id+"F0.wireOp",EDGE,"E1585"),sQuery(id+"F0.wireOp",EDGE,"E1586"),sQuery(id+"F0.wireOp",EDGE,"E1587"),sQuery(id+"F0.wireOp",EDGE,"E1588"),sQuery(id+"F0.wireOp",EDGE,"E1589"),sQuery(id+"F0.wireOp",EDGE,"E1590"),sQuery(id+"F0.wireOp",EDGE,"E1591"),sQuery(id+"F0.wireOp",EDGE,"E1592"),sQuery(id+"F0.wireOp",EDGE,"E1593"),sQuery(id+"F0.wireOp",EDGE,"E1594"),sQuery(id+"F0.wireOp",EDGE,"E1595"),sQuery(id+"F0.wireOp",EDGE,"E1596"),sQuery(id+"F0.wireOp",EDGE,"E1597"),sQuery(id+"F0.wireOp",EDGE,"E1598"),sQuery(id+"F0.wireOp",EDGE,"E1599"),sQuery(id+"F0.wireOp",EDGE,"E1600"),sQuery(id+"F0.wireOp",EDGE,"E1601"),sQuery(id+"F0.wireOp",EDGE,"E1602"),sQuery(id+"F0.wireOp",EDGE,"E1603"),sQuery(id+"F0.wireOp",EDGE,"E1604"),sQuery(id+"F0.wireOp",EDGE,"E1605"),sQuery(id+"F0.wireOp",EDGE,"E1606"),sQuery(id+"F0.wireOp",EDGE,"E1607"),sQuery(id+"F0.wireOp",EDGE,"E1608"),sQuery(id+"F0.wireOp",EDGE,"E1609"),sQuery(id+"F0.wireOp",EDGE,"E1610"),sQuery(id+"F0.wireOp",EDGE,"E1611"),sQuery(id+"F0.wireOp",EDGE,"E1612"),sQuery(id+"F0.wireOp",EDGE,"E1613"),sQuery(id+"F0.wireOp",EDGE,"E1614"),sQuery(id+"F0.wireOp",EDGE,"E1615"),sQuery(id+"F0.wireOp",EDGE,"E1616"),sQuery(id+"F0.wireOp",EDGE,"E1617"),sQuery(id+"F0.wireOp",EDGE,"E1618"),sQuery(id+"F0.wireOp",EDGE,"E1619"),sQuery(id+"F0.wireOp",EDGE,"E1620"),sQuery(id+"F0.wireOp",EDGE,"E1621"),sQuery(id+"F0.wireOp",EDGE,"E1622"),sQuery(id+"F0.wireOp",EDGE,"E1623"),sQuery(id+"F0.wireOp",EDGE,"E1624"),sQuery(id+"F0.wireOp",EDGE,"E1625"),sQuery(id+"F0.wireOp",EDGE,"E1626"),sQuery(id+"F0.wireOp",EDGE,"E1627"),sQuery(id+"F0.wireOp",EDGE,"E1628"),sQuery(id+"F0.wireOp",EDGE,"E1629"),sQuery(id+"F0.wireOp",EDGE,"E1630"),sQuery(id+"F0.wireOp",EDGE,"E1631"),sQuery(id+"F0.wireOp",EDGE,"E1632"),sQuery(id+"F0.wireOp",EDGE,"E1633"),sQuery(id+"F0.wireOp",EDGE,"E1634"),sQuery(id+"F0.wireOp",EDGE,"E1635"),sQuery(id+"F0.wireOp",EDGE,"E1636"),sQuery(id+"F0.wireOp",EDGE,"E1637"),sQuery(id+"F0.wireOp",EDGE,"E1638"),sQuery(id+"F0.wireOp",EDGE,"E1639"),sQuery(id+"F0.wireOp",EDGE,"E1640"),sQuery(id+"F0.wireOp",EDGE,"E1641"),sQuery(id+"F0.wireOp",EDGE,"E1642"),sQuery(id+"F0.wireOp",EDGE,"E1643"),sQuery(id+"F0.wireOp",EDGE,"E1644"),sQuery(id+"F0.wireOp",EDGE,"E1645"),sQuery(id+"F0.wireOp",EDGE,"E1646"),sQuery(id+"F0.wireOp",EDGE,"E1647"),sQuery(id+"F0.wireOp",EDGE,"E1648"),sQuery(id+"F0.wireOp",EDGE,"E1649"),sQuery(id+"F0.wireOp",EDGE,"E1650"),sQuery(id+"F0.wireOp",EDGE,"E1651"),sQuery(id+"F0.wireOp",EDGE,"E1652"),sQuery(id+"F0.wireOp",EDGE,"E1653"),sQuery(id+"F0.wireOp",EDGE,"E1654"),sQuery(id+"F0.wireOp",EDGE,"E1655"),sQuery(id+"F0.wireOp",EDGE,"E1656"),sQuery(id+"F0.wireOp",EDGE,"E1657"),sQuery(id+"F0.wireOp",EDGE,"E1658"),sQuery(id+"F0.wireOp",EDGE,"E1659"),sQuery(id+"F0.wireOp",EDGE,"E1660"),sQuery(id+"F0.wireOp",EDGE,"E1661"),sQuery(id+"F0.wireOp",EDGE,"E1662"),sQuery(id+"F0.wireOp",EDGE,"E1663"),sQuery(id+"F0.wireOp",EDGE,"E1664"),sQuery(id+"F0.wireOp",EDGE,"E1665"),sQuery(id+"F0.wireOp",EDGE,"E1666"),sQuery(id+"F0.wireOp",EDGE,"E1667"),sQuery(id+"F0.wireOp",EDGE,"E1668"),sQuery(id+"F0.wireOp",EDGE,"E1669"),sQuery(id+"F0.wireOp",EDGE,"E1670"),sQuery(id+"F0.wireOp",EDGE,"E1671"),sQuery(id+"F0.wireOp",EDGE,"E1672"),sQuery(id+"F0.wireOp",EDGE,"E1673"),sQuery(id+"F0.wireOp",EDGE,"E1674"),sQuery(id+"F0.wireOp",EDGE,"E1675"),sQuery(id+"F0.wireOp",EDGE,"E1676"),sQuery(id+"F0.wireOp",EDGE,"E1677"),sQuery(id+"F0.wireOp",EDGE,"E1678"),sQuery(id+"F0.wireOp",EDGE,"E1679"),sQuery(id+"F0.wireOp",EDGE,"E1680"),sQuery(id+"F0.wireOp",EDGE,"E1681"),sQuery(id+"F0.wireOp",EDGE,"E1682"),sQuery(id+"F0.wireOp",EDGE,"E1683"),sQuery(id+"F0.wireOp",EDGE,"E1684"),sQuery(id+"F0.wireOp",EDGE,"E1685"),sQuery(id+"F0.wireOp",EDGE,"E1686"),sQuery(id+"F0.wireOp",EDGE,"E1687"),sQuery(id+"F0.wireOp",EDGE,"E1688"),sQuery(id+"F0.wireOp",EDGE,"E1689"),sQuery(id+"F0.wireOp",EDGE,"E1690"),sQuery(id+"F0.wireOp",EDGE,"E1691"),sQuery(id+"F0.wireOp",EDGE,"E1692"),sQuery(id+"F0.wireOp",EDGE,"E1693"),sQuery(id+"F0.wireOp",EDGE,"E1694"),sQuery(id+"F0.wireOp",EDGE,"E1695"),sQuery(id+"F0.wireOp",EDGE,"E1696"),sQuery(id+"F0.wireOp",EDGE,"E1697"),sQuery(id+"F0.wireOp",EDGE,"E1698"),sQuery(id+"F0.wireOp",EDGE,"E1699"),sQuery(id+"F0.wireOp",EDGE,"E1700"),sQuery(id+"F0.wireOp",EDGE,"E1701"),sQuery(id+"F0.wireOp",EDGE,"E1702"),sQuery(id+"F0.wireOp",EDGE,"E1703"),sQuery(id+"F0.wireOp",EDGE,"E1704"),sQuery(id+"F0.wireOp",EDGE,"E1705"),sQuery(id+"F0.wireOp",EDGE,"E1706"),sQuery(id+"F0.wireOp",EDGE,"E1707"),sQuery(id+"F0.wireOp",EDGE,"E1708"),sQuery(id+"F0.wireOp",EDGE,"E1709"),sQuery(id+"F0.wireOp",EDGE,"E1710"),sQuery(id+"F0.wireOp",EDGE,"E1711"),sQuery(id+"F0.wireOp",EDGE,"E1712"),sQuery(id+"F0.wireOp",EDGE,"E1713"),sQuery(id+"F0.wireOp",EDGE,"E1714"),sQuery(id+"F0.wireOp",EDGE,"E1715"),sQuery(id+"F0.wireOp",EDGE,"E1716"),sQuery(id+"F0.wireOp",EDGE,"E1717"),sQuery(id+"F0.wireOp",EDGE,"E1718"),sQuery(id+"F0.wireOp",EDGE,"E1719"),sQuery(id+"F0.wireOp",EDGE,"E1720"),sQuery(id+"F0.wireOp",EDGE,"E1721"),sQuery(id+"F0.wireOp",EDGE,"E1722"),sQuery(id+"F0.wireOp",EDGE,"E1723"),sQuery(id+"F0.wireOp",EDGE,"E1724"),sQuery(id+"F0.wireOp",EDGE,"E1725"),sQuery(id+"F0.wireOp",EDGE,"E1726"),sQuery(id+"F0.wireOp",EDGE,"E1727"),sQuery(id+"F0.wireOp",EDGE,"E1728"),sQuery(id+"F0.wireOp",EDGE,"E1729"),sQuery(id+"F0.wireOp",EDGE,"E1730"),sQuery(id+"F0.wireOp",EDGE,"E1731"),sQuery(id+"F0.wireOp",EDGE,"E1732"),sQuery(id+"F0.wireOp",EDGE,"E1733"),sQuery(id+"F0.wireOp",EDGE,"E1734"),sQuery(id+"F0.wireOp",EDGE,"E1735"),sQuery(id+"F0.wireOp",EDGE,"E1736"),sQuery(id+"F0.wireOp",EDGE,"E1737"),sQuery(id+"F0.wireOp",EDGE,"E1738"),sQuery(id+"F0.wireOp",EDGE,"E1739"),sQuery(id+"F0.wireOp",EDGE,"E1740"),sQuery(id+"F0.wireOp",EDGE,"E1741"),sQuery(id+"F0.wireOp",EDGE,"E1742"),sQuery(id+"F0.wireOp",EDGE,"E1743"),sQuery(id+"F0.wireOp",EDGE,"E1744"),sQuery(id+"F0.wireOp",EDGE,"E1745"),sQuery(id+"F0.wireOp",EDGE,"E1746"),sQuery(id+"F0.wireOp",EDGE,"E1747"),sQuery(id+"F0.wireOp",EDGE,"E1748"),sQuery(id+"F0.wireOp",EDGE,"E1749"),sQuery(id+"F0.wireOp",EDGE,"E1750"),sQuery(id+"F0.wireOp",EDGE,"E1751"),sQuery(id+"F0.wireOp",EDGE,"E1752"),sQuery(id+"F0.wireOp",EDGE,"E1753"),sQuery(id+"F0.wireOp",EDGE,"E1754"),sQuery(id+"F0.wireOp",EDGE,"E1755"),sQuery(id+"F0.wireOp",EDGE,"E1756"),sQuery(id+"F0.wireOp",EDGE,"E1757"),sQuery(id+"F0.wireOp",EDGE,"E1758"),sQuery(id+"F0.wireOp",EDGE,"E1759"),sQuery(id+"F0.wireOp",EDGE,"E1760"),sQuery(id+"F0.wireOp",EDGE,"E1761"),sQuery(id+"F0.wireOp",EDGE,"E1762"),sQuery(id+"F0.wireOp",EDGE,"E1763"),sQuery(id+"F0.wireOp",EDGE,"E1764"),sQuery(id+"F0.wireOp",EDGE,"E1765"),sQuery(id+"F0.wireOp",EDGE,"E1766"),sQuery(id+"F0.wireOp",EDGE,"E1767"),sQuery(id+"F0.wireOp",EDGE,"E1768"),sQuery(id+"F0.wireOp",EDGE,"E1769"),sQuery(id+"F0.wireOp",EDGE,"E1770"),sQuery(id+"F0.wireOp",EDGE,"E1771"),sQuery(id+"F0.wireOp",EDGE,"E1772"),sQuery(id+"F0.wireOp",EDGE,"E1773"),sQuery(id+"F0.wireOp",EDGE,"E1774"),sQuery(id+"F0.wireOp",EDGE,"E1775"),sQuery(id+"F0.wireOp",EDGE,"E1776"),sQuery(id+"F0.wireOp",EDGE,"E1777"),sQuery(id+"F0.wireOp",EDGE,"E1778"),sQuery(id+"F0.wireOp",EDGE,"E1779"),sQuery(id+"F0.wireOp",EDGE,"E1780"),sQuery(id+"F0.wireOp",EDGE,"E1781"),sQuery(id+"F0.wireOp",EDGE,"E1782"),sQuery(id+"F0.wireOp",EDGE,"E1783"),sQuery(id+"F0.wireOp",EDGE,"E1784"),sQuery(id+"F0.wireOp",EDGE,"E1785"),sQuery(id+"F0.wireOp",EDGE,"E1786"),sQuery(id+"F0.wireOp",EDGE,"E1787"),sQuery(id+"F0.wireOp",EDGE,"E1788"),sQuery(id+"F0.wireOp",EDGE,"E1789"),sQuery(id+"F0.wireOp",EDGE,"E1790"),sQuery(id+"F0.wireOp",EDGE,"E1791"),sQuery(id+"F0.wireOp",EDGE,"E1792"),sQuery(id+"F0.wireOp",EDGE,"E1793"),sQuery(id+"F0.wireOp",EDGE,"E1794"),sQuery(id+"F0.wireOp",EDGE,"E1795"),sQuery(id+"F0.wireOp",EDGE,"E1796"),sQuery(id+"F0.wireOp",EDGE,"E1797"),sQuery(id+"F0.wireOp",EDGE,"E1798"),sQuery(id+"F0.wireOp",EDGE,"E1799"),sQuery(id+"F0.wireOp",EDGE,"E1800"),sQuery(id+"F0.wireOp",EDGE,"E1801"),sQuery(id+"F0.wireOp",EDGE,"E1802"),sQuery(id+"F0.wireOp",EDGE,"E1803"),sQuery(id+"F0.wireOp",EDGE,"E1804"),sQuery(id+"F0.wireOp",EDGE,"E1805"),sQuery(id+"F0.wireOp",EDGE,"E1806"),sQuery(id+"F0.wireOp",EDGE,"E1807"),sQuery(id+"F0.wireOp",EDGE,"E1808"),sQuery(id+"F0.wireOp",EDGE,"E1809"),sQuery(id+"F0.wireOp",EDGE,"E1810"),sQuery(id+"F0.wireOp",EDGE,"E1811"),sQuery(id+"F0.wireOp",EDGE,"E1812"),sQuery(id+"F0.wireOp",EDGE,"E1813"),sQuery(id+"F0.wireOp",EDGE,"E1814"),sQuery(id+"F0.wireOp",EDGE,"E1815"),sQuery(id+"F0.wireOp",EDGE,"E1816"),sQuery(id+"F0.wireOp",EDGE,"E1817"),sQuery(id+"F0.wireOp",EDGE,"E1818"),sQuery(id+"F0.wireOp",EDGE,"E1819"),sQuery(id+"F0.wireOp",EDGE,"E1820"),sQuery(id+"F0.wireOp",EDGE,"E1821"),sQuery(id+"F0.wireOp",EDGE,"E1822"),sQuery(id+"F0.wireOp",EDGE,"E1823"),sQuery(id+"F0.wireOp",EDGE,"E1824"),sQuery(id+"F0.wireOp",EDGE,"E1825"),sQuery(id+"F0.wireOp",EDGE,"E1826"),sQuery(id+"F0.wireOp",EDGE,"E1827"),sQuery(id+"F0.wireOp",EDGE,"E1828"),sQuery(id+"F0.wireOp",EDGE,"E1829"),sQuery(id+"F0.wireOp",EDGE,"E1830"),sQuery(id+"F0.wireOp",EDGE,"E1831"),sQuery(id+"F0.wireOp",EDGE,"E1832"),sQuery(id+"F0.wireOp",EDGE,"E1833"),sQuery(id+"F0.wireOp",EDGE,"E1834"),sQuery(id+"F0.wireOp",EDGE,"E1835"),sQuery(id+"F0.wireOp",EDGE,"E1836"),sQuery(id+"F0.wireOp",EDGE,"E1837"),sQuery(id+"F0.wireOp",EDGE,"E1838"),sQuery(id+"F0.wireOp",EDGE,"E1839"),sQuery(id+"F0.wireOp",EDGE,"E1840"),sQuery(id+"F0.wireOp",EDGE,"E1841"),sQuery(id+"F0.wireOp",EDGE,"E1842"),sQuery(id+"F0.wireOp",EDGE,"E1843"),sQuery(id+"F0.wireOp",EDGE,"E1844"),sQuery(id+"F0.wireOp",EDGE,"E1845"),sQuery(id+"F0.wireOp",EDGE,"E1846"),sQuery(id+"F0.wireOp",EDGE,"E1847"),sQuery(id+"F0.wireOp",EDGE,"E1848"),sQuery(id+"F0.wireOp",EDGE,"E1849"),sQuery(id+"F0.wireOp",EDGE,"E1850"),sQuery(id+"F0.wireOp",EDGE,"E1851"),sQuery(id+"F0.wireOp",EDGE,"E1852"),sQuery(id+"F0.wireOp",EDGE,"E1853"),sQuery(id+"F0.wireOp",EDGE,"E1854"),sQuery(id+"F0.wireOp",EDGE,"E1855"),sQuery(id+"F0.wireOp",EDGE,"E1856"),sQuery(id+"F0.wireOp",EDGE,"E1857"),sQuery(id+"F0.wireOp",EDGE,"E1858"),sQuery(id+"F0.wireOp",EDGE,"E1859"),sQuery(id+"F0.wireOp",EDGE,"E1860"),sQuery(id+"F0.wireOp",EDGE,"E1861"),sQuery(id+"F0.wireOp",EDGE,"E1862"),sQuery(id+"F0.wireOp",EDGE,"E1863"),sQuery(id+"F0.wireOp",EDGE,"E1864"),sQuery(id+"F0.wireOp",EDGE,"E1865"),sQuery(id+"F0.wireOp",EDGE,"E1866"),sQuery(id+"F0.wireOp",EDGE,"E1867"),sQuery(id+"F0.wireOp",EDGE,"E1868"),sQuery(id+"F0.wireOp",EDGE,"E1869"),sQuery(id+"F0.wireOp",EDGE,"E1870"),sQuery(id+"F0.wireOp",EDGE,"E1871")])],"isStart":false});
            var sketch = newSketch(context, id + "F2", { "sketchPlane" : qUnion([Q0])});
            skCircle(sketch, "E1872", {"center": v(0, 0) * mm, "radius": 10 * mm});
            skLineSegment(sketch, "E1873.bottom", {"start": v(-3, 6.5) * mm, "end": v(3, 6.5) * mm});
            skLineSegment(sketch, "E1873.top", {"start": v(-3, 12.5) * mm, "end": v(3, 12.5) * mm});
            skLineSegment(sketch, "E1873.left", {"start": v(-3, 6.5) * mm, "end": v(-3, 12.5) * mm});
            skLineSegment(sketch, "E1873.right", {"start": v(3, 6.5) * mm, "end": v(3, 12.5) * mm});
            skLineSegment(sketch, "E1874.bottom", {"start": v(-3, -12.5) * mm, "end": v(3, -12.5) * mm});
            skLineSegment(sketch, "E1874.top", {"start": v(-3, -6.5) * mm, "end": v(3, -6.5) * mm});
            skLineSegment(sketch, "E1874.left", {"start": v(-3, -12.5) * mm, "end": v(-3, -6.5) * mm});
            skLineSegment(sketch, "E1874.right", {"start": v(3, -12.5) * mm, "end": v(3, -6.5) * mm});
            skSolve(sketch);
        }
        {
            var Q0;
            {var subQ5=sQuery(id+"F2.wireOp",EDGE,"E1873.bottom");Q0=makeQuery(id+"F2.imprint","IMPRINT",FACE,{"disambiguationData":[TD([[makeQuery(id+"F2.imprint","IMPRINT",EDGE,{"derivedFrom":subQ5}),-1.0]])]});}
            var Q1;
            {var subQ5=sQuery(id+"F2.wireOp",EDGE,"E1873.top");Q1=makeQuery(id+"F2.imprint","IMPRINT",FACE,{"disambiguationData":[TD([[makeQuery(id+"F2.imprint","IMPRINT",EDGE,{"derivedFrom":subQ5}),-1.0]])]});}
            var Q2;
            {var subQ5=sQuery(id+"F2.wireOp",EDGE,"E1873.bottom");Q2=makeQuery(id+"F2.imprint","IMPRINT",FACE,{"disambiguationData":[TD([[makeQuery(id+"F2.imprint","IMPRINT",EDGE,{"derivedFrom":subQ5}),1.0]])]});}
            var Q3;
            {var subQ5=sQuery(id+"F2.wireOp",EDGE,"E1874.top");Q3=makeQuery(id+"F2.imprint","IMPRINT",FACE,{"disambiguationData":[TD([[makeQuery(id+"F2.imprint","IMPRINT",EDGE,{"derivedFrom":subQ5}),-1.0]])]});}
            var Q4;
            {var subQ5=sQuery(id+"F2.wireOp",EDGE,"E1874.bottom");Q4=makeQuery(id+"F2.imprint","IMPRINT",FACE,{"disambiguationData":[TD([[makeQuery(id+"F2.imprint","IMPRINT",EDGE,{"derivedFrom":subQ5}),1.0]])]});}
            extrude(context, id + "F3", {"entities" : qUnion([Q0, Q1, Q2, Q3, Q4]), "operationType" : NewBodyOperationType.REMOVE, "oppositeDirection" : true, "depth" : 5 * mm});
        }
    });
